MODEL slx_7c77e1fec809
KIND model
CONFIG AbsTol = auto
CONFIG EnableMultiTasking = on
CONFIG FixedStep = step_size
CONFIG InitFcn = , if any(exist('rtifpga_mdlclblib', 'file') ~= 0), rtifpga_mdlclblib('Init', bdroot); end,\n, if any(exist('dsmpb_private', 'file') ~= 0), dsmpb_private('dsmpb_mdlclblib', 'Init', bdroot); end,\n
CONFIG MaxStep = auto
CONFIG MinStep = auto
CONFIG PostLoadFcn = if any(exist('dsrtsu_mdlpostloadfcn', 'file') ~= 0), dsrtsu_mdlpostloadfcn('Execute', bdroot); end
CONFIG RelTol = 1e-3
CONFIG SampleTimeConstraint = Unconstrained
CONFIG SolverName = ode1
CONFIG StartTime = 0.0
CONFIG StopTime = t_end
BLOCK [Clock] Clock1
BLOCK [Display] Display
  Decimation = 1
BLOCK [Display] Display1
  Decimation = 1
BLOCK [Display] Display2
  Decimation = 1
BLOCK [Display] Display3
  Decimation = 1
BLOCK [Display] Display5
  Decimation = 1
BLOCK [Display] Display6
  Decimation = 1
BLOCK [Display] Display7
  Decimation = 1
BLOCK [SubSystem] Distance Check
BLOCK [SubSystem] Distance Check/Distance Change Security Check
BLOCK [Constant] Distance Check/Distance Change Security Check/Constant
  Value = start_distance_check
BLOCK [Constant] Distance Check/Distance Change Security Check/Constant1
  Value = break_criteria
BLOCK [SubSystem] Distance Check/Distance Change Security Check/MATLAB Function
  ErrorFcn = Stateflow.Translate.translate
  PermitHierarchicalResolution = ExplicitOnly
  SFBlockType = MATLAB Function
  TreatAsAtomicUnit = on
BLOCK [Demux] Distance Check/Distance Change Security Check/MATLAB Function/ Demux 
  Outputs = 1
BLOCK [S-Function] Distance Check/Distance Change Security Check/MATLAB Function/ SFunction 
  EnableBusSupport = on
  FunctionName = sf_sfun
  PortCounts = [4 2]
  SFcnIsStateOwnerBlock = off
  SFunctionDeploymentMode = off
  Tag = Stateflow S-Function 2
BLOCK [Terminator] Distance Check/Distance Change Security Check/MATLAB Function/ Terminator 
BLOCK [Outport] Distance Check/Distance Change Security Check/MATLAB Function/bool_stop
BLOCK [Inport] Distance Check/Distance Change Security Check/MATLAB Function/break_criteria
  Port = 4
BLOCK [Inport] Distance Check/Distance Change Security Check/MATLAB Function/s
BLOCK [Inport] Distance Check/Distance Change Security Check/MATLAB Function/s_old
  Port = 2
BLOCK [Inport] Distance Check/Distance Change Security Check/MATLAB Function/start_distance_check
  Port = 3
BLOCK [Memory] Distance Check/Distance Change Security Check/Memory
  InheritSampleTime = on
BLOCK [Outport] Distance Check/Distance Change Security Check/bool_stop
BLOCK [Inport] Distance Check/Distance Change Security Check/s
BLOCK [Stop] Distance Check/Stop Simulation
BLOCK [ToWorkspace] Distance Check/To Workspace24
  FixptAsFi = on
  MaxDataPoints = 1
  SampleTime = -1
  Save2DSignal = 2-D array (concatenate along first dimension)
  VariableName = bool_stop
BLOCK [Inport] Distance Check/s (m)
BLOCK [SubSystem] Finish Line
BLOCK [Constant] Finish Line/Constant
  Value = 0
BLOCK [Constant] Finish Line/Constant1
BLOCK [Stop] Finish Line/Stop Simulation
BLOCK [Inport] Finish Line/s (m)
BLOCK [Switch] Finish Line/s>finish line
  InputSameDT = off
  SaturateOnIntegerOverflow = off
  Threshold = s_track(end)
BLOCK [Gain] Finish Line/s_ist
BLOCK [Display] Finish Time // s
  Decimation = 1
BLOCK [From] From
  GotoTag = T_wr
  TagVisibility = global
BLOCK [From] From1
  GotoTag = v_ist
  TagVisibility = global
BLOCK [From] From2
  GotoTag = v_des
  TagVisibility = global
BLOCK [From] From3
  GotoTag = T_wr_LSTM
  TagVisibility = global
BLOCK [From] From4
  GotoTag = noisy_meas
  TagVisibility = global
BLOCK [From] From5
  GotoTag = MHE_results
  TagVisibility = global
BLOCK [From] From7
  GotoTag = MPC_solver_status
  TagVisibility = global
BLOCK [From] From8
  GotoTag = MHE_solverstatus
  TagVisibility = global
BLOCK [SubSystem] MPC
  NameLocation = top
BLOCK [Sum] MPC/Add
  IconShape = rectangular
  Inputs = +++
BLOCK [Clock] MPC/Clock
BLOCK [Constant] MPC/Constant
  NameLocation = top
  SampleTime = options.Ts
  Value = u_max
BLOCK [Constant] MPC/Constant1
  SampleTime = options.Ts
  Value = lbx_ac
BLOCK [Constant] MPC/Constant10
  SampleTime = options.Ts
  Value = ubx_ac_e
BLOCK [Constant] MPC/Constant11
  SampleTime = options.Ts
  Value = options.P
BLOCK [Constant] MPC/Constant2
  SampleTime = options.Ts
  Value = ubx_ac
BLOCK [Constant] MPC/Constant3
  SampleTime = options.Ts
  Value = u_ref
BLOCK [Constant] MPC/Constant4
  NameLocation = top
  SampleTime = options.Ts
  Value = u_min
  VectorParams1D = off
BLOCK [Constant] MPC/Constant5
  SampleTime = options.Ts
  Value = lbh_ac
BLOCK [Constant] MPC/Constant6
  SampleTime = options.Ts
  Value = options.P
BLOCK [Constant] MPC/Constant8
  SampleTime = options.Ts
  Value = lbx_ac_e
BLOCK [Constant] MPC/Constant9
  SampleTime = options.Ts
  Value = ubh_ac
BLOCK [Demux] MPC/Demux
  Outputs = 3
BLOCK [Demux] MPC/Demux1
  Outputs = options.n_controls
BLOCK [Demux] MPC/Demux2
  Commented = on
  Outputs = 3
BLOCK [Display] MPC/Display
  Decimation = 1
BLOCK [Display] MPC/Display10
  Decimation = 1
BLOCK [Display] MPC/Display11
  Decimation = 1
BLOCK [Display] MPC/Display12
  Decimation = 1
BLOCK [Display] MPC/Display17
  Decimation = 1
BLOCK [Display] MPC/Display18
  Decimation = 1
BLOCK [Display] MPC/Display2
  Decimation = 1
BLOCK [Display] MPC/Display21
  Decimation = 1
  NameLocation = top
BLOCK [Display] MPC/Display24
  Decimation = 1
BLOCK [Display] MPC/Display25
  Decimation = 1
BLOCK [Display] MPC/Display3
  Commented = on
  Decimation = 1
BLOCK [Display] MPC/Display4
  Decimation = 1
BLOCK [Display] MPC/Display5
  Decimation = 1
BLOCK [Display] MPC/Display6
  Decimation = 1
BLOCK [Display] MPC/Display7
  Decimation = 1
BLOCK [Display] MPC/Display8
  Decimation = 1
BLOCK [From] MPC/From1
  GotoTag = T_wr
  TagVisibility = global
BLOCK [From] MPC/From10
  Commented = on
  GotoTag = torque_em_brk
  TagVisibility = global
BLOCK [From] MPC/From11
  Commented = on
  GotoTag = torque_fric_brk
  TagVisibility = global
BLOCK [From] MPC/From2
  GotoTag = v_ist
  TagVisibility = global
BLOCK [From] MPC/From3
  GotoTag = v_des
  TagVisibility = global
BLOCK [From] MPC/From8
  GotoTag = solver_x_LSTM
  TagVisibility = global
BLOCK [From] MPC/From9
  Commented = on
  GotoTag = torque_em_acc
  TagVisibility = global
BLOCK [Gain] MPC/Gain
  Gain = pi/180
BLOCK [Gain] MPC/Gain1
  Gain = FDR/r_dyn
BLOCK [Goto] MPC/Goto
  GotoTag = solver_x_LSTM
  TagVisibility = global
BLOCK [Goto] MPC/Goto2
  GotoTag = phi_values
  TagVisibility = global
BLOCK [Goto] MPC/Goto3
  GotoTag = MPC_solver_status
  TagVisibility = global
BLOCK [Ground] MPC/Ground
  Commented = on
BLOCK [Ground] MPC/Ground1
  Commented = on
BLOCK [Ground] MPC/Ground2
  Commented = on
BLOCK [SubSystem] MPC/MATLAB Function
  ErrorFcn = Stateflow.Translate.translate
  PermitHierarchicalResolution = ExplicitOnly
  SFBlockType = MATLAB Function
  TreatAsAtomicUnit = on
BLOCK [Demux] MPC/MATLAB Function/ Demux 
  Outputs = 1
BLOCK [S-Function] MPC/MATLAB Function/ SFunction 
  EnableBusSupport = on
  FunctionName = sf_sfun
  PortCounts = [3 2]
  SFcnIsStateOwnerBlock = off
  SFunctionDeploymentMode = off
  Tag = Stateflow S-Function 6
BLOCK [Terminator] MPC/MATLAB Function/ Terminator 
BLOCK [Inport] MPC/MATLAB Function/P
  Port = 3
BLOCK [Inport] MPC/MATLAB Function/u1
  Port = 2
BLOCK [Inport] MPC/MATLAB Function/x
BLOCK [Outport] MPC/MATLAB Function/y_ref_merged
  VectorParamsAs1DForOutWhenUnconnected = off
BLOCK [SubSystem] MPC/MATLAB Function1
  ErrorFcn = Stateflow.Translate.translate
  PermitHierarchicalResolution = ExplicitOnly
  SFBlockType = MATLAB Function
  TreatAsAtomicUnit = on
BLOCK [Demux] MPC/MATLAB Function1/ Demux 
  Outputs = 1
BLOCK [S-Function] MPC/MATLAB Function1/ SFunction 
  EnableBusSupport = on
  FunctionName = sf_sfun
  PortCounts = [3 2]
  SFcnIsStateOwnerBlock = off
  SFunctionDeploymentMode = off
  Tag = Stateflow S-Function 12
BLOCK [Terminator] MPC/MATLAB Function1/ Terminator 
BLOCK [Inport] MPC/MATLAB Function1/P
  Port = 3
BLOCK [Outport] MPC/MATLAB Function1/par_traj_merged
  VectorParamsAs1DForOutWhenUnconnected = off
BLOCK [Inport] MPC/MATLAB Function1/phi
BLOCK [Inport] MPC/MATLAB Function1/v_r
  Port = 2
BLOCK [Memory] MPC/Memory
  InheritSampleTime = on
BLOCK [Product] MPC/Multiply
BLOCK [Mux] MPC/Mux
  DisplayOption = bar
  Inputs = 2
BLOCK [Mux] MPC/Mux1
  DisplayOption = bar
  Inputs = 3
BLOCK [Mux] MPC/Mux2
  Commented = on
  Inputs = 6
BLOCK [SubSystem] MPC/Pred_Traj_and_costs_calc
  Commented = on
BLOCK [Sum] MPC/Pred_Traj_and_costs_calc/Add
  IconShape = rectangular
  Inputs = +++
BLOCK [Outport] MPC/Pred_Traj_and_costs_calc/Costs
  VectorParamsAs1DForOutWhenUnconnected = off
BLOCK [Display] MPC/Pred_Traj_and_costs_calc/Display1
  Decimation = 1
BLOCK [Display] MPC/Pred_Traj_and_costs_calc/Display15
  Decimation = 1
BLOCK [Display] MPC/Pred_Traj_and_costs_calc/Display16
  Decimation = 1
BLOCK [Display] MPC/Pred_Traj_and_costs_calc/Display17
  Decimation = 1
BLOCK [Display] MPC/Pred_Traj_and_costs_calc/Display19
  Decimation = 1
BLOCK [Display] MPC/Pred_Traj_and_costs_calc/Display2
  Decimation = 1
BLOCK [Display] MPC/Pred_Traj_and_costs_calc/Display3
  Decimation = 1
BLOCK [Display] MPC/Pred_Traj_and_costs_calc/Display4
  Decimation = 1
BLOCK [Display] MPC/Pred_Traj_and_costs_calc/Display5
  Decimation = 1
BLOCK [Display] MPC/Pred_Traj_and_costs_calc/Display6
  Decimation = 1
BLOCK [Display] MPC/Pred_Traj_and_costs_calc/Display9
  Decimation = 1
BLOCK [Gain] MPC/Pred_Traj_and_costs_calc/Gain1
  Gain = FDR/r_dyn
BLOCK [Gain] MPC/Pred_Traj_and_costs_calc/Gain2
  Gain = (FDR*30)/(pi*r_dyn)
BLOCK [Product] MPC/Pred_Traj_and_costs_calc/Multiply
BLOCK [Selector] MPC/Pred_Traj_and_costs_calc/Selector1
  IndexOptions = Index vector (dialog)
  Indices = [2:options.n_controls:options.n_controls*options.P]
  InputPortWidth = options.n_controls*options.P
  OutputSizes = 1
BLOCK [Selector] MPC/Pred_Traj_and_costs_calc/Selector10
  IndexOptions = Index vector (dialog)
  Indices = [1]
  InputPortWidth = options.P
  OutputSizes = 1
BLOCK [Selector] MPC/Pred_Traj_and_costs_calc/Selector11
  IndexOptions = Index vector (dialog)
  Indices = [1]
  InputPortWidth = options.P
  OutputSizes = 1
BLOCK [Selector] MPC/Pred_Traj_and_costs_calc/Selector12
  IndexOptions = Index vector (dialog)
  Indices = [1]
  InputPortWidth = options.P
  OutputSizes = 1
BLOCK [Selector] MPC/Pred_Traj_and_costs_calc/Selector13
  IndexOptions = Index vector (dialog)
  Indices = [1:options.n_controls:options.n_controls*options.P]
  InputPortWidth = options.n_controls*options.P
  OutputSizes = 1
BLOCK [Selector] MPC/Pred_Traj_and_costs_calc/Selector2
  IndexOptions = Index vector (dialog)
  Indices = [3:options.n_controls:options.n_controls*options.P]
  InputPortWidth = options.n_controls*options.P
  OutputSizes = 1
BLOCK [Selector] MPC/Pred_Traj_and_costs_calc/Selector4
  IndexOptions = Index vector (dialog)
  Indices = [2:options.n_states:options.n_states*options.P-2]
  InputPortWidth = options.n_states*options.P
  OutputSizes = 1
BLOCK [Selector] MPC/Pred_Traj_and_costs_calc/Selector5
  IndexOptions = Index vector (dialog)
  Indices = [3:options.n_states:options.n_states*options.P-1]
  InputPortWidth = options.n_states*options.P
  OutputSizes = 1
BLOCK [Selector] MPC/Pred_Traj_and_costs_calc/Selector7
  IndexOptions = Index vector (dialog)
  Indices = [1:options.n_states:options.n_states*options.P-3]
  InputPortWidth = options.n_states*options.P
  OutputSizes = 1
BLOCK [Selector] MPC/Pred_Traj_and_costs_calc/Selector8
  IndexOptions = Index vector (dialog)
  Indices = [options.n_states:options.n_states:options.n_states*options.P]
  InputPortWidth = options.n_states*options.P
  OutputSizes = 1
BLOCK [Selector] MPC/Pred_Traj_and_costs_calc/Selector9
  IndexOptions = Index vector (dialog)
  Indices = [1]
  InputPortWidth = options.P
  OutputSizes = 1
BLOCK [SubSystem] MPC/Pred_Traj_and_costs_calc/Subsystem
BLOCK [Constant] MPC/Pred_Traj_and_costs_calc/Subsystem/Constant
  Value = Q(3,3)
BLOCK [Constant] MPC/Pred_Traj_and_costs_calc/Subsystem/Constant1
  Value = R(1,1)
BLOCK [Constant] MPC/Pred_Traj_and_costs_calc/Subsystem/Constant2
  Value = U(1,1)
BLOCK [Constant] MPC/Pred_Traj_and_costs_calc/Subsystem/Constant3
  Value = options.P
BLOCK [SubSystem] MPC/Pred_Traj_and_costs_calc/Subsystem/MATLAB Function
  ErrorFcn = Stateflow.Translate.translate
  PermitHierarchicalResolution = ExplicitOnly
  SFBlockType = MATLAB Function
  TreatAsAtomicUnit = on
BLOCK [Demux] MPC/Pred_Traj_and_costs_calc/Subsystem/MATLAB Function/ Demux 
  Outputs = 1
BLOCK [S-Function] MPC/Pred_Traj_and_costs_calc/Subsystem/MATLAB Function/ SFunction 
  EnableBusSupport = off
  FunctionName = sf_sfun
  PortCounts = [8 6]
  SFcnIsStateOwnerBlock = off
  SFunctionDeploymentMode = off
  Tag = Stateflow S-Function 9
BLOCK [Terminator] MPC/Pred_Traj_and_costs_calc/Subsystem/MATLAB Function/ Terminator 
BLOCK [Inport] MPC/Pred_Traj_and_costs_calc/Subsystem/MATLAB Function/P
  Port = 8
BLOCK [Inport] MPC/Pred_Traj_and_costs_calc/Subsystem/MATLAB Function/Q
  Port = 5
BLOCK [Inport] MPC/Pred_Traj_and_costs_calc/Subsystem/MATLAB Function/R
  Port = 6
BLOCK [Inport] MPC/Pred_Traj_and_costs_calc/Subsystem/MATLAB Function/U
  Port = 7
BLOCK [Outport] MPC/Pred_Traj_and_costs_calc/Subsystem/MATLAB Function/cost
  VectorParamsAs1DForOutWhenUnconnected = off
BLOCK [Outport] MPC/Pred_Traj_and_costs_calc/Subsystem/MATLAB Function/cost_Q
  Port = 2
  VectorParamsAs1DForOutWhenUnconnected = off
BLOCK [Outport] MPC/Pred_Traj_and_costs_calc/Subsystem/MATLAB Function/cost_R
  Port = 3
  VectorParamsAs1DForOutWhenUnconnected = off
BLOCK [Outport] MPC/Pred_Traj_and_costs_calc/Subsystem/MATLAB Function/cost_U
  Port = 4
  VectorParamsAs1DForOutWhenUnconnected = off
BLOCK [Outport] MPC/Pred_Traj_and_costs_calc/Subsystem/MATLAB Function/cost_traj
  Port = 5
  VectorParamsAs1DForOutWhenUnconnected = off
BLOCK [Inport] MPC/Pred_Traj_and_costs_calc/Subsystem/MATLAB Function/dt_u
  Port = 4
BLOCK [Inport] MPC/Pred_Traj_and_costs_calc/Subsystem/MATLAB Function/u
  Port = 3
BLOCK [Inport] MPC/Pred_Traj_and_costs_calc/Subsystem/MATLAB Function/v
BLOCK [Inport] MPC/Pred_Traj_and_costs_calc/Subsystem/MATLAB Function/v_ref
  Port = 2
BLOCK [ToWorkspace] MPC/Pred_Traj_and_costs_calc/Subsystem/To Workspace
  FixptAsFi = on
  MaxDataPoints = inf
  SampleTime = -1
  VariableName = cost_v
BLOCK [ToWorkspace] MPC/Pred_Traj_and_costs_calc/Subsystem/To Workspace1
  FixptAsFi = on
  MaxDataPoints = inf
  SampleTime = -1
  VariableName = cost_u
BLOCK [ToWorkspace] MPC/Pred_Traj_and_costs_calc/Subsystem/To Workspace2
  FixptAsFi = on
  MaxDataPoints = inf
  SampleTime = -1
  VariableName = cost_du
BLOCK [ToWorkspace] MPC/Pred_Traj_and_costs_calc/Subsystem/To Workspace3
  FixptAsFi = on
  MaxDataPoints = inf
  SampleTime = -1
  VariableName = cost_traj
BLOCK [Outport] MPC/Pred_Traj_and_costs_calc/Subsystem/cost
  VectorParamsAs1DForOutWhenUnconnected = off
BLOCK [Inport] MPC/Pred_Traj_and_costs_calc/Subsystem/dt_u
  Port = 4
BLOCK [Inport] MPC/Pred_Traj_and_costs_calc/Subsystem/u
  Port = 3
BLOCK [Inport] MPC/Pred_Traj_and_costs_calc/Subsystem/v
BLOCK [Inport] MPC/Pred_Traj_and_costs_calc/Subsystem/v_ref
  Port = 2
BLOCK [Sum] MPC/Pred_Traj_and_costs_calc/Subtract
  IconShape = rectangular
  Inputs = +-
BLOCK [ToWorkspace] MPC/Pred_Traj_and_costs_calc/To Workspace
  FixptAsFi = on
  MaxDataPoints = inf
  SampleTime = -1
  SaveFormat = Timeseries
  VariableName = P_EM_pred
BLOCK [ToWorkspace] MPC/Pred_Traj_and_costs_calc/To Workspace1
  FixptAsFi = on
  MaxDataPoints = inf
  SampleTime = -1
  SaveFormat = Timeseries
  VariableName = v_minus_v_ref_pred
BLOCK [ToWorkspace] MPC/Pred_Traj_and_costs_calc/To Workspace16
  FixptAsFi = on
  MaxDataPoints = inf
  SampleTime = -1
  VariableName = T_r_pred
BLOCK [ToWorkspace] MPC/Pred_Traj_and_costs_calc/To Workspace17
  FixptAsFi = on
  MaxDataPoints = inf
  SampleTime = -1
  VariableName = v_pred
BLOCK [ToWorkspace] MPC/Pred_Traj_and_costs_calc/To Workspace18
  FixptAsFi = on
  MaxDataPoints = inf
  SampleTime = -1
  VariableName = M_EM_pred
BLOCK [ToWorkspace] MPC/Pred_Traj_and_costs_calc/To Workspace19
  FixptAsFi = on
  MaxDataPoints = inf
  SampleTime = -1
  VariableName = T_w_pred1
BLOCK [ToWorkspace] MPC/Pred_Traj_and_costs_calc/To Workspace20
  FixptAsFi = on
  MaxDataPoints = inf
  SampleTime = -1
  VariableName = T_r_pred1
BLOCK [ToWorkspace] MPC/Pred_Traj_and_costs_calc/To Workspace21
  FixptAsFi = on
  MaxDataPoints = inf
  SampleTime = -1
  VariableName = v_pred1
BLOCK [ToWorkspace] MPC/Pred_Traj_and_costs_calc/To Workspace22
  FixptAsFi = on
  MaxDataPoints = inf
  SampleTime = -1
  VariableName = M_EM_pred1
BLOCK [ToWorkspace] MPC/Pred_Traj_and_costs_calc/To Workspace23
  FixptAsFi = on
  MaxDataPoints = inf
  SampleTime = -1
  VariableName = T_w_pred
BLOCK [Inport] MPC/Pred_Traj_and_costs_calc/control_traj_pred
  Port = 2
BLOCK [Inport] MPC/Pred_Traj_and_costs_calc/state_traj_pred
  Port = 3
BLOCK [Inport] MPC/Pred_Traj_and_costs_calc/v_ref
BLOCK [RateTransition] MPC/Rate Transition3
  Commented = on
  InitialCondition = M_EM_acc_0
  OutPortSampleTime = options.Ts
BLOCK [RateTransition] MPC/Rate Transition4
  Commented = on
  InitialCondition = M_EM_acc_0
  OutPortSampleTime = options.Ts
BLOCK [RateTransition] MPC/Rate Transition5
  Commented = on
  InitialCondition = M_EM_acc_0
  OutPortSampleTime = options.Ts
BLOCK [Reshape] MPC/Reshape
BLOCK [S-Function] MPC/S-Function
  EnableBusSupport = off
  FunctionName = acados_solver_sfunction_LSTM_v21
  SFcnIsStateOwnerBlock = off
  SFunctionDeploymentMode = off
BLOCK [Scope] MPC/Scope
  Floating = off
  NumInputPorts = 1
  ScopeSpecificationString = Simulink.scopes.TimeScopeBlockCfg('CurrentConfiguration', extmgr.ConfigurationSet(extmgr.Configuration('Core','General UI',true),extmgr.Configuration('Core','Source UI',true),extmgr.Configuration('Sources','WiredSimulink',true,'DataLoggingVariableName','ScopeData1'),extmgr.Configuration('Visuals','Time Domain',true,'SerializedDisplays',{struct('MinYLimReal','-10.00000','MaxYLimReal','10.00000','YL...<+1574ch>
BLOCK [Scope] MPC/Scope1
  Floating = off
  NumInputPorts = 2
  ScopeSpecificationString = Simulink.scopes.TimeScopeBlockCfg('CurrentConfiguration', extmgr.ConfigurationSet(extmgr.Configuration('Core','General UI',true),extmgr.Configuration('Core','Source UI',true),extmgr.Configuration('Sources','WiredSimulink',true,'DataLoggingVariableName','ScopeData1'),extmgr.Configuration('Visuals','Time Domain',true),extmgr.Configuration('Tools','Plot Navigation',true),extmgr.Configuration('Tools',...<+40ch>
BLOCK [Selector] MPC/Selector
  IndexOptions = Index vector (dialog)
  Indices = [options.n_states-2:options.n_states]
  InputPortWidth = options.n_states
  OutputSizes = 1
BLOCK [Selector] MPC/Selector1
  IndexOptions = Index vector (dialog)
  Indices = [((options.P-1)*options.n_outputs+1):(options.P*(options.n_outputs))]
  OutputSizes = 1
BLOCK [Selector] MPC/Selector11
  IndexOptions = Index vector (dialog)
  Indices = [1:((options.P-1)*(options.n_outputs))]
  OutputSizes = 1
BLOCK [Selector] MPC/Selector2
  IndexOptions = Index vector (dialog)
  Indices = [1:(options.P*(options.n_outputs))]
  InputPortWidth = 160
  OutputSizes = 1
BLOCK [Selector] MPC/Selector5
  IndexOptions = Index vector (dialog)
  Indices = [1:(options.n_outputs)]
  OutputSizes = 1
BLOCK [Selector] MPC/Selector6
  IndexOptions = Index vector (dialog)
  Indices = [(options. P*2+1):(options.P*3)]
  InputPortWidth = options.P*(3)
  OutputSizes = 1
BLOCK [Selector] MPC/Selector7
  IndexOptions = Index vector (dialog)
  Indices = [options.n_states_bound+1:options.n_states]
  InputPortWidth = options.n_states
  OutputSizes = 1
BLOCK [Selector] MPC/Selector8
  IndexOptions = Index vector (dialog)
  Indices = [1:((options.P+1)*(options.n_parameter))]
  InputPortWidth = 160
  OutputSizes = 1
BLOCK [SubSystem] MPC/SolverStop
BLOCK [Clock] MPC/SolverStop/Clock
BLOCK [Constant] MPC/SolverStop/Constant
  Value = 0
BLOCK [SubSystem] MPC/SolverStop/MATLAB Function
  ErrorFcn = Stateflow.Translate.translate
  PermitHierarchicalResolution = ExplicitOnly
  SFBlockType = MATLAB Function
  TreatAsAtomicUnit = on
BLOCK [Demux] MPC/SolverStop/MATLAB Function/ Demux 
  Outputs = 1
BLOCK [S-Function] MPC/SolverStop/MATLAB Function/ SFunction 
  EnableBusSupport = on
  FunctionName = sf_sfun
  PortCounts = [1 2]
  SFcnIsStateOwnerBlock = off
  SFunctionDeploymentMode = off
  Tag = Stateflow S-Function 7
BLOCK [Terminator] MPC/SolverStop/MATLAB Function/ Terminator 
BLOCK [Outport] MPC/SolverStop/MATLAB Function/bool_stop
BLOCK [Inport] MPC/SolverStop/MATLAB Function/solver_status
BLOCK [Switch] MPC/SolverStop/Switch
  Criteria = u2 > Threshold
  InputSameDT = off
  SaturateOnIntegerOverflow = off
  Threshold = t_mpc_on
BLOCK [Outport] MPC/SolverStop/bool_stop
BLOCK [Inport] MPC/SolverStop/solver_status
BLOCK [Terminator] MPC/Terminator
BLOCK [ToWorkspace] MPC/To Workspace
  FixptAsFi = on
  MaxDataPoints = inf
  SampleTime = -1
  VariableName = v_mpc_ref
BLOCK [ToWorkspace] MPC/To Workspace1
  FixptAsFi = on
  MaxDataPoints = inf
  SampleTime = options.Ts
  Save2DSignal = 2-D array (concatenate along first dimension)
  VariableName = solver_status
BLOCK [ToWorkspace] MPC/To Workspace10
  FixptAsFi = on
  MaxDataPoints = inf
  SampleTime = -1
  VariableName = model_lbx_ac
BLOCK [ToWorkspace] MPC/To Workspace11
  FixptAsFi = on
  MaxDataPoints = inf
  SampleTime = -1
  VariableName = model_ubx_ac
BLOCK [ToWorkspace] MPC/To Workspace12
  FixptAsFi = on
  MaxDataPoints = inf
  SampleTime = -1
  VariableName = model_u_min
BLOCK [ToWorkspace] MPC/To Workspace13
  FixptAsFi = on
  MaxDataPoints = inf
  SampleTime = -1
  VariableName = model_u_max
BLOCK [ToWorkspace] MPC/To Workspace14
  FixptAsFi = on
  MaxDataPoints = inf
  SampleTime = -1
  VariableName = model_x_meas
BLOCK [ToWorkspace] MPC/To Workspace16
  FixptAsFi = on
  MaxDataPoints = 1
  SampleTime = -1
  Save2DSignal = 2-D array (concatenate along first dimension)
  VariableName = solver_u0
BLOCK [ToWorkspace] MPC/To Workspace17
  FixptAsFi = on
  MaxDataPoints = inf
  SampleTime = -1
  VariableName = model_y_ref_0
BLOCK [ToWorkspace] MPC/To Workspace18
  FixptAsFi = on
  MaxDataPoints = inf
  SampleTime = -1
  VariableName = model_lbx_ac_e
BLOCK [ToWorkspace] MPC/To Workspace19
  FixptAsFi = on
  MaxDataPoints = inf
  SampleTime = -1
  VariableName = model_ubx_ac_e
BLOCK [ToWorkspace] MPC/To Workspace2
  FixptAsFi = on
  MaxDataPoints = inf
  SampleTime = options.Ts
  Save2DSignal = 2-D array (concatenate along first dimension)
  VariableName = solver_kkt_residuals
BLOCK [ToWorkspace] MPC/To Workspace20
  FixptAsFi = on
  MaxDataPoints = inf
  SampleTime = -1
  VariableName = model_lh
BLOCK [ToWorkspace] MPC/To Workspace21
  FixptAsFi = on
  MaxDataPoints = inf
  SampleTime = -1
  VariableName = model_uh
BLOCK [ToWorkspace] MPC/To Workspace22
  FixptAsFi = on
  MaxDataPoints = inf
  SampleTime = -1
  VariableName = phi_values
BLOCK [ToWorkspace] MPC/To Workspace23
  FixptAsFi = on
  MaxDataPoints = inf
  SampleTime = -1
  Save2DSignal = 2-D array (concatenate along first dimension)
  VariableName = states_from_solver
BLOCK [ToWorkspace] MPC/To Workspace24
  FixptAsFi = on
  MaxDataPoints = 1
  SampleTime = -1
  Save2DSignal = 2-D array (concatenate along first dimension)
  VariableName = bool_solver_stop
BLOCK [ToWorkspace] MPC/To Workspace25
  Commented = on
  FixptAsFi = on
  MaxDataPoints = inf
  SampleTime = -1
  VariableName = cost
BLOCK [ToWorkspace] MPC/To Workspace26
  FixptAsFi = on
  MaxDataPoints = inf
  SampleTime = -1
  Save2DSignal = 2-D array (concatenate along first dimension)
  VariableName = P_EM_calc
BLOCK [ToWorkspace] MPC/To Workspace3
  FixptAsFi = on
  MaxDataPoints = inf
  SampleTime = options.Ts
  Save2DSignal = 2-D array (concatenate along first dimension)
  VariableName = solver_first_state
BLOCK [ToWorkspace] MPC/To Workspace30
  FixptAsFi = on
  MaxDataPoints = inf
  SampleTime = -1
  VariableName = mv
BLOCK [ToWorkspace] MPC/To Workspace4
  FixptAsFi = on
  MaxDataPoints = inf
  SampleTime = options.Ts
  Save2DSignal = 2-D array (concatenate along first dimension)
  VariableName = solver_cpu_time
BLOCK [ToWorkspace] MPC/To Workspace5
  FixptAsFi = on
  MaxDataPoints = inf
  SampleTime = options.Ts
  Save2DSignal = 2-D array (concatenate along first dimension)
  VariableName = solver_control_opti
BLOCK [ToWorkspace] MPC/To Workspace6
  FixptAsFi = on
  MaxDataPoints = inf
  SampleTime = options.Ts
  Save2DSignal = 2-D array (concatenate along first dimension)
  VariableName = solver_sqp_iter
BLOCK [ToWorkspace] MPC/To Workspace7
  FixptAsFi = on
  MaxDataPoints = inf
  SampleTime = -1
  VariableName = model_y_ref
BLOCK [ToWorkspace] MPC/To Workspace8
  FixptAsFi = on
  MaxDataPoints = inf
  SampleTime = -1
  VariableName = model_y_ref_e
BLOCK [ToWorkspace] MPC/To Workspace9
  FixptAsFi = on
  MaxDataPoints = inf
  SampleTime = -1
  VariableName = model_p
BLOCK [Gain] MPC/model_lbx_ac
BLOCK [Gain] MPC/model_lbx_ac_e
BLOCK [Gain] MPC/model_lh
BLOCK [Gain] MPC/model_p
BLOCK [Gain] MPC/model_u_max
BLOCK [Gain] MPC/model_u_min
BLOCK [Gain] MPC/model_ubx_ac
BLOCK [Gain] MPC/model_ubx_ac_e
BLOCK [Gain] MPC/model_uh
BLOCK [Gain] MPC/model_x_meas
BLOCK [Gain] MPC/model_y_ref1
BLOCK [Inport] MPC/phi
  Port = 3
BLOCK [Outport] MPC/sol_controls
  VectorParamsAs1DForOutWhenUnconnected = off
BLOCK [Gain] MPC/solver_control_opti
BLOCK [Gain] MPC/solver_cpu_time
BLOCK [Gain] MPC/solver_first_state
BLOCK [Gain] MPC/solver_kkt_residuals
BLOCK [Gain] MPC/solver_sqp_iter
BLOCK [Gain] MPC/solver_status
BLOCK [Inport] MPC/x_meas
BLOCK [Inport] MPC/x_ref
  Port = 2
BLOCK [SubSystem] Noise_Sensors
  NameLocation = top
BLOCK [Logic] Noise_Sensors/AND
  AllPortsSameDT = off
  IconShape = distinctive
  OutDataTypeStr = boolean
BLOCK [Logic] Noise_Sensors/AND1
  AllPortsSameDT = off
  IconShape = distinctive
  OutDataTypeStr = boolean
BLOCK [Sum] Noise_Sensors/Add
  IconShape = rectangular
BLOCK [Sum] Noise_Sensors/Add1
  IconShape = rectangular
  Inputs = +++
BLOCK [Clock] Noise_Sensors/Clock
BLOCK [Constant] Noise_Sensors/Constant
  Value = 400
BLOCK [Constant] Noise_Sensors/Constant1
  Value = -5
BLOCK [Constant] Noise_Sensors/Constant2
  Value = 0
BLOCK [Constant] Noise_Sensors/Constant3
  Value = 399
BLOCK [Constant] Noise_Sensors/Constant4
  Value = 100
BLOCK [Constant] Noise_Sensors/Constant7
  Value = 99
BLOCK [Goto] Noise_Sensors/Goto
  GotoTag = noisy_meas
  TagVisibility = global
BLOCK [RelationalOperator] Noise_Sensors/GreaterThan
  InputSameDT = off
  Operator = >
  OutDataTypeStr = boolean
  RndMeth = Simplest
BLOCK [RelationalOperator] Noise_Sensors/GreaterThan1
  InputSameDT = off
  Operator = <=
  OutDataTypeStr = boolean
  RndMeth = Simplest
BLOCK [RelationalOperator] Noise_Sensors/GreaterThan2
  InputSameDT = off
  Operator = >
  OutDataTypeStr = boolean
  RndMeth = Simplest
BLOCK [RelationalOperator] Noise_Sensors/GreaterThan3
  InputSameDT = off
  Operator = <=
  OutDataTypeStr = boolean
  RndMeth = Simplest
BLOCK [Ground] Noise_Sensors/Ground
BLOCK [Outport] Noise_Sensors/LSTM_temp
  Port = 3
BLOCK [Outport] Noise_Sensors/Noisy_temp
  Port = 2
BLOCK [Outport] Noise_Sensors/Orig_temp
BLOCK [RandomNumber] Noise_Sensors/Random Number
  SampleTime = 0.1
  Variance = 3
BLOCK [RandomNumber] Noise_Sensors/Random Number1
  Commented = on
  Mean = -2
  SampleTime = 0.5
  Variance = 0.5
BLOCK [RandomNumber] Noise_Sensors/Random Number2
  Commented = on
  SampleTime = 0.1
  Variance = 0.1
BLOCK [RandomNumber] Noise_Sensors/Random Number3
  Mean = -2
  SampleTime = 0.1
  Variance = 0.1
BLOCK [RateTransition] Noise_Sensors/Rate Transition
BLOCK [Switch] Noise_Sensors/Switch
  Criteria = u2 > Threshold
  InputSameDT = off
  SaturateOnIntegerOverflow = off
BLOCK [Switch] Noise_Sensors/Switch1
  Criteria = u2 > Threshold
  InputSameDT = off
  SaturateOnIntegerOverflow = off
BLOCK [Inport] Noise_Sensors/Twr_LSTM
BLOCK [Inport] Noise_Sensors/Twr_orig
  Port = 2
BLOCK [Display] Racing Distance // m
  Decimation = 1
BLOCK [RateTransition] Rate Transition
BLOCK [RateTransition] Rate Transition1
  InitialCondition = X0_ref
  NameLocation = top
  OutPortSampleTime = options.Ts
BLOCK [RateTransition] Rate Transition2
  InitialCondition = parameter_0(1:(options.P+1))
  NameLocation = top
  OutPortSampleTime = options.Ts
BLOCK [RateTransition] Rate Transition3
  Deterministic = off
  InitialCondition = [T_w_0, T_r_0]
  NameLocation = left
  OutPortSampleTime = options.Ts
BLOCK [RateTransition] Rate Transition4
  InitialCondition = v_0
  NameLocation = left
  OutPortSampleTime = options.Ts
BLOCK [RateTransition] Rate Transition5
  InitialCondition = [mpc_init_EM_acc, mpc_init_EM_brk, mpc_init_fric_brk]
  NameLocation = right
  OutPortSampleTime = step_size
BLOCK [RateTransition] Rate Transition6
  Deterministic = off
  InitialCondition = [v_0]
  NameLocation = left
  OutPortSampleTime = options.Ts
BLOCK [RateTransition] Rate Transition7
  InitialCondition = v_0
  OutPortSampleTime = step_size
BLOCK [RateTransition] Rate Transition8
  Deterministic = off
  InitialCondition = [T_w_0, T_r_0]
  NameLocation = left
  OutPortSampleTime = options.Ts
BLOCK [SubSystem] Reference Trajectory
BLOCK [Clock] Reference Trajectory/Clock
BLOCK [Constant] Reference Trajectory/Constant1
  Value = T_ref
BLOCK [Delay] Reference Trajectory/Delay
  DelayLength = options.Ts/step_size
  InitialCondition = 0
  InputPortMap = u0
BLOCK [Concatenate] Reference Trajectory/Matrix Concatenate
  ConcatenateDimension = 2
  Mode = Multidimensional array
BLOCK [Memory] Reference Trajectory/Memory
  InitialCondition = grade_track(1:options.P)
BLOCK [Mux] Reference Trajectory/Mux
  DisplayOption = bar
  Inputs = 2
BLOCK [Lookup_n-D] Reference Trajectory/Referenze
  BreakpointsForDimension1 = s_track
  InputPortMap = u0
  InternalRulePriority = Speed
  NumberOfTableDimensions = 1
  RndMeth = Simplest
  Table = v_track
BLOCK [Selector] Reference Trajectory/Selector
  IndexOptions = Index vector (dialog)
  Indices = [1]
  InputPortWidth = options.P
  OutputSizes = 1
BLOCK [Terminator] Reference Trajectory/Terminator
BLOCK [ToWorkspace] Reference Trajectory/To Workspace
  FixptAsFi = on
  MaxDataPoints = 1
  SampleTime = -1
  Save2DSignal = 2-D array (concatenate along first dimension)
  VariableName = v_preview
BLOCK [ToWorkspace] Reference Trajectory/To Workspace1
  FixptAsFi = on
  MaxDataPoints = 1
  SampleTime = -1
  Save2DSignal = 2-D array (concatenate along first dimension)
  VariableName = phi_preview
BLOCK [ToWorkspace] Reference Trajectory/To Workspace2
  FixptAsFi = on
  MaxDataPoints = 1
  SampleTime = -1
  Save2DSignal = 2-D array (concatenate along first dimension)
  VariableName = a_preview
BLOCK [Lookup_n-D] Reference Trajectory/Track speed 
  BreakpointsForDimension1 = s_track
  InputPortMap = u0
  InternalRulePriority = Speed
  NumberOfTableDimensions = 1
  RndMeth = Simplest
  Table = v_track
BLOCK [Inport] Reference Trajectory/a_ist
  Port = 2
  PortDimensions = 1
BLOCK [Gain] Reference Trajectory/a_prev
BLOCK [SubSystem] Reference Trajectory/distance preview
  ErrorFcn = Stateflow.Translate.translate
  PermitHierarchicalResolution = ExplicitOnly
  SFBlockType = MATLAB Function
  TreatAsAtomicUnit = on
BLOCK [Demux] Reference Trajectory/distance preview/ Demux 
  Outputs = 1
BLOCK [S-Function] Reference Trajectory/distance preview/ SFunction 
  EnableBusSupport = on
  FunctionName = sf_sfun
  PortCounts = [9 3]
  SFcnIsStateOwnerBlock = off
  SFunctionDeploymentMode = off
  Tag = Stateflow S-Function 4
BLOCK [Terminator] Reference Trajectory/distance preview/ Terminator 
BLOCK [Inport] Reference Trajectory/distance preview/Ts
  Port = 4
BLOCK [Inport] Reference Trajectory/distance preview/a_ist
  Port = 3
BLOCK [Outport] Reference Trajectory/distance preview/a_prev
  Port = 2
  VectorParamsAs1DForOutWhenUnconnected = off
BLOCK [Inport] Reference Trajectory/distance preview/delta_v_matrix
  Port = 8
BLOCK [Inport] Reference Trajectory/distance preview/p_hor
  Port = 5
BLOCK [Inport] Reference Trajectory/distance preview/s_ist
  Port = 2
BLOCK [Inport] Reference Trajectory/distance preview/s_matrix
  Port = 6
BLOCK [Outport] Reference Trajectory/distance preview/s_prev
  VectorParamsAs1DForOutWhenUnconnected = off
BLOCK [Inport] Reference Trajectory/distance preview/t_in
  Port = 9
BLOCK [Inport] Reference Trajectory/distance preview/v_ist
BLOCK [Inport] Reference Trajectory/distance preview/v_prev_old
  Port = 7
BLOCK [Constant] Reference Trajectory/horizon
  Value = options.P
BLOCK [Constant] Reference Trajectory/horizon1
  Value = zeros(options.P,1)
BLOCK [Constant] Reference Trajectory/horizon3
  Value = zeros(options.P-1,1)
BLOCK [Outport] Reference Trajectory/phi_prev
  Port = 2
  VectorParamsAs1DForOutWhenUnconnected = off
BLOCK [Gain] Reference Trajectory/phi_prev_vector
BLOCK [Inport] Reference Trajectory/s
  PortDimensions = 1
BLOCK [Constant] Reference Trajectory/sample time mpc
  Value = options.Ts
  VectorParams1D = off
BLOCK [Gain] Reference Trajectory/sim_time
BLOCK [Lookup_n-D] Reference Trajectory/track grade
  BreakpointsForDimension1 = s_track
  InputPortMap = u0
  InternalRulePriority = Speed
  NumberOfTableDimensions = 1
  RndMeth = Simplest
  Table = grade_track
BLOCK [Inport] Reference Trajectory/v_ist
  Port = 3
  PortDimensions = 1
BLOCK [Outport] Reference Trajectory/v_prev
  Port = 4
  VectorParamsAs1DForOutWhenUnconnected = off
BLOCK [Outport] Reference Trajectory/v_ref
  Port = 3
  VectorParamsAs1DForOutWhenUnconnected = off
BLOCK [Gain] Reference Trajectory/v_track
BLOCK [Outport] Reference Trajectory/y_ref
  VectorParamsAs1DForOutWhenUnconnected = off
BLOCK [Gain] Reference Trajectory/y_ref_vector
BLOCK [SubSystem] Save Block
BLOCK [Clock] Save Block/Clock
BLOCK [Demux] Save Block/Demux
  Outputs = 2
BLOCK [Demux] Save Block/Demux1
  Outputs = 2
BLOCK [Demux] Save Block/Demux2
  Outputs = 2
BLOCK [SubSystem] Save Block/Energy calculation1
BLOCK [Abs] Save Block/Energy calculation1/Abs
  SaturateOnIntegerOverflow = off
BLOCK [Abs] Save Block/Energy calculation1/Abs1
  SaturateOnIntegerOverflow = off
BLOCK [Abs] Save Block/Energy calculation1/Abs2
  NameLocation = right
  SaturateOnIntegerOverflow = off
BLOCK [Abs] Save Block/Energy calculation1/Abs3
  SaturateOnIntegerOverflow = off
BLOCK [Abs] Save Block/Energy calculation1/Abs6
  SaturateOnIntegerOverflow = off
BLOCK [Constant] Save Block/Energy calculation1/Constant
  Value = 0
BLOCK [Constant] Save Block/Energy calculation1/Constant1
  Value = 0
BLOCK [Constant] Save Block/Energy calculation1/Constant3
BLOCK [Display] Save Block/Energy calculation1/Display
  Decimation = 1
BLOCK [Display] Save Block/Energy calculation1/Display1
  Decimation = 1
BLOCK [Display] Save Block/Energy calculation1/Display2
  Decimation = 1
BLOCK [Product] Save Block/Energy calculation1/Divide
  Inputs = */
BLOCK [Product] Save Block/Energy calculation1/Divide1
  Inputs = */*
BLOCK [Product] Save Block/Energy calculation1/Divide2
  Inputs = /*
BLOCK [Lookup_n-D] Save Block/Energy calculation1/EM efficiency
  BreakpointsForDimension1 = data_efficiency(2:end,1)
  BreakpointsForDimension2 = data_efficiency(1,2:end)
  InputPortMap = u0,u1
  InternalRulePriority = Speed
  RndMeth = Simplest
  Table = data_efficiency(2:end,2:end)
BLOCK [Lookup_n-D] Save Block/Energy calculation1/EM efficiency1
  BreakpointsForDimension1 = data_efficiency(2:end,1)
  BreakpointsForDimension2 = data_efficiency(1,2:end)
  InputPortMap = u0,u1
  InternalRulePriority = Speed
  RndMeth = Simplest
  Table = data_efficiency(2:end,2:end)
BLOCK [Lookup_n-D] Save Block/Energy calculation1/EM efficiency2
  BreakpointsForDimension1 = data_efficiency(2:end,1)
  BreakpointsForDimension2 = data_efficiency(1,2:end)
  InputPortMap = u0,u1
  InternalRulePriority = Speed
  RndMeth = Simplest
  Table = data_efficiency(2:end,2:end)
BLOCK [Outport] Save Block/Energy calculation1/E_delta
  Port = 3
  VectorParamsAs1DForOutWhenUnconnected = off
BLOCK [Outport] Save Block/Energy calculation1/E_rekup
  VectorParamsAs1DForOutWhenUnconnected = off
BLOCK [Outport] Save Block/Energy calculation1/E_used
  Port = 2
  VectorParamsAs1DForOutWhenUnconnected = off
BLOCK [From] Save Block/Energy calculation1/From1
  GotoTag = torque_em
  TagVisibility = global
BLOCK [From] Save Block/Energy calculation1/From2
  GotoTag = n_em
  TagVisibility = global
BLOCK [From] Save Block/Energy calculation1/From29
  GotoTag = torque_em
  TagVisibility = global
BLOCK [From] Save Block/Energy calculation1/From3
  GotoTag = n_em
  TagVisibility = global
BLOCK [From] Save Block/Energy calculation1/From30
  GotoTag = n_em
  TagVisibility = global
BLOCK [Gain] Save Block/Energy calculation1/Gain
  Gain = 1/3600*1/1000
BLOCK [Gain] Save Block/Energy calculation1/Gain1
  Gain = 2*pi/60
BLOCK [Gain] Save Block/Energy calculation1/Gain2
  Gain = 1/3600*1/1000
BLOCK [Gain] Save Block/Energy calculation1/Gain3
  Gain = 2*pi/60
BLOCK [Gain] Save Block/Energy calculation1/Gain4
  Gain = 1/3600*1/1000
BLOCK [Gain] Save Block/Energy calculation1/Gain5
  Gain = 2*pi/60
BLOCK [Gain] Save Block/Energy calculation1/Gain6
  Gain = 1/100
BLOCK [Gain] Save Block/Energy calculation1/Gain7
  Gain = 1/100
  NameLocation = left
BLOCK [Gain] Save Block/Energy calculation1/Gain8
  Gain = 1/100
  NameLocation = left
BLOCK [Integrator] Save Block/Energy calculation1/Integrator
BLOCK [Integrator] Save Block/Energy calculation1/Integrator1
BLOCK [Integrator] Save Block/Energy calculation1/Integrator2
BLOCK [Product] Save Block/Energy calculation1/Product
  Inputs = 3
BLOCK [Product] Save Block/Energy calculation1/Product1
BLOCK [Scope] Save Block/Energy calculation1/Scope1
  Floating = off
  NumInputPorts = 2
  ScopeSpecificationString = Simulink.scopes.TimeScopeBlockCfg('CurrentConfiguration', extmgr.ConfigurationSet(extmgr.Configuration('Core','General UI',true),extmgr.Configuration('Core','Source UI',true),extmgr.Configuration('Sources','WiredSimulink',true,'DataLoggingVariableName','ScopeData1'),extmgr.Configuration('Visuals','Time Domain',true,'SerializedDisplays',{struct('MinYLimReal','-20.07353','MaxYLimReal','180.66173','Y...<+2048ch>
BLOCK [Switch] Save Block/Energy calculation1/Switch
  Criteria = u2 > Threshold
  InputSameDT = off
  SaturateOnIntegerOverflow = off
BLOCK [Switch] Save Block/Energy calculation1/Switch1
  Criteria = u2 > Threshold
  InputSameDT = off
  SaturateOnIntegerOverflow = off
BLOCK [Switch] Save Block/Energy calculation1/Switch3
  Criteria = u2 > Threshold
  InputSameDT = off
  SaturateOnIntegerOverflow = off
BLOCK [From] Save Block/From1
  GotoTag = v_ist
  TagVisibility = global
BLOCK [From] Save Block/From2
  GotoTag = MHE_results
  TagVisibility = global
BLOCK [From] Save Block/From3
  GotoTag = noisy_meas
  TagVisibility = global
BLOCK [From] Save Block/From6
  GotoTag = T_wr
  TagVisibility = global
BLOCK [RateTransition] Save Block/Rate Transition1
  InitialCondition = T_r_0
  OutPortSampleTime = options.Ts
BLOCK [RateTransition] Save Block/Rate Transition2
  OutPortSampleTime = options.Ts
BLOCK [RateTransition] Save Block/Rate Transition6
  InitialCondition = T_w_0
  OutPortSampleTime = options.Ts
BLOCK [Selector] Save Block/Selector1
  IndexOptions = Index vector (dialog)
  Indices = [1:2]
  InputPortWidth = 18
  OutputSizes = 1
BLOCK [ToWorkspace] Save Block/To Workspace
  FixptAsFi = on
  MaxDataPoints = inf
  SampleTime = -1
  Save2DSignal = 2-D array (concatenate along first dimension)
  VariableName = v_car_ts
BLOCK [ToWorkspace] Save Block/To Workspace1
  FixptAsFi = on
  MaxDataPoints = inf
  SampleTime = -1
  Save2DSignal = 2-D array (concatenate along first dimension)
  VariableName = T_w_ts
BLOCK [ToWorkspace] Save Block/To Workspace11
  FixptAsFi = on
  MaxDataPoints = inf
  SampleTime = -1
  Save2DSignal = 2-D array (concatenate along first dimension)
  VariableName = t_out
BLOCK [ToWorkspace] Save Block/To Workspace13
  FixptAsFi = on
  MaxDataPoints = 1
  SampleTime = -1
  Save2DSignal = 2-D array (concatenate along first dimension)
  VariableName = t_finish
BLOCK [ToWorkspace] Save Block/To Workspace2
  FixptAsFi = on
  MaxDataPoints = inf
  SampleTime = -1
  Save2DSignal = 2-D array (concatenate along first dimension)
  VariableName = T_r_ts
BLOCK [ToWorkspace] Save Block/To Workspace20
  FixptAsFi = on
  MaxDataPoints = inf
  SampleTime = -1
  Save2DSignal = 2-D array (concatenate along first dimension)
  VariableName = v_car
BLOCK [ToWorkspace] Save Block/To Workspace3
  FixptAsFi = on
  MaxDataPoints = inf
  SampleTime = -1
  Save2DSignal = 2-D array (concatenate along first dimension)
  VariableName = T_w_mhe
BLOCK [ToWorkspace] Save Block/To Workspace4
  FixptAsFi = on
  MaxDataPoints = inf
  SampleTime = -1
  Save2DSignal = 2-D array (concatenate along first dimension)
  VariableName = T_r_mhe
BLOCK [ToWorkspace] Save Block/To Workspace5
  FixptAsFi = on
  MaxDataPoints = inf
  SampleTime = -1
  Save2DSignal = 2-D array (concatenate along first dimension)
  VariableName = T_w_noisy
BLOCK [ToWorkspace] Save Block/To Workspace6
  FixptAsFi = on
  MaxDataPoints = inf
  SampleTime = -1
  Save2DSignal = 2-D array (concatenate along first dimension)
  VariableName = T_r_noisy
BLOCK [ToWorkspace] Save Block/To Workspace7
  FixptAsFi = on
  MaxDataPoints = inf
  SampleTime = -1
  Save2DSignal = 2-D array (concatenate along first dimension)
  VariableName = T_w
BLOCK [ToWorkspace] Save Block/To Workspace8
  FixptAsFi = on
  MaxDataPoints = inf
  SampleTime = -1
  Save2DSignal = 2-D array (concatenate along first dimension)
  VariableName = T_r
BLOCK [ToWorkspace] Save Block/s_ref12
  FixptAsFi = on
  MaxDataPoints = inf
  SampleTime = -1
  Save2DSignal = 2-D array (concatenate along first dimension)
  VariableName = E_total
BLOCK [ToWorkspace] Save Block/s_ref15
  FixptAsFi = on
  MaxDataPoints = inf
  SampleTime = -1
  Save2DSignal = 2-D array (concatenate along first dimension)
  VariableName = E_rekup
BLOCK [ToWorkspace] Save Block/s_ref16
  FixptAsFi = on
  MaxDataPoints = inf
  SampleTime = -1
  Save2DSignal = 2-D array (concatenate along first dimension)
  VariableName = E_delta
BLOCK [Scope] Scope
  Floating = off
  IOType = viewer
  NumInputPorts = 1
  ScopeSpecificationString = Simulink.scopes.TimeScopeBlockCfg('CurrentConfiguration', extmgr.ConfigurationSet(extmgr.Configuration('Core','General UI',true),extmgr.Configuration('Core','Source UI',true),extmgr.Configuration('Sources','WiredSimulink',true,'DataLoggingVariableName','ScopeData1'),extmgr.Configuration('Visuals','Time Domain',true,'SerializedDisplays',{struct('MinYLimReal','-1.2503','MaxYLimReal','16.38918','YLab...<+1391ch>
BLOCK [Scope] Scope1
  Floating = off
  IOType = viewer
  NumInputPorts = 1
  ScopeSpecificationString = Simulink.scopes.TimeScopeBlockCfg('CurrentConfiguration', extmgr.ConfigurationSet(extmgr.Configuration('Core','General UI',true),extmgr.Configuration('Core','Source UI',true),extmgr.Configuration('Sources','WiredSimulink',true,'DataLoggingVariableName','ScopeData2'),extmgr.Configuration('Visuals','Time Domain',true,'SerializedDisplays',{struct('MinYLimReal','-8.76511','MaxYLimReal','52.11682','YLa...<+1363ch>
BLOCK [Scope] Scope2
  Floating = off
  IOType = viewer
  NumInputPorts = 1
  ScopeSpecificationString = Simulink.scopes.TimeScopeBlockCfg('CurrentConfiguration', extmgr.ConfigurationSet(extmgr.Configuration('Core','General UI',true),extmgr.Configuration('Core','Source UI',true),extmgr.Configuration('Sources','WiredSimulink',true,'DataLoggingVariableName','ScopeData3'),extmgr.Configuration('Visuals','Time Domain',true,'SerializedDisplays',{struct('MinYLimReal','-0.69246','MaxYLimReal','3.00021','YLab...<+1359ch>
BLOCK [Scope] Scope3
  Floating = off
  NumInputPorts = 4
  ScopeSpecificationString = Simulink.scopes.TimeScopeBlockCfg('CurrentConfiguration', extmgr.ConfigurationSet(extmgr.Configuration('Core','General UI',true),extmgr.Configuration('Core','Source UI',true),extmgr.Configuration('Sources','WiredSimulink',true,'DataLoggingVariableName','ScopeData1'),extmgr.Configuration('Visuals','Time Domain',true,'SerializedDisplays',{struct('MinYLimReal','128.97758','MaxYLimReal','163.34337','Y...<+2229ch>
BLOCK [Selector] Selector1
  IndexOptions = Index vector (dialog)
  Indices = [1:2]
  InputPortWidth = 18
  OutputSizes = 1
BLOCK [SubSystem] State-Estimation
  NameLocation = top
BLOCK [Constant] State-Estimation/Constant2
  Value = SE_selector_sim
BLOCK [Inport] State-Estimation/LSTM_temp
  Port = 3
BLOCK [MultiPortSwitch] State-Estimation/Multiport Switch
  InputSameDT = off
  Inputs = 2
  SaturateOnIntegerOverflow = off
BLOCK [Mux] State-Estimation/Mux4
  DisplayOption = bar
  Inputs = 2
BLOCK [Mux] State-Estimation/Mux7
  DisplayOption = bar
  Inputs = 2
BLOCK [Outport] State-Estimation/Output
BLOCK [Terminator] State-Estimation/Terminator1
BLOCK [Inport] State-Estimation/Velocity
  Port = 4
BLOCK [SubSystem] State-Estimation/moving_horizon_estimator
BLOCK [Buffer] State-Estimation/moving_horizon_estimator/Buffer1
  N = (options_mhe.P+1)*options_mhe.n_parameter
  OutputFrames = off
  V = ((options_mhe.P+1)*options_mhe.n_parameter)-options_mhe.n_parameter
BLOCK [Buffer] State-Estimation/moving_horizon_estimator/Buffer2
  N = (options_mhe.P-1)*nout
  OutputFrames = off
  V = (options_mhe.P-2)*nout
  ic = repmat([60;60;0;0],13,1)
BLOCK [Constant] State-Estimation/moving_horizon_estimator/Constant
  NameLocation = right
  Value = zeros(2,1)
BLOCK [Constant] State-Estimation/moving_horizon_estimator/Constant1
  SampleTime = options.Ts
  Value = repmat(lbx_mhe,14,1)
BLOCK [Constant] State-Estimation/moving_horizon_estimator/Constant2
  SampleTime = options.Ts
  Value = repmat(ubx_mhe,14,1)
BLOCK [Constant] State-Estimation/moving_horizon_estimator/Constant4
  SampleTime = options.Ts
  Value = repmat(ubu_mhe,15,1)
BLOCK [Display] State-Estimation/moving_horizon_estimator/Cost value
  Decimation = 1
BLOCK [Reference] State-Estimation/moving_horizon_estimator/Create Diagonal Matrix  REF=matrix_library/Create Diagonal
Matrix
  LibrarySourceBlock = simulink/Matrix\nOperations/Create Diagonal\nMatrix
  SourceBlock = matrix_library/Create Diagonal\nMatrix
  SourceType = Create Diagonal Matrix
BLOCK [Reference] State-Estimation/moving_horizon_estimator/Create Diagonal Matrix1  REF=matrix_library/Create Diagonal
Matrix
  LibrarySourceBlock = simulink/Matrix\nOperations/Create Diagonal\nMatrix
  SourceBlock = matrix_library/Create Diagonal\nMatrix
  SourceType = Create Diagonal Matrix
BLOCK [Delay] State-Estimation/moving_horizon_estimator/Delay
  DelayLength = 1
  InitialCondition = 60
  InputPortMap = u0
BLOCK [Delay] State-Estimation/moving_horizon_estimator/Delay1
  DelayLength = 1
  InitialCondition = options_mhe.x0
  InputPortMap = u0
BLOCK [Delay] State-Estimation/moving_horizon_estimator/Delay2
  DelayLength = 1
  InitialCondition = [60;60]
  InputPortMap = u0
BLOCK [Delay] State-Estimation/moving_horizon_estimator/Delay3
  DelayLength = 1
  InitialCondition = 60
  InputPortMap = u0
BLOCK [Demux] State-Estimation/moving_horizon_estimator/Demux
  Outputs = 2
BLOCK [Demux] State-Estimation/moving_horizon_estimator/Demux1
  Commented = on
  Outputs = 2
BLOCK [Demux] State-Estimation/moving_horizon_estimator/Demux2
  Outputs = 2
BLOCK [Display] State-Estimation/moving_horizon_estimator/Display
  Decimation = 1
BLOCK [Display] State-Estimation/moving_horizon_estimator/Display1
  Decimation = 1
BLOCK [Display] State-Estimation/moving_horizon_estimator/Display5
  Decimation = 1
BLOCK [From] State-Estimation/moving_horizon_estimator/From
  GotoTag = phi_values
  TagVisibility = global
BLOCK [From] State-Estimation/moving_horizon_estimator/From1
  GotoTag = torque_em_brk
  TagVisibility = global
BLOCK [From] State-Estimation/moving_horizon_estimator/From5
  GotoTag = torque_em_acc
  TagVisibility = global
BLOCK [From] State-Estimation/moving_horizon_estimator/From6
  GotoTag = torque_fric_brk
  TagVisibility = global
BLOCK [Gain] State-Estimation/moving_horizon_estimator/Gain
  Gain = -1
BLOCK [Goto] State-Estimation/moving_horizon_estimator/Goto1
  GotoTag = MHE_results
  TagVisibility = global
BLOCK [Goto] State-Estimation/moving_horizon_estimator/Goto2
  GotoTag = MHE_solverstatus
  TagVisibility = global
BLOCK [Display] State-Estimation/moving_horizon_estimator/KKT residual
  Decimation = 1
BLOCK [Display] State-Estimation/moving_horizon_estimator/KKT residuals (4x)
  Decimation = 1
BLOCK [Mux] State-Estimation/moving_horizon_estimator/Mux
  DisplayOption = bar
  Inputs = 3
BLOCK [Mux] State-Estimation/moving_horizon_estimator/Mux1
  DisplayOption = bar
  Inputs = 5
BLOCK [Mux] State-Estimation/moving_horizon_estimator/Mux2
  DisplayOption = bar
BLOCK [Outport] State-Estimation/moving_horizon_estimator/Output
BLOCK [Constant] State-Estimation/moving_horizon_estimator/Q
  Value = 0.001 * ([0.2; 0.2])
  VectorParams1D = off
BLOCK [Constant] State-Estimation/moving_horizon_estimator/Q0
  Value = 100 * ([0.1; 0.1])
BLOCK [Constant] State-Estimation/moving_horizon_estimator/R
  Value = [0.7; 0.7]
BLOCK [RateTransition] State-Estimation/moving_horizon_estimator/Rate Transition
  OutPortSampleTime = options_mhe.Ts
BLOCK [RateTransition] State-Estimation/moving_horizon_estimator/Rate Transition1
  OutPortSampleTime = options_mhe.Ts
BLOCK [RateTransition] State-Estimation/moving_horizon_estimator/Rate Transition2
  OutPortSampleTime = options_mhe.Ts
BLOCK [Reshape] State-Estimation/moving_horizon_estimator/Reshape1
BLOCK [Reshape] State-Estimation/moving_horizon_estimator/Reshape2
BLOCK [Reshape] State-Estimation/moving_horizon_estimator/Reshape3
BLOCK [Reshape] State-Estimation/moving_horizon_estimator/Reshape4
BLOCK [S-Function] State-Estimation/moving_horizon_estimator/S-Function
  EnableBusSupport = off
  FunctionName = acados_solver_sfunction_LSTM_v21_MHE
  SFcnIsStateOwnerBlock = off
  SFunctionDeploymentMode = off
BLOCK [Selector] State-Estimation/moving_horizon_estimator/Selector
  IndexOptions = Index vector (dialog)
  Indices = 1
  InputPortWidth = 41
  OutputSizes = 1
BLOCK [Selector] State-Estimation/moving_horizon_estimator/Selector3
  IndexOptions = Index vector (dialog)
  Indices = [1 2]
  InputPortWidth = 2+(numHiddenUnits*2)
  OutputSizes = 1
BLOCK [Selector] State-Estimation/moving_horizon_estimator/Selector4
  IndexOptions = Index vector (dialog)
  Indices = [(18*15)+1:18*16]
  InputPortWidth = 288
  OutputSizes = 1
BLOCK [Selector] State-Estimation/moving_horizon_estimator/Selector5
  IndexOptions = Index vector (dialog)
  Indices = [1 2]
  InputPortWidth = 18
  OutputSizes = 1
BLOCK [Selector] State-Estimation/moving_horizon_estimator/Selector6
  Commented = on
  IndexOptions = Index vector (dialog)
  Indices = [(18*14)+1:18*15]
  InputPortWidth = 18*15
  OutputSizes = 1
BLOCK [Selector] State-Estimation/moving_horizon_estimator/Selector7
  Commented = on
  IndexOptions = Index vector (dialog)
  Indices = [1:2]
  InputPortWidth = 18
  OutputSizes = 1
BLOCK [Display] State-Estimation/moving_horizon_estimator/Solver status
  Decimation = 1
BLOCK [ToWorkspace] State-Estimation/moving_horizon_estimator/To Workspace
  Commented = on
  FixptAsFi = on
  MaxDataPoints = inf
  SampleTime = -1
  Save2DSignal = 2-D array (concatenate along first dimension)
  VariableName = T_w_Control
BLOCK [ToWorkspace] State-Estimation/moving_horizon_estimator/To Workspace1
  Commented = on
  FixptAsFi = on
  MaxDataPoints = inf
  SampleTime = -1
  Save2DSignal = 2-D array (concatenate along first dimension)
  VariableName = T_r_Control
BLOCK [Concatenate] State-Estimation/moving_horizon_estimator/Vector Concatenate
BLOCK [Concatenate] State-Estimation/moving_horizon_estimator/Vector Concatenate1
  NumInputs = 3
BLOCK [Concatenate] State-Estimation/moving_horizon_estimator/Vector Concatenate2
BLOCK [Inport] State-Estimation/moving_horizon_estimator/Velocity
  Port = 2
BLOCK [Inport] State-Estimation/moving_horizon_estimator/noisy_temp
BLOCK [Display] State-Estimation/moving_horizon_estimator/solver_cpu_time
  Decimation = 1
BLOCK [Display] State-Estimation/moving_horizon_estimator/solver_sqp_iter
  Decimation = 1
BLOCK [Display] State-Estimation/moving_horizon_estimator/u0
  Decimation = 1
BLOCK [Inport] State-Estimation/noisy_temp
  Port = 2
BLOCK [Inport] State-Estimation/orig_temp
BLOCK [ToWorkspace] To Workspace
  FixptAsFi = on
  MaxDataPoints = inf
  SampleTime = -1
  SaveFormat = Timeseries
  VariableName = u_min_calc
BLOCK [ToWorkspace] To Workspace1
  FixptAsFi = on
  MaxDataPoints = inf
  SampleTime = -1
  SaveFormat = Timeseries
  VariableName = u_max_calc
BLOCK [SubSystem] Vehicle Model
BLOCK [Inport] Vehicle Model/ v_des (m//s)
  PortDimensions = 1
BLOCK [Clock] Vehicle Model/Clock
BLOCK [Constant] Vehicle Model/Constant1
  Value = [1; 0; 0]
BLOCK [Demux] Vehicle Model/Demux
  Outputs = 3
BLOCK [Demux] Vehicle Model/Demux1
  Commented = on
  Outputs = 2
BLOCK [Demux] Vehicle Model/Demux3
  Commented = on
  Outputs = 2
BLOCK [Reference] Vehicle Model/Discrete Derivative  REF=simulink/Discrete/Discrete Derivative
  Commented = on
  SourceBlock = simulink/Discrete/Discrete Derivative
  SourceType = Discrete Derivative
BLOCK [SubSystem] Vehicle Model/Driver Model
  NameLocation = top
BLOCK [Saturate] Vehicle Model/Driver Model/-1 to 1 
  LowerLimit = -1
  UpperLimit = 1
BLOCK [Gain] Vehicle Model/Driver Model/1//Ti_c
  Gain = 1/Ti_c
  OutDataTypeStr = Inherit: Same as input
  ParamDataTypeStr = Inherit: Same as input
  SaturateOnIntegerOverflow = on
BLOCK [Gain] Vehicle Model/Driver Model/1//Tt_c
  Gain = 1/Tt_c
  OutDataTypeStr = Inherit: Same as input
  ParamDataTypeStr = Inherit: Same as input
  SaturateOnIntegerOverflow = on
BLOCK [Integrator] Vehicle Model/Driver Model/Integrator1
BLOCK [Gain] Vehicle Model/Driver Model/Kp_c
  Gain = Kp_c
  OutDataTypeStr = Inherit: Same as input
  ParamDataTypeStr = Inherit: Same as input
  SaturateOnIntegerOverflow = on
BLOCK [Gain] Vehicle Model/Driver Model/Normalize
  Gain = 1/v_max_c
  NameLocation = top
  OutDataTypeStr = Inherit: Same as input
  ParamDataTypeStr = Inherit: Same as input
  SaturateOnIntegerOverflow = on
BLOCK [Gain] Vehicle Model/Driver Model/Normalize1
  Gain = 1/v_max_c
  NameLocation = top
  OutDataTypeStr = Inherit: Same as input
  ParamDataTypeStr = Inherit: Same as input
  SaturateOnIntegerOverflow = on
BLOCK [Sum] Vehicle Model/Driver Model/Sum1
  IconShape = rectangular
  InputSameDT = on
  OutDataTypeStr = Inherit: Same as first input
  SaturateOnIntegerOverflow = on
BLOCK [Sum] Vehicle Model/Driver Model/Sum5
  IconShape = rectangular
  InputSameDT = on
  Inputs = -+
  NameLocation = right
  OutDataTypeStr = Inherit: Same as first input
  SaturateOnIntegerOverflow = on
BLOCK [Sum] Vehicle Model/Driver Model/Sum7
  IconShape = rectangular
  InputSameDT = on
  Inputs = +-
  NameLocation = top
  OutDataTypeStr = Inherit: Same as first input
  SaturateOnIntegerOverflow = on
BLOCK [Sum] Vehicle Model/Driver Model/Sum8
  IconShape = rectangular
  InputSameDT = on
  OutDataTypeStr = Inherit: Same as first input
  SaturateOnIntegerOverflow = on
BLOCK [Outport] Vehicle Model/Driver Model/driver_cmd
  VectorParamsAs1DForOutWhenUnconnected = off
BLOCK [Inport] Vehicle Model/Driver Model/v_des (km//h)
  NameLocation = top
  Port = 2
BLOCK [Inport] Vehicle Model/Driver Model/v_veh (km//h)
BLOCK [Goto] Vehicle Model/Goto
  GotoTag = T_wr
  TagVisibility = global
BLOCK [Goto] Vehicle Model/Goto1
  GotoTag = n_em
  TagVisibility = global
BLOCK [Goto] Vehicle Model/Goto2
  GotoTag = torque_em
  TagVisibility = global
BLOCK [Goto] Vehicle Model/Goto3
  GotoTag = v_des
  NameLocation = top
  TagVisibility = global
BLOCK [Goto] Vehicle Model/Goto4
  GotoTag = v_ist
  NameLocation = top
  TagVisibility = global
BLOCK [Goto] Vehicle Model/Goto5
  Commented = on
  GotoTag = T_wr_LPTN
  TagVisibility = global
BLOCK [Goto] Vehicle Model/Goto7
  GotoTag = T_wr_LSTM
  TagVisibility = global
BLOCK [SubSystem] Vehicle Model/LSTM-Based Thermal Model grad
BLOCK [Constant] Vehicle Model/LSTM-Based Thermal Model grad/Constant3
  Value = YMin_mhe
BLOCK [Constant] Vehicle Model/LSTM-Based Thermal Model grad/Constant4
  Value = T_cool
BLOCK [Delay] Vehicle Model/LSTM-Based Thermal Model grad/Delay
  DelayLength = 1
  InitialCondition = [T_w_0;T_r_0]
  InputPortMap = u0
BLOCK [Demux] Vehicle Model/LSTM-Based Thermal Model grad/Demux4
  Outputs = 2
BLOCK [Demux] Vehicle Model/LSTM-Based Thermal Model grad/Demux5
  Commented = on
  Outputs = 2
BLOCK [DiscreteIntegrator] Vehicle Model/LSTM-Based Thermal Model grad/Discrete-Time Integrator
  ICPrevOutput = DiscIntNeverNeededParam
  ICPrevScaledInput = DiscIntNeverNeededParam
  InitialCondition = [T_w_0;T_r_0]
  InitialConditionSetting = Auto
  SampleTime = -1
  gainval = 1
BLOCK [From] Vehicle Model/LSTM-Based Thermal Model grad/From1
  Commented = on
  GotoTag = T_wr
  TagVisibility = global
BLOCK [Gain] Vehicle Model/LSTM-Based Thermal Model grad/Gain2
  Gain = 1/n_em_max
BLOCK [Gain] Vehicle Model/LSTM-Based Thermal Model grad/Gain3
  Gain = 1/M_EM_acc_max
BLOCK [Gain] Vehicle Model/LSTM-Based Thermal Model grad/Gain6
  Gain = YMax_mhe-YMin_mhe
BLOCK [Gain] Vehicle Model/LSTM-Based Thermal Model grad/Gain7
  Gain = 1/(T_max-T_cool)
BLOCK [Gain] Vehicle Model/LSTM-Based Thermal Model grad/Gain8
  Gain = 1/(T_max-T_cool)
BLOCK [Mux] Vehicle Model/LSTM-Based Thermal Model grad/Mux
  DisplayOption = bar
BLOCK [Reshape] Vehicle Model/LSTM-Based Thermal Model grad/Reshape
  OutputDimensionality = Customize
  OutputDimensions = [4,1]
BLOCK [Inport] Vehicle Model/LSTM-Based Thermal Model grad/Rotational_Speed [rpm]
  NameLocation = top
BLOCK [Reference] Vehicle Model/LSTM-Based Thermal Model grad/Stateful Predict  REF=deeplib/Stateful Predict
  SourceBlock = deeplib/Stateful Predict
  SourceType = Stateful Predict
BLOCK [Sum] Vehicle Model/LSTM-Based Thermal Model grad/Sum2
  Inputs = |++
BLOCK [Sum] Vehicle Model/LSTM-Based Thermal Model grad/Sum3
  Inputs = -+|
BLOCK [Sum] Vehicle Model/LSTM-Based Thermal Model grad/Sum4
  Inputs = -+|
BLOCK [Outport] Vehicle Model/LSTM-Based Thermal Model grad/T_r_LSTM [°C]
  Port = 2
BLOCK [Outport] Vehicle Model/LSTM-Based Thermal Model grad/T_w_LSTM [°C]
BLOCK [ToWorkspace] Vehicle Model/LSTM-Based Thermal Model grad/To Workspace17
  FixptAsFi = on
  MaxDataPoints = inf
  SampleTime = -1
  SaveFormat = Timeseries
  VariableName = XTest
BLOCK [ToWorkspace] Vehicle Model/LSTM-Based Thermal Model grad/To Workspace18
  FixptAsFi = on
  MaxDataPoints = inf
  SampleTime = -1
  SaveFormat = Timeseries
  VariableName = YPred
BLOCK [Inport] Vehicle Model/LSTM-Based Thermal Model grad/Torque_EM [Nm]
  Port = 2
BLOCK [Memory] Vehicle Model/Memory
  InheritSampleTime = on
  NameLocation = top
BLOCK [Mux] Vehicle Model/Mux
  DisplayOption = bar
  Inputs = 2
  NameLocation = right
BLOCK [Mux] Vehicle Model/Mux1
  DisplayOption = bar
  Inputs = 2
BLOCK [RateTransition] Vehicle Model/Rate Transition1
  InitialCondition = n_0
  NameLocation = top
  OutPortSampleTime = options.Ts
BLOCK [RateTransition] Vehicle Model/Rate Transition10
  InitialCondition = n_0
  NameLocation = top
  OutPortSampleTime = options.Ts
BLOCK [RateTransition] Vehicle Model/Rate Transition11
  InitialCondition = T_r_0
  NameLocation = top
  OutPortSampleTime = step_size
BLOCK [RateTransition] Vehicle Model/Rate Transition2
  InitialCondition = M_EM_acc_0
  NameLocation = top
  OutPortSampleTime = step_size
BLOCK [RateTransition] Vehicle Model/Rate Transition3
  InitialCondition = M_EM_acc_0
  NameLocation = top
  OutPortSampleTime = options.Ts
BLOCK [RateTransition] Vehicle Model/Rate Transition4
  InitialCondition = n_0
  NameLocation = top
  OutPortSampleTime = step_size
BLOCK [RateTransition] Vehicle Model/Rate Transition5
  InitialCondition = [T_w_0 T_r_0]
  NameLocation = top
  OutPortSampleTime = step_size
BLOCK [RateTransition] Vehicle Model/Rate Transition6
  Commented = on
  InitialCondition = [0 0]
  NameLocation = top
  OutPortSampleTime = step_size
BLOCK [RateTransition] Vehicle Model/Rate Transition7
  InitialCondition = n_0
  NameLocation = top
  OutPortSampleTime = options.Ts
BLOCK [RateTransition] Vehicle Model/Rate Transition9
  InitialCondition = T_w_0
  NameLocation = top
  OutPortSampleTime = step_size
BLOCK [Switch] Vehicle Model/Switch
  Criteria = u2 > Threshold
  InputSameDT = off
  SaturateOnIntegerOverflow = off
  Threshold = t_mpc_on
BLOCK [Outport] Vehicle Model/T_wr_LSTM
  Port = 5
BLOCK [Gain] Vehicle Model/T_wr_gain
  Gain = gain_Twr
BLOCK [SubSystem] Vehicle Model/Thermal Model DENSO
  Commented = on
BLOCK [Ground] Vehicle Model/Thermal Model DENSO/Ground
BLOCK [Inport] Vehicle Model/Thermal Model DENSO/SpeedIn 
BLOCK [Outport] Vehicle Model/Thermal Model DENSO/T_wr
BLOCK [Outport] Vehicle Model/Thermal Model DENSO/T_wr_muxed
  Port = 2
BLOCK [Terminator] Vehicle Model/Thermal Model DENSO/Terminator
BLOCK [Terminator] Vehicle Model/Thermal Model DENSO/Terminator1
BLOCK [Inport] Vehicle Model/Thermal Model DENSO/TorqueIn
  Port = 2
BLOCK [SubSystem] Vehicle Model/Thermisches Modell EM - LPTN
  Commented = on
BLOCK [Abs] Vehicle Model/Thermisches Modell EM - LPTN/Abs
  SaturateOnIntegerOverflow = off
BLOCK [Constant] Vehicle Model/Thermisches Modell EM - LPTN/Coolant Temp
  Value = T_c
  VectorParams1D = off
BLOCK [Demux] Vehicle Model/Thermisches Modell EM - LPTN/Demux
  Outputs = 2
BLOCK [Demux] Vehicle Model/Thermisches Modell EM - LPTN/Demux1
  Outputs = 2
BLOCK [Demux] Vehicle Model/Thermisches Modell EM - LPTN/Demux2
  Outputs = 2
BLOCK [Display] Vehicle Model/Thermisches Modell EM - LPTN/Display
  Decimation = 1
BLOCK [Display] Vehicle Model/Thermisches Modell EM - LPTN/Display1
  Decimation = 1
BLOCK [Display] Vehicle Model/Thermisches Modell EM - LPTN/Display2
  Decimation = 1
BLOCK [Inport] Vehicle Model/Thermisches Modell EM - LPTN/Drehzahl_rpm
BLOCK [Constant] Vehicle Model/Thermisches Modell EM - LPTN/Environment Temp
  Value = T_e
  VectorParams1D = off
BLOCK [Gain] Vehicle Model/Thermisches Modell EM - LPTN/Gain1
  Gain = 0.8
BLOCK [Gain] Vehicle Model/Thermisches Modell EM - LPTN/Gain2
  Gain = 0.2
BLOCK [Goto] Vehicle Model/Thermisches Modell EM - LPTN/Goto
  Commented = on
  GotoTag = R_w_r
  TagVisibility = global
BLOCK [Goto] Vehicle Model/Thermisches Modell EM - LPTN/Goto1
  Commented = on
  GotoTag = R_r_e
  TagVisibility = global
BLOCK [Constant] Vehicle Model/Thermisches Modell EM - LPTN/K->C
  Value = 273.15
BLOCK [SubSystem] Vehicle Model/Thermisches Modell EM - LPTN/LPTN Model 
BLOCK [Inport] Vehicle Model/Thermisches Modell EM - LPTN/LPTN Model /1:Pw 2: Pr 3:Tc  4:Te
BLOCK [Outport] Vehicle Model/Thermisches Modell EM - LPTN/LPTN Model /1:Tw, 2:Tr
  VectorParamsAs1DForOutWhenUnconnected = off
BLOCK [Constant] Vehicle Model/Thermisches Modell EM - LPTN/LPTN Model /Constant
  NameLocation = top
  Value = R_w_r
BLOCK [Constant] Vehicle Model/Thermisches Modell EM - LPTN/LPTN Model /Constant1
  NameLocation = top
  Value = R_w_r
BLOCK [Constant] Vehicle Model/Thermisches Modell EM - LPTN/LPTN Model /Constant2
  NameLocation = top
  Value = R_w_e
BLOCK [Demux] Vehicle Model/Thermisches Modell EM - LPTN/LPTN Model /Demux
BLOCK [Product] Vehicle Model/Thermisches Modell EM - LPTN/LPTN Model /Divide
  Inputs = */
  NameLocation = top
BLOCK [Product] Vehicle Model/Thermisches Modell EM - LPTN/LPTN Model /Divide1
  Inputs = */
  NameLocation = top
BLOCK [Product] Vehicle Model/Thermisches Modell EM - LPTN/LPTN Model /Divide2
  Inputs = */
  NameLocation = top
BLOCK [Integrator] Vehicle Model/Thermisches Modell EM - LPTN/LPTN Model /Integrator
  InitialCondition = T_init(1)
BLOCK [Integrator] Vehicle Model/Thermisches Modell EM - LPTN/LPTN Model /Integrator2
  InitialCondition = T_init(2)
BLOCK [Mux] Vehicle Model/Thermisches Modell EM - LPTN/LPTN Model /Mux
  DisplayOption = bar
  Inputs = 2
BLOCK [Sum] Vehicle Model/Thermisches Modell EM - LPTN/LPTN Model /Sum
  Inputs = |+-
BLOCK [Sum] Vehicle Model/Thermisches Modell EM - LPTN/LPTN Model /Sum1
  Inputs = |+-
  NameLocation = top
BLOCK [Sum] Vehicle Model/Thermisches Modell EM - LPTN/LPTN Model /Sum2
  IconShape = rectangular
  Inputs = +++
  NameLocation = top
BLOCK [Sum] Vehicle Model/Thermisches Modell EM - LPTN/LPTN Model /Sum3
  Inputs = |+-
  NameLocation = top
BLOCK [Sum] Vehicle Model/Thermisches Modell EM - LPTN/LPTN Model /Sum4
  Inputs = |+-
  NameLocation = top
BLOCK [Sum] Vehicle Model/Thermisches Modell EM - LPTN/LPTN Model /Sum5
  Inputs = +-|
  NameLocation = top
BLOCK [Sum] Vehicle Model/Thermisches Modell EM - LPTN/LPTN Model /Sum6
  IconShape = rectangular
  NameLocation = top
BLOCK [Sum] Vehicle Model/Thermisches Modell EM - LPTN/LPTN Model /Sum7
  Inputs = |+-
  NameLocation = top
BLOCK [Sum] Vehicle Model/Thermisches Modell EM - LPTN/LPTN Model /Sum9
  Inputs = |+-
BLOCK [Gain] Vehicle Model/Thermisches Modell EM - LPTN/LPTN Model /gain
  Gain = 1/C_w
BLOCK [Gain] Vehicle Model/Thermisches Modell EM - LPTN/LPTN Model /gain1
  Gain = 1/C_r
BLOCK [Gain] Vehicle Model/Thermisches Modell EM - LPTN/LPTN Model /gain3
  Gain = 1/R_w_e
  NameLocation = top
BLOCK [Gain] Vehicle Model/Thermisches Modell EM - LPTN/LPTN Model /gain4
  Gain = 1/R_w_c
  NameLocation = top
BLOCK [Mux] Vehicle Model/Thermisches Modell EM - LPTN/Mux
  DisplayOption = bar
  Inputs = 2
BLOCK [Mux] Vehicle Model/Thermisches Modell EM - LPTN/Mux1
  DisplayOption = bar
BLOCK [SubSystem] Vehicle Model/Thermisches Modell EM - LPTN/Parameter Calculation
  Commented = on
BLOCK [Lookup_n-D] Vehicle Model/Thermisches Modell EM - LPTN/Parameter Calculation/1-D Lookup Table
  BreakpointsForDimension1 = n_vec
  InputPortMap = u0
  InternalRulePriority = Speed
  NumberOfTableDimensions = 1
  RndMeth = Simplest
  Table = optparam(:,2)
BLOCK [Lookup_n-D] Vehicle Model/Thermisches Modell EM - LPTN/Parameter Calculation/1-D Lookup Table1
  BreakpointsForDimension1 = n_vec
  InputPortMap = u0
  InternalRulePriority = Speed
  NumberOfTableDimensions = 1
  RndMeth = Simplest
  Table = optparam(:,4)
BLOCK [Outport] Vehicle Model/Thermisches Modell EM - LPTN/Parameter Calculation/R_r_e
  Port = 2
  VectorParamsAs1DForOutWhenUnconnected = off
BLOCK [Outport] Vehicle Model/Thermisches Modell EM - LPTN/Parameter Calculation/R_w_r
  VectorParamsAs1DForOutWhenUnconnected = off
BLOCK [Inport] Vehicle Model/Thermisches Modell EM - LPTN/Parameter Calculation/n //rpm
BLOCK [SubSystem] Vehicle Model/Thermisches Modell EM - LPTN/Subsystem1
BLOCK [Abs] Vehicle Model/Thermisches Modell EM - LPTN/Subsystem1/Abs
  SaturateOnIntegerOverflow = off
BLOCK [Lookup_n-D] Vehicle Model/Thermisches Modell EM - LPTN/Subsystem1/IronLosses
  BreakpointsForDimension1 = IronLosses.Torque
  BreakpointsForDimension2 = IronLosses.RotSpeed
  Commented = on
  InputPortMap = u0,u1
  InternalRulePriority = Speed
  RndMeth = Simplest
  Table = IronLosses.Losses
BLOCK [SubSystem] Vehicle Model/Thermisches Modell EM - LPTN/Subsystem1/MATLAB Function
  ErrorFcn = Stateflow.Translate.translate
  PermitHierarchicalResolution = ExplicitOnly
  SFBlockType = MATLAB Function
  TreatAsAtomicUnit = on
BLOCK [Demux] Vehicle Model/Thermisches Modell EM - LPTN/Subsystem1/MATLAB Function/ Demux 
  Outputs = 1
BLOCK [S-Function] Vehicle Model/Thermisches Modell EM - LPTN/Subsystem1/MATLAB Function/ SFunction 
  EnableBusSupport = off
  FunctionName = sf_sfun
  PortCounts = [2 2]
  SFcnIsStateOwnerBlock = off
  SFunctionDeploymentMode = off
  Tag = Stateflow S-Function 1
BLOCK [Terminator] Vehicle Model/Thermisches Modell EM - LPTN/Subsystem1/MATLAB Function/ Terminator 
BLOCK [Outport] Vehicle Model/Thermisches Modell EM - LPTN/Subsystem1/MATLAB Function/P_Iron_Mot
  VectorParamsAs1DForOutWhenUnconnected = off
BLOCK [Inport] Vehicle Model/Thermisches Modell EM - LPTN/Subsystem1/MATLAB Function/speed
BLOCK [Inport] Vehicle Model/Thermisches Modell EM - LPTN/Subsystem1/MATLAB Function/torque
  Port = 2
BLOCK [Outport] Vehicle Model/Thermisches Modell EM - LPTN/Subsystem1/iron loss
  VectorParamsAs1DForOutWhenUnconnected = off
BLOCK [Inport] Vehicle Model/Thermisches Modell EM - LPTN/Subsystem1/speed
  Port = 2
BLOCK [Inport] Vehicle Model/Thermisches Modell EM - LPTN/Subsystem1/torque
BLOCK [SubSystem] Vehicle Model/Thermisches Modell EM - LPTN/Subsystem2
BLOCK [Lookup_n-D] Vehicle Model/Thermisches Modell EM - LPTN/Subsystem2/FrictionLosses
  BreakpointsForDimension1 = Friction.Torque
  BreakpointsForDimension2 = Friction.RotSpeed
  Commented = on
  InputPortMap = u0,u1
  InternalRulePriority = Speed
  RndMeth = Simplest
  Table = Friction.Losses
BLOCK [SubSystem] Vehicle Model/Thermisches Modell EM - LPTN/Subsystem2/MATLAB Function
  ErrorFcn = Stateflow.Translate.translate
  PermitHierarchicalResolution = ExplicitOnly
  SFBlockType = MATLAB Function
  TreatAsAtomicUnit = on
BLOCK [Demux] Vehicle Model/Thermisches Modell EM - LPTN/Subsystem2/MATLAB Function/ Demux 
  Outputs = 1
BLOCK [S-Function] Vehicle Model/Thermisches Modell EM - LPTN/Subsystem2/MATLAB Function/ SFunction 
  EnableBusSupport = off
  FunctionName = sf_sfun
  PortCounts = [2 2]
  SFcnIsStateOwnerBlock = off
  SFunctionDeploymentMode = off
  Tag = Stateflow S-Function 3
BLOCK [Terminator] Vehicle Model/Thermisches Modell EM - LPTN/Subsystem2/MATLAB Function/ Terminator 
BLOCK [Outport] Vehicle Model/Thermisches Modell EM - LPTN/Subsystem2/MATLAB Function/P_Frict_Mot
  VectorParamsAs1DForOutWhenUnconnected = off
BLOCK [Inport] Vehicle Model/Thermisches Modell EM - LPTN/Subsystem2/MATLAB Function/speed
BLOCK [Inport] Vehicle Model/Thermisches Modell EM - LPTN/Subsystem2/MATLAB Function/torque
  Port = 2
BLOCK [Outport] Vehicle Model/Thermisches Modell EM - LPTN/Subsystem2/friction loss
  VectorParamsAs1DForOutWhenUnconnected = off
BLOCK [Inport] Vehicle Model/Thermisches Modell EM - LPTN/Subsystem2/speed
  Port = 2
BLOCK [Inport] Vehicle Model/Thermisches Modell EM - LPTN/Subsystem2/torque
BLOCK [SubSystem] Vehicle Model/Thermisches Modell EM - LPTN/Subsystem3
BLOCK [Abs] Vehicle Model/Thermisches Modell EM - LPTN/Subsystem3/Abs
  SaturateOnIntegerOverflow = off
BLOCK [Lookup_n-D] Vehicle Model/Thermisches Modell EM - LPTN/Subsystem3/CurrentLosses
  BreakpointsForDimension1 = CurrentLosses.Torque
  BreakpointsForDimension2 = CurrentLosses.RotSpeed
  Commented = on
  InputPortMap = u0,u1
  InternalRulePriority = Speed
  RndMeth = Simplest
  Table = CurrentLosses.Losses
BLOCK [SubSystem] Vehicle Model/Thermisches Modell EM - LPTN/Subsystem3/MATLAB Function
  ErrorFcn = Stateflow.Translate.translate
  PermitHierarchicalResolution = ExplicitOnly
  SFBlockType = MATLAB Function
  TreatAsAtomicUnit = on
BLOCK [Demux] Vehicle Model/Thermisches Modell EM - LPTN/Subsystem3/MATLAB Function/ Demux 
  Outputs = 1
BLOCK [S-Function] Vehicle Model/Thermisches Modell EM - LPTN/Subsystem3/MATLAB Function/ SFunction 
  EnableBusSupport = off
  FunctionName = sf_sfun
  PortCounts = [2 2]
  SFcnIsStateOwnerBlock = off
  SFunctionDeploymentMode = off
  Tag = Stateflow S-Function 5
BLOCK [Terminator] Vehicle Model/Thermisches Modell EM - LPTN/Subsystem3/MATLAB Function/ Terminator 
BLOCK [Outport] Vehicle Model/Thermisches Modell EM - LPTN/Subsystem3/MATLAB Function/P_Current_Mot
  VectorParamsAs1DForOutWhenUnconnected = off
BLOCK [Inport] Vehicle Model/Thermisches Modell EM - LPTN/Subsystem3/MATLAB Function/speed
BLOCK [Inport] Vehicle Model/Thermisches Modell EM - LPTN/Subsystem3/MATLAB Function/torque
  Port = 2
BLOCK [Outport] Vehicle Model/Thermisches Modell EM - LPTN/Subsystem3/iron loss
  VectorParamsAs1DForOutWhenUnconnected = off
BLOCK [Inport] Vehicle Model/Thermisches Modell EM - LPTN/Subsystem3/speed
  Port = 2
BLOCK [Inport] Vehicle Model/Thermisches Modell EM - LPTN/Subsystem3/torque
BLOCK [Sum] Vehicle Model/Thermisches Modell EM - LPTN/Sum
  Inputs = |++
BLOCK [Sum] Vehicle Model/Thermisches Modell EM - LPTN/Sum1
  Inputs = ++|
BLOCK [Sum] Vehicle Model/Thermisches Modell EM - LPTN/Sum5
  Inputs = |+-
BLOCK [Outport] Vehicle Model/Thermisches Modell EM - LPTN/Temperaturen_C
  VectorParamsAs1DForOutWhenUnconnected = off
BLOCK [Inport] Vehicle Model/Thermisches Modell EM - LPTN/Torque_Nm
  Port = 2
BLOCK [ToWorkspace] Vehicle Model/To Workspace
  FixptAsFi = on
  MaxDataPoints = inf
  SampleTime = -1
  Save2DSignal = 2-D array (concatenate along first dimension)
  VariableName = mpc_cmd_em_acc
BLOCK [ToWorkspace] Vehicle Model/To Workspace1
  FixptAsFi = on
  MaxDataPoints = inf
  SampleTime = -1
  Save2DSignal = 2-D array (concatenate along first dimension)
  VariableName = mpc_cmd_em_brake
BLOCK [ToWorkspace] Vehicle Model/To Workspace10
  Commented = on
  FixptAsFi = on
  MaxDataPoints = inf
  SampleTime = -1
  Save2DSignal = 2-D array (concatenate along first dimension)
  VariableName = T_w_LPTN
BLOCK [ToWorkspace] Vehicle Model/To Workspace11
  Commented = on
  FixptAsFi = on
  MaxDataPoints = inf
  SampleTime = -1
  Save2DSignal = 2-D array (concatenate along first dimension)
  VariableName = T_r_LPTN
BLOCK [ToWorkspace] Vehicle Model/To Workspace13
  FixptAsFi = on
  MaxDataPoints = inf
  SampleTime = -1
  Save2DSignal = 2-D array (concatenate along first dimension)
  VariableName = torque_sum
BLOCK [ToWorkspace] Vehicle Model/To Workspace14
  FixptAsFi = on
  MaxDataPoints = inf
  SampleTime = -1
  Save2DSignal = 2-D array (concatenate along first dimension)
  VariableName = mpc_cmd
BLOCK [ToWorkspace] Vehicle Model/To Workspace15
  Commented = on
  FixptAsFi = on
  MaxDataPoints = inf
  SampleTime = -1
  Save2DSignal = 2-D array (concatenate along first dimension)
  VariableName = T_w_Derivative
BLOCK [ToWorkspace] Vehicle Model/To Workspace16
  Commented = on
  FixptAsFi = on
  MaxDataPoints = inf
  SampleTime = -1
  Save2DSignal = 2-D array (concatenate along first dimension)
  VariableName = T_r_Derivative
BLOCK [ToWorkspace] Vehicle Model/To Workspace19
  FixptAsFi = on
  MaxDataPoints = inf
  SampleTime = -1
  Save2DSignal = 2-D array (concatenate along first dimension)
  VariableName = T_r_LSTM
BLOCK [ToWorkspace] Vehicle Model/To Workspace2
  FixptAsFi = on
  MaxDataPoints = inf
  SampleTime = -1
  Save2DSignal = 2-D array (concatenate along first dimension)
  VariableName = mpc_cmd_fr_brake
BLOCK [ToWorkspace] Vehicle Model/To Workspace22
  FixptAsFi = on
  MaxDataPoints = inf
  SampleTime = -1
  Save2DSignal = 2-D array (concatenate along first dimension)
  VariableName = T_w_LSTM
BLOCK [ToWorkspace] Vehicle Model/To Workspace3
  FixptAsFi = on
  MaxDataPoints = inf
  SampleTime = -1
  Save2DSignal = 2-D array (concatenate along first dimension)
  VariableName = driver_cmd
BLOCK [ToWorkspace] Vehicle Model/To Workspace4
  FixptAsFi = on
  MaxDataPoints = inf
  SampleTime = -1
  Save2DSignal = 2-D array (concatenate along first dimension)
  VariableName = torque_em
BLOCK [ToWorkspace] Vehicle Model/To Workspace5
  FixptAsFi = on
  MaxDataPoints = inf
  SampleTime = -1
  Save2DSignal = 2-D array (concatenate along first dimension)
  VariableName = torque_em_Ts
BLOCK [ToWorkspace] Vehicle Model/To Workspace6
  FixptAsFi = on
  MaxDataPoints = inf
  SampleTime = -1
  Save2DSignal = 2-D array (concatenate along first dimension)
  VariableName = torque_wheel
BLOCK [ToWorkspace] Vehicle Model/To Workspace7
  FixptAsFi = on
  MaxDataPoints = inf
  SampleTime = -1
  Save2DSignal = 2-D array (concatenate along first dimension)
  VariableName = v_des
BLOCK [ToWorkspace] Vehicle Model/To Workspace8
  FixptAsFi = on
  MaxDataPoints = inf
  SampleTime = -1
  Save2DSignal = 2-D array (concatenate along first dimension)
  VariableName = n_em
BLOCK [ToWorkspace] Vehicle Model/To Workspace9
  FixptAsFi = on
  MaxDataPoints = inf
  SampleTime = -1
  Save2DSignal = 2-D array (concatenate along first dimension)
  VariableName = n_em_Ts
BLOCK [Outport] Vehicle Model/Twr
  Port = 2
  PortDimensions = 2
  VectorParamsAs1DForOutWhenUnconnected = off
BLOCK [Concatenate] Vehicle Model/Vector Concatenate
BLOCK [Outport] Vehicle Model/a_ist
  Port = 4
  SampleTime = step_size
  VectorParamsAs1DForOutWhenUnconnected = off
BLOCK [Gain] Vehicle Model/driver_cmd
BLOCK [Gain] Vehicle Model/gear ratio
  Gain = FDR
BLOCK [Gain] Vehicle Model/mpc_cmd
BLOCK [Inport] Vehicle Model/mpc_cmd [-1...1]
  Port = 2
  PortDimensions = 3
BLOCK [Gain] Vehicle Model/n_em
BLOCK [Outport] Vehicle Model/s_ist
  Port = 3
  SampleTime = step_size
  VectorParamsAs1DForOutWhenUnconnected = off
BLOCK [SubSystem] Vehicle Model/torque interpreter ONLY MPC2
  NameLocation = top
BLOCK [Constant] Vehicle Model/torque interpreter ONLY MPC2/Constant
  Value = M_EM_acc_max
BLOCK [Constant] Vehicle Model/torque interpreter ONLY MPC2/Constant1
  Value = M_EM_brk_min
BLOCK [Constant] Vehicle Model/torque interpreter ONLY MPC2/Constant2
  Value = 0
BLOCK [Constant] Vehicle Model/torque interpreter ONLY MPC2/Constant3
  Value = torque_brake
BLOCK [Constant] Vehicle Model/torque interpreter ONLY MPC2/Constant5
  Value = 0
BLOCK [Demux] Vehicle Model/torque interpreter ONLY MPC2/Demux
  Outputs = 3
BLOCK [Display] Vehicle Model/torque interpreter ONLY MPC2/Display1
  Decimation = 1
BLOCK [Display] Vehicle Model/torque interpreter ONLY MPC2/Display10
  Decimation = 1
BLOCK [Display] Vehicle Model/torque interpreter ONLY MPC2/Display11
  Decimation = 1
BLOCK [Display] Vehicle Model/torque interpreter ONLY MPC2/Display12
  Decimation = 1
BLOCK [Display] Vehicle Model/torque interpreter ONLY MPC2/Display3
  Decimation = 1
BLOCK [Display] Vehicle Model/torque interpreter ONLY MPC2/Display4
  Decimation = 1
BLOCK [Display] Vehicle Model/torque interpreter ONLY MPC2/Display6
  Decimation = 1
BLOCK [Display] Vehicle Model/torque interpreter ONLY MPC2/Display8
  Decimation = 1
BLOCK [Display] Vehicle Model/torque interpreter ONLY MPC2/Display9
  Decimation = 1
BLOCK [Gain] Vehicle Model/torque interpreter ONLY MPC2/Gain1
  Gain = rps_rpm*FDR
BLOCK [Gain] Vehicle Model/torque interpreter ONLY MPC2/Gain3
  Gain = -1
BLOCK [Goto] Vehicle Model/torque interpreter ONLY MPC2/Goto
  GotoTag = torque_fric_brk
  TagVisibility = global
BLOCK [Goto] Vehicle Model/torque interpreter ONLY MPC2/Goto1
  GotoTag = torque_em_acc
  TagVisibility = global
BLOCK [Goto] Vehicle Model/torque interpreter ONLY MPC2/Goto2
  GotoTag = torque_em_brk
  TagVisibility = global
BLOCK [Product] Vehicle Model/torque interpreter ONLY MPC2/Product
BLOCK [Product] Vehicle Model/torque interpreter ONLY MPC2/Product2
BLOCK [Product] Vehicle Model/torque interpreter ONLY MPC2/Product3
BLOCK [Reference] Vehicle Model/torque interpreter ONLY MPC2/Saturation Dynamic  REF=simulink/Discontinuities/Saturation
Dynamic
  SourceBlock = simulink/Discontinuities/Saturation\nDynamic
  SourceType = Saturation Dynamic
BLOCK [Reference] Vehicle Model/torque interpreter ONLY MPC2/Saturation Dynamic1  REF=simulink/Discontinuities/Saturation
Dynamic
  SourceBlock = simulink/Discontinuities/Saturation\nDynamic
  SourceType = Saturation Dynamic
BLOCK [Sum] Vehicle Model/torque interpreter ONLY MPC2/Sum1
  IconShape = rectangular
BLOCK [Sum] Vehicle Model/torque interpreter ONLY MPC2/Sum4
  IconShape = rectangular
BLOCK [Terminator] Vehicle Model/torque interpreter ONLY MPC2/Terminator
BLOCK [ToWorkspace] Vehicle Model/torque interpreter ONLY MPC2/To Workspace
  FixptAsFi = on
  MaxDataPoints = inf
  SampleTime = -1
  Save2DSignal = 2-D array (concatenate along first dimension)
  VariableName = act_cmd_em_acc
BLOCK [ToWorkspace] Vehicle Model/torque interpreter ONLY MPC2/To Workspace2
  FixptAsFi = on
  MaxDataPoints = inf
  SampleTime = -1
  Save2DSignal = 2-D array (concatenate along first dimension)
  VariableName = act_cmd_fric_brake
BLOCK [ToWorkspace] Vehicle Model/torque interpreter ONLY MPC2/To Workspace3
  FixptAsFi = on
  MaxDataPoints = inf
  SampleTime = -1
  Save2DSignal = 2-D array (concatenate along first dimension)
  VariableName = act_cmd_em_brake
BLOCK [ToWorkspace] Vehicle Model/torque interpreter ONLY MPC2/To Workspace4
  FixptAsFi = on
  MaxDataPoints = inf
  SampleTime = -1
  Save2DSignal = 2-D array (concatenate along first dimension)
  VariableName = torque_em_acc
BLOCK [ToWorkspace] Vehicle Model/torque interpreter ONLY MPC2/To Workspace5
  FixptAsFi = on
  MaxDataPoints = inf
  SampleTime = -1
  Save2DSignal = 2-D array (concatenate along first dimension)
  VariableName = torque_em_brake
BLOCK [ToWorkspace] Vehicle Model/torque interpreter ONLY MPC2/To Workspace6
  FixptAsFi = on
  MaxDataPoints = inf
  SampleTime = -1
  Save2DSignal = 2-D array (concatenate along first dimension)
  VariableName = torque_frict_brake
BLOCK [ToWorkspace] Vehicle Model/torque interpreter ONLY MPC2/To Workspace7
  FixptAsFi = on
  MaxDataPoints = inf
  SampleTime = -1
  Save2DSignal = 2-D array (concatenate along first dimension)
  VariableName = act_cmd_fr_brake
BLOCK [Inport] Vehicle Model/torque interpreter ONLY MPC2/driver_cmd (-1,1)
  Port = 2
BLOCK [Gain] Vehicle Model/torque interpreter ONLY MPC2/m//s to mph1
  Gain = 1/r_dyn
  OutDataTypeStr = Inherit: Same as input
  ParamDataTypeStr = Inherit: Same as input
  SaturateOnIntegerOverflow = on
BLOCK [Lookup_n-D] Vehicle Model/torque interpreter ONLY MPC2/max gen torque lookup
  BreakpointsForDimension1 = n_gen_max
  InputPortMap = u0
  InternalRulePriority = Speed
  NumberOfTableDimensions = 1
  RndMeth = Simplest
  Table = M_gen_max
BLOCK [Lookup_n-D] Vehicle Model/torque interpreter ONLY MPC2/max mot torque lookup
  BreakpointsForDimension1 = n_mot_max
  InputPortMap = u0
  InternalRulePriority = Speed
  NumberOfTableDimensions = 1
  RndMeth = Simplest
  Table = M_mot_max
BLOCK [Inport] Vehicle Model/torque interpreter ONLY MPC2/mpc_cmd (-1,1)
  Port = 3
BLOCK [Outport] Vehicle Model/torque interpreter ONLY MPC2/torque
  VectorParamsAs1DForOutWhenUnconnected = off
BLOCK [Outport] Vehicle Model/torque interpreter ONLY MPC2/torque_em
  Port = 2
  VectorParamsAs1DForOutWhenUnconnected = off
BLOCK [Inport] Vehicle Model/torque interpreter ONLY MPC2/v m//s
BLOCK [Gain] Vehicle Model/torque_em
BLOCK [Gain] Vehicle Model/torque_sum
BLOCK [Gain] Vehicle Model/torque_wheel
BLOCK [Outport] Vehicle Model/v_out
  SampleTime = step_size
  VectorParamsAs1DForOutWhenUnconnected = off
BLOCK [SubSystem] Vehicle Model/vehicle
BLOCK [Gain] Vehicle Model/vehicle/Gain
  Gain = rps_rpm
BLOCK [Gain] Vehicle Model/vehicle/Grade resistance
  Gain = Mv*grav
  OutDataTypeStr = Inherit: Same as input
  ParamDataTypeStr = Inherit: Same as input
  SaturateOnIntegerOverflow = on
BLOCK [Math] Vehicle Model/vehicle/Impeller
  Operator = square
  SignedPower = on
BLOCK [Integrator] Vehicle Model/vehicle/Integrator
BLOCK [Gain] Vehicle Model/vehicle/Rolling resistance
  Gain = fr*Mv*grav
  OutDataTypeStr = Inherit: Same as input
  ParamDataTypeStr = Inherit: Same as input
  SaturateOnIntegerOverflow = on
BLOCK [Sum] Vehicle Model/vehicle/Sum2
  IconShape = rectangular
  InputSameDT = on
  Inputs = |+|-|-|-
  OutDataTypeStr = Inherit: Same as first input
  SaturateOnIntegerOverflow = on
BLOCK [ToWorkspace] Vehicle Model/vehicle/To Workspace1
  MaxDataPoints = inf
  SampleTime = -1
  VariableName = Dist
BLOCK [ToWorkspace] Vehicle Model/vehicle/To Workspace12
  FixptAsFi = on
  MaxDataPoints = 1
  SampleTime = -1
  Save2DSignal = 2-D array (concatenate along first dimension)
  VariableName = s_finish
BLOCK [ToWorkspace] Vehicle Model/vehicle/To Workspace2
  MaxDataPoints = inf
  SampleTime = -1
  VariableName = v_ist
BLOCK [ToWorkspace] Vehicle Model/vehicle/To Workspace3
  MaxDataPoints = inf
  SampleTime = -1
  VariableName = n_ist
BLOCK [ToWorkspace] Vehicle Model/vehicle/To Workspace4
  MaxDataPoints = inf
  SampleTime = -1
  VariableName = a_ist
BLOCK [ToWorkspace] Vehicle Model/vehicle/To Workspace5
  MaxDataPoints = inf
  SampleTime = -1
  VariableName = grade_ist
BLOCK [ToWorkspace] Vehicle Model/vehicle/To Workspace6
  MaxDataPoints = inf
  SampleTime = -1
  VariableName = s_ist
BLOCK [ToWorkspace] Vehicle Model/vehicle/To Workspace7
  FixptAsFi = on
  MaxDataPoints = inf
  SampleTime = -1
  Save2DSignal = 2-D array (concatenate along first dimension)
  VariableName = s_out
BLOCK [Trigonometry] Vehicle Model/vehicle/Trigonometric Function
  Operator = cos
BLOCK [Trigonometry] Vehicle Model/vehicle/Trigonometric Function1
BLOCK [Inport] Vehicle Model/vehicle/Tw
  Port = 2
BLOCK [Integrator] Vehicle Model/vehicle/V
  InitialCondition = v_0
  LimitOutput = on
  LowerSaturationLimit = 0
  UpperSaturationLimit = v_max * mps_kmh
BLOCK [Gain] Vehicle Model/vehicle/Vehicle Mass
  Gain = 1/Mv
  OutDataTypeStr = Inherit: Same as input
  ParamDataTypeStr = Inherit: Same as input
  SaturateOnIntegerOverflow = on
BLOCK [Outport] Vehicle Model/vehicle/a_ist
  InitialOutput = 0
  Port = 4
  VectorParamsAs1DForOutWhenUnconnected = off
BLOCK [Gain] Vehicle Model/vehicle/aerodynamic
  Gain = dens*Cd*Af/2
  OutDataTypeStr = Inherit: Same as input
  ParamDataTypeStr = Inherit: Same as input
  SaturateOnIntegerOverflow = on
BLOCK [Outport] Vehicle Model/vehicle/dist
  InitialOutput = 0
  Port = 2
  VectorParamsAs1DForOutWhenUnconnected = off
BLOCK [Gain] Vehicle Model/vehicle/gear ratio1
  Gain = FDR
BLOCK [Gain] Vehicle Model/vehicle/grade_ist
  Gain = pi/180
  OutDataTypeStr = Inherit: Same as input
  ParamDataTypeStr = Inherit: Same as input
  SaturateOnIntegerOverflow = on
BLOCK [Gain] Vehicle Model/vehicle/m//s to mph1
  Gain = 1/r_dyn
  OutDataTypeStr = Inherit: Same as input
  ParamDataTypeStr = Inherit: Same as input
  SaturateOnIntegerOverflow = on
BLOCK [Gain] Vehicle Model/vehicle/m//s to mph2
  Gain = 1/r_dyn
  OutDataTypeStr = Inherit: Same as input
  ParamDataTypeStr = Inherit: Same as input
  SaturateOnIntegerOverflow = on
BLOCK [Outport] Vehicle Model/vehicle/nm
  InitialOutput = 0
  Port = 3
  VectorParamsAs1DForOutWhenUnconnected = off
BLOCK [Inport] Vehicle Model/vehicle/s
BLOCK [Lookup_n-D] Vehicle Model/vehicle/track grade
  BreakpointsForDimension1 = s_track
  InputPortMap = u0
  InternalRulePriority = Speed
  NumberOfTableDimensions = 1
  RndMeth = Simplest
  Table = grade_track
BLOCK [Outport] Vehicle Model/vehicle/v (m//s)
  InitialOutput = 0
  VectorParamsAs1DForOutWhenUnconnected = off
BLOCK [Gain] Vehicle Model/vm_a_ist
BLOCK [Gain] Vehicle Model/vm_mpc_cmd
BLOCK [Gain] Vehicle Model/vm_s_ist
BLOCK [Gain] Vehicle Model/vm_s_ist_delayed
  NameLocation = top
BLOCK [Gain] Vehicle Model/vm_v_ist
BLOCK [SubSystem] mpc outout normalizaiton
BLOCK [Abs] mpc outout normalizaiton/Abs
  SaturateOnIntegerOverflow = off
BLOCK [Abs] mpc outout normalizaiton/Abs1
  SaturateOnIntegerOverflow = off
BLOCK [Constant] mpc outout normalizaiton/Constant
  Value = torque_brake
BLOCK [Constant] mpc outout normalizaiton/Constant3
  NameLocation = left
  Value = M_EM_acc_max
BLOCK [Constant] mpc outout normalizaiton/Constant4
  Value = M_EM_brk_min
BLOCK [Demux] mpc outout normalizaiton/Demux
  Outputs = 3
BLOCK [Demux] mpc outout normalizaiton/Demux1
  Outputs = 3
BLOCK [Display] mpc outout normalizaiton/Display1
  Decimation = 1
BLOCK [Display] mpc outout normalizaiton/Display2
  Decimation = 1
BLOCK [Display] mpc outout normalizaiton/Display3
  Decimation = 1
BLOCK [Display] mpc outout normalizaiton/Display4
  Decimation = 1
BLOCK [Display] mpc outout normalizaiton/Display5
  Decimation = 1
BLOCK [Display] mpc outout normalizaiton/Display6
  Decimation = 1
BLOCK [Display] mpc outout normalizaiton/Display7
  Decimation = 1
BLOCK [Product] mpc outout normalizaiton/Divide
  Inputs = */
BLOCK [Product] mpc outout normalizaiton/Divide1
  Inputs = */
BLOCK [Product] mpc outout normalizaiton/Divide2
  Inputs = */
BLOCK [Gain] mpc outout normalizaiton/Gain
  Gain = -1
BLOCK [Gain] mpc outout normalizaiton/Gain1
  Gain = rps_rpm*FDR
BLOCK [Mux] mpc outout normalizaiton/Mux
  DisplayOption = bar
  Inputs = 3
BLOCK [RateTransition] mpc outout normalizaiton/Rate Transition1
  OutPortSampleTime = step_size
BLOCK [RateTransition] mpc outout normalizaiton/Rate Transition5
  OutPortSampleTime = step_size
BLOCK [Saturate] mpc outout normalizaiton/Saturation
  LowerLimit = 0
  UpperLimit = 1
BLOCK [Saturate] mpc outout normalizaiton/Saturation1
  LowerLimit = -1
  UpperLimit = 0
BLOCK [Saturate] mpc outout normalizaiton/Saturation2
  LowerLimit = -1
  UpperLimit = 0
BLOCK [Terminator] mpc outout normalizaiton/Terminator
BLOCK [Terminator] mpc outout normalizaiton/Terminator1
BLOCK [Terminator] mpc outout normalizaiton/Terminator2
BLOCK [Terminator] mpc outout normalizaiton/Terminator3
BLOCK [ToWorkspace] mpc outout normalizaiton/To Workspace
  FixptAsFi = on
  MaxDataPoints = inf
  SampleTime = -1
  Save2DSignal = 2-D array (concatenate along first dimension)
  VariableName = torque_em_mot_max
BLOCK [ToWorkspace] mpc outout normalizaiton/To Workspace1
  FixptAsFi = on
  MaxDataPoints = inf
  SampleTime = -1
  Save2DSignal = 2-D array (concatenate along first dimension)
  VariableName = torque_em_gen_max
BLOCK [Gain] mpc outout normalizaiton/m//s to mph1
  Gain = 1/r_dyn
  OutDataTypeStr = Inherit: Same as input
  ParamDataTypeStr = Inherit: Same as input
  SaturateOnIntegerOverflow = on
BLOCK [Lookup_n-D] mpc outout normalizaiton/max gen torque lookup
  BreakpointsForDimension1 = n_gen_max
  InputPortMap = u0
  InternalRulePriority = Speed
  NumberOfTableDimensions = 1
  RndMeth = Simplest
  Table = M_gen_max
BLOCK [Lookup_n-D] mpc outout normalizaiton/max mot torque lookup
  BreakpointsForDimension1 = n_mot_max
  InputPortMap = u0
  InternalRulePriority = Speed
  NumberOfTableDimensions = 1
  RndMeth = Simplest
  Table = M_mot_max
BLOCK [Gain] mpc outout normalizaiton/mpc_cmd
BLOCK [Outport] mpc outout normalizaiton/mpc_output (acc, brake)
  VectorParamsAs1DForOutWhenUnconnected = off
BLOCK [Inport] mpc outout normalizaiton/mv
  Port = 2
BLOCK [Inport] mpc outout normalizaiton/ov
  PortDimensions = 3
BLOCK [SubSystem] uminmax
  NameLocation = top
BLOCK [Gain] uminmax/Gain1
  Gain = rps_rpm*FDR
BLOCK [Constant] uminmax/M_em,acc, max
  Value = 0
BLOCK [Constant] uminmax/M_em,acc, min
  Value = 0
BLOCK [Constant] uminmax/M_frict _brake max
  Value = 0
BLOCK [Constant] uminmax/M_frict _brake min
  Value = -torque_brake
BLOCK [Concatenate] uminmax/Matrix Concatenate
  ConcatenateDimension = 2
  Mode = Multidimensional array
  NumInputs = 3
BLOCK [Concatenate] uminmax/Matrix Concatenate1
  ConcatenateDimension = 2
  Mode = Multidimensional array
  NumInputs = 3
BLOCK [Product] uminmax/Product
BLOCK [Product] uminmax/Product1
BLOCK [Product] uminmax/Product2
BLOCK [Product] uminmax/Product3
BLOCK [Constant] uminmax/horizon1
  Value = ones(options.P,1)
BLOCK [Constant] uminmax/horizon2
  Value = ones(options.P,1)
BLOCK [Gain] uminmax/m//s to mph1
  Gain = 1/r_dyn
  OutDataTypeStr = Inherit: Same as input
  ParamDataTypeStr = Inherit: Same as input
  SaturateOnIntegerOverflow = on
BLOCK [Lookup_n-D] uminmax/max gen torque lookup
  BreakpointsForDimension1 = n_gen_max
  InputPortMap = u0
  InternalRulePriority = Speed
  NumberOfTableDimensions = 1
  RndMeth = Simplest
  Table = M_gen_max
BLOCK [Lookup_n-D] uminmax/max mot torque lookup
  BreakpointsForDimension1 = n_mot_max
  InputPortMap = u0
  InternalRulePriority = Speed
  NumberOfTableDimensions = 1
  RndMeth = Simplest
  Table = M_mot_max
BLOCK [Outport] uminmax/umax
  Port = 2
  VectorParamsAs1DForOutWhenUnconnected = off
BLOCK [Outport] uminmax/umin
  VectorParamsAs1DForOutWhenUnconnected = off
BLOCK [Inport] uminmax/v_preview (m//s)
ANNOTATION (root): Controller
ANNOTATION (root): Physical Plant
ANNOTATION (root): Race Analysis:
ANNOTATION (root): Trajectory prediction
ANNOTATION MPC: 1) T_w [K] 2) T_r [K] 3) v [m/s]
ANNOTATION MPC: gain_Twr
ANNOTATION MPC: Inputs are: 1) lbx_0 - lower bound on x for stage 0, size [19] 2) ubx_0 - upper bound on x for stage 0, size [19] 3) parameters - concatenated for all stages 0 to N, size [82] 4) y_ref_0 - size [4] 5) y_ref - concatenated for stages 1 to N-1, size [156] 6) y_ref_e - size [4] 7) lbx values concatenated for stages 1 to N-1, size [741] 8) ubx values concatenated for stages 1 to N-1, size [741] 9) lbx...<+499ch>
ANNOTATION MPC: Solver Status: 0) Success 1) Acados failure 2) Maximum number of iterations reached 3) Minimum step size in qp solver reached 4) QP solver failed
ANNOTATION MPC: for mpc variant with delta_controls
ANNOTATION MPC/Pred_Traj_and_costs_calc: 1) Tw 2) Tr 3) v 4) M_EM_Acc 5) dt_M_EM_acc 6) M_EM_brk 7) M_fric_brk 8) n_EM 9) P_EM 10) v - v_ref
ANNOTATION Save Block: Vehicle values
ANNOTATION State-Estimation/moving_horizon_estimator: Q0_mhe = 10 * diag([0.1, 0.1]); % weighting matrix of arrival cost Q_mhe = 0.1 * diag([0.2, 0.2]); % 0.1 % weighting matrix of states mid = ones(2,1); % PRanav R_mhe = 0.7 * diag(mid); weighting matrix of controls = noise
ANNOTATION State-Estimation/moving_horizon_estimator: Note: Usage of Sfunction is as follows: Inputs are: 1) lbx_0 - lower bound on x for stage 0, size [18] 2) ubx_0 - upper bound on x for stage 0, size [18] 3) parameters - concatenated for all shooting nodes 0 to N+1, size [80] 4) y_ref_0, size [6] % T_w, T_r, w_Tw, w_Tr, t_w, t_r (N:0) 5) y_ref - concatenated for shooting nodes 1 to N-1, size [56] T_w, T_r, w_Tw, w_Tr (N:14) 6) lbx for shooting nod...<+538ch>
ANNOTATION State-Estimation/moving_horizon_estimator: Outputs are: 1) u0, control input at node 0, size [2] 2) utraj, control input concatenated for nodes 0 to N-1, size [30] 3) xtraj, state concatenated for nodes 0 to N, size [288] 4) acados solver status (0 = SUCCESS) 5) cost function value 6) KKT residual 7) KKT residuals, size [4] (stat, eq, ineq, comp) 8) x1, state at node 1 9) CPU time 10) SQP iterations
ANNOTATION State-Estimation/moving_horizon_estimator: Q init = 0.001 * 0.2 R init = 0.6 Q0 init = 10
ANNOTATION State-Estimation/moving_horizon_estimator: The last set of values are the x estimates
ANNOTATION State-Estimation/moving_horizon_estimator: first Tw and Tr
ANNOTATION Vehicle Model: LPTN is from first publication, embedded winkler et al 2001
ANNOTATION Vehicle Model: Not included for confidentiality reason!
ANNOTATION Vehicle Model/Driver Model: source: Jinming Liu, Modeling, Configuration and control optimization of power split hybrid vehiclesm, Dissertation, 2007
ANNOTATION Vehicle Model/vehicle: Drive line + vehicle
ANNOTATION Vehicle Model/vehicle: Tire Speed
ANNOTATION Vehicle Model/vehicle: Vehicle Speed
LINE Clock1:1 -> Finish Time // s:1
LINE Distance Check/Distance Change Security Check/Constant1:1 -> Distance Check/Distance Change Security Check/MATLAB Function:4
LINE Distance Check/Distance Change Security Check/Constant:1 -> Distance Check/Distance Change Security Check/MATLAB Function:3
LINE Distance Check/Distance Change Security Check/MATLAB Function:1 -> Distance Check/Distance Change Security Check/bool_stop:1
LINE Distance Check/Distance Change Security Check/Memory:1 -> Distance Check/Distance Change Security Check/MATLAB Function:2
NET Distance Check/Distance Change Security Check/s:1 -> Distance Check/Distance Change Security Check/MATLAB Function:1, Distance Check/Distance Change Security Check/Memory:1
NET Distance Check/Distance Change Security Check:1 -> Distance Check/Stop Simulation:1, Distance Check/To Workspace24:1
LINE Distance Check/s (m):1 -> Distance Check/Distance Change Security Check:1
LINE Finish Line/Constant1:1 -> Finish Line/s>finish line:1
LINE Finish Line/Constant:1 -> Finish Line/s>finish line:3
LINE Finish Line/s (m):1 -> Finish Line/s_ist:1
LINE Finish Line/s>finish line:1 -> Finish Line/Stop Simulation:1
LINE Finish Line/s_ist:1 -> Finish Line/s>finish line:2
LINE From1:1 -> Display1:1
LINE From2:1 -> Display2:1
NET From3:1 -> Display3:1, Scope3:2
LINE From4:1 -> Rate Transition:1
LINE From5:1 -> Selector1:1
LINE From7:1 -> Display5:1
LINE From8:1 -> Display6:1
NET From:1 -> Display:1, Scope3:1
LINE MPC/Add:1 -> MPC/Multiply:1
LINE MPC/Clock:1 -> MPC/Display7:1
LINE MPC/Constant10:1 -> MPC/model_ubx_ac_e:1
LINE MPC/Constant11:1 -> MPC/MATLAB Function1:3
LINE MPC/Constant1:1 -> MPC/model_lbx_ac:1
LINE MPC/Constant2:1 -> MPC/model_ubx_ac:1
LINE MPC/Constant3:1 -> MPC/MATLAB Function:2
LINE MPC/Constant4:1 -> MPC/model_u_min:1
LINE MPC/Constant5:1 -> MPC/model_lh:1
LINE MPC/Constant6:1 -> MPC/MATLAB Function:3
LINE MPC/Constant8:1 -> MPC/model_lbx_ac_e:1
LINE MPC/Constant9:1 -> MPC/model_uh:1
LINE MPC/Constant:1 -> MPC/model_u_max:1
NET MPC/Demux1:1 -> MPC/Add:1, MPC/Display6:1
NET MPC/Demux1:2 -> MPC/Add:2, MPC/Display24:1
NET MPC/Demux1:3 -> MPC/Add:3, MPC/Display25:1
LINE MPC/Demux2:1 -> MPC/Mux2:1
LINE MPC/Demux2:2 -> MPC/Mux2:2
LINE MPC/Demux2:3 -> MPC/Mux2:3
LINE MPC/Demux:1 -> MPC/Mux1:1
LINE MPC/Demux:2 -> MPC/Mux1:2
NET MPC/Demux:3 -> MPC/Multiply:2, MPC/Mux1:3
LINE MPC/From10:1 -> MPC/Rate Transition3:1
LINE MPC/From11:1 -> MPC/Rate Transition4:1
LINE MPC/From1:1 -> MPC/Display8:1
LINE MPC/From2:1 -> MPC/Display11:1
LINE MPC/From3:1 -> MPC/Display12:1
NET MPC/From8:1 -> MPC/Display21:1, MPC/Mux:2
LINE MPC/From9:1 -> MPC/Rate Transition5:1
NET MPC/Gain1:1 -> MPC/Display18:1, MPC/To Workspace26:1
NET MPC/Gain:1 -> MPC/Goto2:1, MPC/MATLAB Function1:1, MPC/Scope1:1, MPC/To Workspace22:1
LINE MPC/Ground1:1 -> MPC/Pred_Traj_and_costs_calc:2
LINE MPC/Ground2:1 -> MPC/Pred_Traj_and_costs_calc:3
LINE MPC/Ground:1 -> MPC/Pred_Traj_and_costs_calc:1
LINE MPC/MATLAB Function1:1 -> MPC/model_p:1
LINE MPC/MATLAB Function:1 -> MPC/Selector2:1
LINE MPC/Memory:1 -> MPC/Goto:1
LINE MPC/Multiply:1 -> MPC/Gain1:1
NET MPC/Mux1:1 -> MPC/Display10:1, MPC/model_x_meas:1
NET MPC/Mux:1 -> MPC/S-Function:1, MPC/S-Function:2, MPC/To Workspace14:1
LINE MPC/Pred_Traj_and_costs_calc/Add:1 -> MPC/Pred_Traj_and_costs_calc/Multiply:2
NET MPC/Pred_Traj_and_costs_calc/Gain1:1 -> MPC/Pred_Traj_and_costs_calc/Display5:1, MPC/Pred_Traj_and_costs_calc/To Workspace:1
LINE MPC/Pred_Traj_and_costs_calc/Gain2:1 -> MPC/Pred_Traj_and_costs_calc/Display19:1
LINE MPC/Pred_Traj_and_costs_calc/Multiply:1 -> MPC/Pred_Traj_and_costs_calc/Gain1:1
LINE MPC/Pred_Traj_and_costs_calc/Selector10:1 -> MPC/Pred_Traj_and_costs_calc/To Workspace20:1
LINE MPC/Pred_Traj_and_costs_calc/Selector11:1 -> MPC/Pred_Traj_and_costs_calc/To Workspace21:1
LINE MPC/Pred_Traj_and_costs_calc/Selector12:1 -> MPC/Pred_Traj_and_costs_calc/To Workspace22:1
NET MPC/Pred_Traj_and_costs_calc/Selector13:1 -> MPC/Pred_Traj_and_costs_calc/Display4:1, MPC/Pred_Traj_and_costs_calc/Subsystem:4
NET MPC/Pred_Traj_and_costs_calc/Selector1:1 -> MPC/Pred_Traj_and_costs_calc/Add:2, MPC/Pred_Traj_and_costs_calc/Display1:1
NET MPC/Pred_Traj_and_costs_calc/Selector2:1 -> MPC/Pred_Traj_and_costs_calc/Add:3, MPC/Pred_Traj_and_costs_calc/Display2:1
NET MPC/Pred_Traj_and_costs_calc/Selector4:1 -> MPC/Pred_Traj_and_costs_calc/Display9:1, MPC/Pred_Traj_and_costs_calc/Selector10:1, MPC/Pred_Traj_and_costs_calc/To Workspace16:1
NET MPC/Pred_Traj_and_costs_calc/Selector5:1 -> MPC/Pred_Traj_and_costs_calc/Display3:1, MPC/Pred_Traj_and_costs_calc/Gain2:1, MPC/Pred_Traj_and_costs_calc/Multiply:1, MPC/Pred_Traj_and_costs_calc/Selector11:1, MPC/Pred_Traj_and_costs_calc/Subsystem:1, MPC/Pred_Traj_and_costs_calc/Subtract:1, MPC/Pred_Traj_and_costs_calc/To Workspace17:1
NET MPC/Pred_Traj_and_costs_calc/Selector7:1 -> MPC/Pred_Traj_and_costs_calc/Display15:1, MPC/Pred_Traj_and_costs_calc/Selector9:1, MPC/Pred_Traj_and_costs_calc/To Workspace23:1
NET MPC/Pred_Traj_and_costs_calc/Selector8:1 -> MPC/Pred_Traj_and_costs_calc/Add:1, MPC/Pred_Traj_and_costs_calc/Display16:1, MPC/Pred_Traj_and_costs_calc/Selector12:1, MPC/Pred_Traj_and_costs_calc/Subsystem:3, MPC/Pred_Traj_and_costs_calc/To Workspace18:1
LINE MPC/Pred_Traj_and_costs_calc/Selector9:1 -> MPC/Pred_Traj_and_costs_calc/To Workspace19:1
LINE MPC/Pred_Traj_and_costs_calc/Subsystem/Constant1:1 -> MPC/Pred_Traj_and_costs_calc/Subsystem/MATLAB Function:6
LINE MPC/Pred_Traj_and_costs_calc/Subsystem/Constant2:1 -> MPC/Pred_Traj_and_costs_calc/Subsystem/MATLAB Function:7
LINE MPC/Pred_Traj_and_costs_calc/Subsystem/Constant3:1 -> MPC/Pred_Traj_and_costs_calc/Subsystem/MATLAB Function:8
LINE MPC/Pred_Traj_and_costs_calc/Subsystem/Constant:1 -> MPC/Pred_Traj_and_costs_calc/Subsystem/MATLAB Function:5
LINE MPC/Pred_Traj_and_costs_calc/Subsystem/MATLAB Function:1 -> MPC/Pred_Traj_and_costs_calc/Subsystem/cost:1
LINE MPC/Pred_Traj_and_costs_calc/Subsystem/MATLAB Function:2 -> MPC/Pred_Traj_and_costs_calc/Subsystem/To Workspace:1
LINE MPC/Pred_Traj_and_costs_calc/Subsystem/MATLAB Function:3 -> MPC/Pred_Traj_and_costs_calc/Subsystem/To Workspace1:1
LINE MPC/Pred_Traj_and_costs_calc/Subsystem/MATLAB Function:4 -> MPC/Pred_Traj_and_costs_calc/Subsystem/To Workspace2:1
LINE MPC/Pred_Traj_and_costs_calc/Subsystem/MATLAB Function:5 -> MPC/Pred_Traj_and_costs_calc/Subsystem/To Workspace3:1
LINE MPC/Pred_Traj_and_costs_calc/Subsystem/dt_u:1 -> MPC/Pred_Traj_and_costs_calc/Subsystem/MATLAB Function:4
LINE MPC/Pred_Traj_and_costs_calc/Subsystem/u:1 -> MPC/Pred_Traj_and_costs_calc/Subsystem/MATLAB Function:3
LINE MPC/Pred_Traj_and_costs_calc/Subsystem/v:1 -> MPC/Pred_Traj_and_costs_calc/Subsystem/MATLAB Function:1
LINE MPC/Pred_Traj_and_costs_calc/Subsystem/v_ref:1 -> MPC/Pred_Traj_and_costs_calc/Subsystem/MATLAB Function:2
NET MPC/Pred_Traj_and_costs_calc/Subsystem:1 -> MPC/Pred_Traj_and_costs_calc/Costs:1, MPC/Pred_Traj_and_costs_calc/Display17:1
NET MPC/Pred_Traj_and_costs_calc/Subtract:1 -> MPC/Pred_Traj_and_costs_calc/Display6:1, MPC/Pred_Traj_and_costs_calc/To Workspace1:1
NET MPC/Pred_Traj_and_costs_calc/control_traj_pred:1 -> MPC/Pred_Traj_and_costs_calc/Selector13:1, MPC/Pred_Traj_and_costs_calc/Selector1:1, MPC/Pred_Traj_and_costs_calc/Selector2:1
NET MPC/Pred_Traj_and_costs_calc/state_traj_pred:1 -> MPC/Pred_Traj_and_costs_calc/Selector4:1, MPC/Pred_Traj_and_costs_calc/Selector5:1, MPC/Pred_Traj_and_costs_calc/Selector7:1, MPC/Pred_Traj_and_costs_calc/Selector8:1
NET MPC/Pred_Traj_and_costs_calc/v_ref:1 -> MPC/Pred_Traj_and_costs_calc/Subsystem:2, MPC/Pred_Traj_and_costs_calc/Subtract:2
NET MPC/Pred_Traj_and_costs_calc:1 -> MPC/Display3:1, MPC/To Workspace25:1
LINE MPC/Rate Transition3:1 -> MPC/Mux2:5
LINE MPC/Rate Transition4:1 -> MPC/Mux2:6
LINE MPC/Rate Transition5:1 -> MPC/Mux2:4
LINE MPC/Reshape:1 -> MPC/Selector6:1
NET MPC/S-Function:1 -> MPC/Demux1:1, MPC/Display17:1, MPC/Scope:1, MPC/To Workspace16:1, MPC/To Workspace30:1, MPC/To Workspace5:1, MPC/sol_controls:1
LINE MPC/S-Function:2 -> MPC/solver_status:1
LINE MPC/S-Function:3 -> MPC/solver_kkt_residuals:1
LINE MPC/S-Function:4 -> MPC/solver_first_state:1
LINE MPC/S-Function:5 -> MPC/solver_cpu_time:1
LINE MPC/S-Function:6 -> MPC/solver_sqp_iter:1
NET MPC/Selector11:1 -> MPC/S-Function:5, MPC/To Workspace7:1
NET MPC/Selector1:1 -> MPC/S-Function:6, MPC/To Workspace8:1
LINE MPC/Selector2:1 -> MPC/model_y_ref1:1
NET MPC/Selector5:1 -> MPC/S-Function:4, MPC/To Workspace17:1
NET MPC/Selector6:1 -> MPC/MATLAB Function1:2, MPC/MATLAB Function:1, MPC/Scope1:2, MPC/To Workspace:1
LINE MPC/Selector7:1 -> MPC/Memory:1
NET MPC/Selector8:1 -> MPC/S-Function:3, MPC/To Workspace9:1
NET MPC/Selector:1 -> MPC/To Workspace3:1, MPC/solver_control_opti:1
LINE MPC/SolverStop/Clock:1 -> MPC/SolverStop/Switch:2
LINE MPC/SolverStop/Constant:1 -> MPC/SolverStop/Switch:3
LINE MPC/SolverStop/MATLAB Function:1 -> MPC/SolverStop/bool_stop:1
LINE MPC/SolverStop/Switch:1 -> MPC/SolverStop/MATLAB Function:1
LINE MPC/SolverStop/solver_status:1 -> MPC/SolverStop/Switch:1
LINE MPC/SolverStop:1 -> MPC/To Workspace24:1
NET MPC/model_lbx_ac:1 -> MPC/S-Function:7, MPC/To Workspace10:1
NET MPC/model_lbx_ac_e:1 -> MPC/S-Function:9, MPC/To Workspace18:1
NET MPC/model_lh:1 -> MPC/S-Function:13, MPC/To Workspace20:1
LINE MPC/model_p:1 -> MPC/Selector8:1
NET MPC/model_u_max:1 -> MPC/S-Function:12, MPC/To Workspace13:1
NET MPC/model_u_min:1 -> MPC/S-Function:11, MPC/To Workspace12:1
NET MPC/model_ubx_ac:1 -> MPC/S-Function:8, MPC/To Workspace11:1
NET MPC/model_ubx_ac_e:1 -> MPC/S-Function:10, MPC/To Workspace19:1
NET MPC/model_uh:1 -> MPC/S-Function:14, MPC/To Workspace21:1
LINE MPC/model_x_meas:1 -> MPC/Mux:1
NET MPC/model_y_ref1:1 -> MPC/Selector11:1, MPC/Selector1:1, MPC/Selector5:1
LINE MPC/phi:1 -> MPC/Gain:1
LINE MPC/solver_control_opti:1 -> MPC/Terminator:1
NET MPC/solver_cpu_time:1 -> MPC/Display4:1, MPC/To Workspace4:1
NET MPC/solver_first_state:1 -> MPC/Selector7:1, MPC/Selector:1, MPC/To Workspace23:1
NET MPC/solver_kkt_residuals:1 -> MPC/Display2:1, MPC/To Workspace2:1
NET MPC/solver_sqp_iter:1 -> MPC/Display5:1, MPC/To Workspace6:1
NET MPC/solver_status:1 -> MPC/Display:1, MPC/Goto3:1, MPC/SolverStop:1, MPC/To Workspace1:1
LINE MPC/x_meas:1 -> MPC/Demux:1
LINE MPC/x_ref:1 -> MPC/Reshape:1
LINE MPC:1 -> mpc outout normalizaiton:2
LINE Noise_Sensors/AND1:1 -> Noise_Sensors/Switch1:2
LINE Noise_Sensors/AND:1 -> Noise_Sensors/Switch:2
LINE Noise_Sensors/Add1:1 -> Noise_Sensors/Add:2
LINE Noise_Sensors/Add:1 -> Noise_Sensors/Rate Transition:1
NET Noise_Sensors/Clock:1 -> Noise_Sensors/GreaterThan1:1, Noise_Sensors/GreaterThan2:1, Noise_Sensors/GreaterThan3:1, Noise_Sensors/GreaterThan:1
LINE Noise_Sensors/Constant1:1 -> Noise_Sensors/Switch:1
LINE Noise_Sensors/Constant2:1 -> Noise_Sensors/Switch:3
LINE Noise_Sensors/Constant3:1 -> Noise_Sensors/GreaterThan1:2
LINE Noise_Sensors/Constant4:1 -> Noise_Sensors/GreaterThan2:2
LINE Noise_Sensors/Constant7:1 -> Noise_Sensors/GreaterThan3:2
LINE Noise_Sensors/Constant:1 -> Noise_Sensors/GreaterThan:2
LINE Noise_Sensors/GreaterThan1:1 -> Noise_Sensors/AND:2
LINE Noise_Sensors/GreaterThan2:1 -> Noise_Sensors/AND1:1
LINE Noise_Sensors/GreaterThan3:1 -> Noise_Sensors/AND1:2
LINE Noise_Sensors/GreaterThan:1 -> Noise_Sensors/AND:1
LINE Noise_Sensors/Ground:1 -> Noise_Sensors/Add1:1
LINE Noise_Sensors/Random Number3:1 -> Noise_Sensors/Switch1:3
LINE Noise_Sensors/Random Number:1 -> Noise_Sensors/Switch1:1
NET Noise_Sensors/Rate Transition:1 -> Noise_Sensors/Goto:1, Noise_Sensors/Noisy_temp:1
LINE Noise_Sensors/Switch1:1 -> Noise_Sensors/Add1:3
LINE Noise_Sensors/Switch:1 -> Noise_Sensors/Add1:2
LINE Noise_Sensors/Twr_LSTM:1 -> Noise_Sensors/LSTM_temp:1
NET Noise_Sensors/Twr_orig:1 -> Noise_Sensors/Add:1, Noise_Sensors/Orig_temp:1
LINE Noise_Sensors:1 -> State-Estimation:1
LINE Noise_Sensors:2 -> State-Estimation:2
LINE Noise_Sensors:3 -> State-Estimation:3
LINE Rate Transition1:1 -> MPC:2
LINE Rate Transition2:1 -> MPC:3
LINE Rate Transition3:1 -> Noise_Sensors:1
LINE Rate Transition4:1 -> uminmax:1
LINE Rate Transition5:1 -> Vehicle Model:2
LINE Rate Transition6:1 -> State-Estimation:4
LINE Rate Transition7:1 -> Vehicle Model:1
LINE Rate Transition8:1 -> Noise_Sensors:2
LINE Rate Transition:1 -> Scope3:4
LINE Reference Trajectory/Clock:1 -> Reference Trajectory/sim_time:1
LINE Reference Trajectory/Constant1:1 -> Reference Trajectory/Matrix Concatenate:1
LINE Reference Trajectory/Delay:1 -> Reference Trajectory/distance preview:7
LINE Reference Trajectory/Matrix Concatenate:1 -> Reference Trajectory/y_ref_vector:1
LINE Reference Trajectory/Memory:1 -> Reference Trajectory/Selector:1
LINE Reference Trajectory/Mux:1 -> Reference Trajectory/phi_prev_vector:1
LINE Reference Trajectory/Referenze:1 -> Reference Trajectory/v_track:1
LINE Reference Trajectory/Selector:1 -> Reference Trajectory/Mux:1
NET Reference Trajectory/Track speed :1 -> Reference Trajectory/Delay:1, Reference Trajectory/Matrix Concatenate:2, Reference Trajectory/To Workspace:1, Reference Trajectory/v_prev:1
LINE Reference Trajectory/a_ist:1 -> Reference Trajectory/distance preview:3
NET Reference Trajectory/a_prev:1 -> Reference Trajectory/Terminator:1, Reference Trajectory/To Workspace2:1
NET Reference Trajectory/distance preview:1 -> Reference Trajectory/Track speed :1, Reference Trajectory/track grade:1
LINE Reference Trajectory/distance preview:2 -> Reference Trajectory/a_prev:1
LINE Reference Trajectory/horizon1:1 -> Reference Trajectory/distance preview:6
LINE Reference Trajectory/horizon3:1 -> Reference Trajectory/distance preview:8
LINE Reference Trajectory/horizon:1 -> Reference Trajectory/distance preview:5
NET Reference Trajectory/phi_prev_vector:1 -> Reference Trajectory/To Workspace1:1, Reference Trajectory/phi_prev:1
NET Reference Trajectory/s:1 -> Reference Trajectory/Referenze:1, Reference Trajectory/distance preview:2
LINE Reference Trajectory/sample time mpc:1 -> Reference Trajectory/distance preview:4
LINE Reference Trajectory/sim_time:1 -> Reference Trajectory/distance preview:9
NET Reference Trajectory/track grade:1 -> Reference Trajectory/Memory:1, Reference Trajectory/Mux:2
LINE Reference Trajectory/v_ist:1 -> Reference Trajectory/distance preview:1
LINE Reference Trajectory/v_track:1 -> Reference Trajectory/v_ref:1
LINE Reference Trajectory/y_ref_vector:1 -> Reference Trajectory/y_ref:1
LINE Reference Trajectory:1 -> Rate Transition1:1
LINE Reference Trajectory:2 -> Rate Transition2:1
LINE Reference Trajectory:3 -> Rate Transition7:1
LINE Reference Trajectory:4 -> Rate Transition4:1
NET Save Block/Clock:1 -> Save Block/To Workspace11:1, Save Block/To Workspace13:1
LINE Save Block/Demux1:1 -> Save Block/To Workspace3:1
LINE Save Block/Demux1:2 -> Save Block/To Workspace4:1
LINE Save Block/Demux2:1 -> Save Block/To Workspace5:1
LINE Save Block/Demux2:2 -> Save Block/To Workspace6:1
NET Save Block/Demux:1 -> Save Block/Rate Transition6:1, Save Block/To Workspace7:1
NET Save Block/Demux:2 -> Save Block/Rate Transition1:1, Save Block/To Workspace8:1
NET Save Block/Energy calculation1/Abs1:1 -> Save Block/Energy calculation1/Display1:1, Save Block/Energy calculation1/Divide:1
LINE Save Block/Energy calculation1/Abs2:1 -> Save Block/Energy calculation1/Divide:2
LINE Save Block/Energy calculation1/Abs3:1 -> Save Block/Energy calculation1/Gain7:1
LINE Save Block/Energy calculation1/Abs6:1 -> Save Block/Energy calculation1/Gain8:1
LINE Save Block/Energy calculation1/Abs:1 -> Save Block/Energy calculation1/Product:2
LINE Save Block/Energy calculation1/Constant1:1 -> Save Block/Energy calculation1/Switch1:3
LINE Save Block/Energy calculation1/Constant3:1 -> Save Block/Energy calculation1/Divide2:2
LINE Save Block/Energy calculation1/Constant:1 -> Save Block/Energy calculation1/Switch:1
LINE Save Block/Energy calculation1/Divide1:1 -> Save Block/Energy calculation1/Integrator2:1
LINE Save Block/Energy calculation1/Divide2:1 -> Save Block/Energy calculation1/Switch3:3
LINE Save Block/Energy calculation1/Divide:1 -> Save Block/Energy calculation1/Product1:2
LINE Save Block/Energy calculation1/EM efficiency1:1 -> Save Block/Energy calculation1/Gain6:1
LINE Save Block/Energy calculation1/EM efficiency2:1 -> Save Block/Energy calculation1/Abs6:1
LINE Save Block/Energy calculation1/EM efficiency:1 -> Save Block/Energy calculation1/Abs3:1
NET Save Block/Energy calculation1/From1:1 -> Save Block/Energy calculation1/Switch1:1, Save Block/Energy calculation1/Switch1:2
NET Save Block/Energy calculation1/From29:1 -> Save Block/Energy calculation1/Divide1:1, Save Block/Energy calculation1/EM efficiency2:1, Save Block/Energy calculation1/Scope1:1, Save Block/Energy calculation1/Switch3:2, Save Block/Energy calculation1/Switch:2, Save Block/Energy calculation1/Switch:3
NET Save Block/Energy calculation1/From2:1 -> Save Block/Energy calculation1/EM efficiency1:2, Save Block/Energy calculation1/Gain3:1
NET Save Block/Energy calculation1/From30:1 -> Save Block/Energy calculation1/EM efficiency:2, Save Block/Energy calculation1/Gain1:1
NET Save Block/Energy calculation1/From3:1 -> Save Block/Energy calculation1/EM efficiency2:2, Save Block/Energy calculation1/Gain5:1
LINE Save Block/Energy calculation1/Gain1:1 -> Save Block/Energy calculation1/Product:3
LINE Save Block/Energy calculation1/Gain2:1 -> Save Block/Energy calculation1/E_used:1
NET Save Block/Energy calculation1/Gain3:1 -> Save Block/Energy calculation1/Display2:1, Save Block/Energy calculation1/Product1:1
LINE Save Block/Energy calculation1/Gain4:1 -> Save Block/Energy calculation1/E_delta:1
LINE Save Block/Energy calculation1/Gain5:1 -> Save Block/Energy calculation1/Divide1:3
NET Save Block/Energy calculation1/Gain6:1 -> Save Block/Energy calculation1/Abs2:1, Save Block/Energy calculation1/Display:1
LINE Save Block/Energy calculation1/Gain7:1 -> Save Block/Energy calculation1/Product:1
NET Save Block/Energy calculation1/Gain8:1 -> Save Block/Energy calculation1/Divide2:1, Save Block/Energy calculation1/Switch3:1
LINE Save Block/Energy calculation1/Gain:1 -> Save Block/Energy calculation1/E_rekup:1
LINE Save Block/Energy calculation1/Integrator1:1 -> Save Block/Energy calculation1/Gain2:1
LINE Save Block/Energy calculation1/Integrator2:1 -> Save Block/Energy calculation1/Gain4:1
LINE Save Block/Energy calculation1/Integrator:1 -> Save Block/Energy calculation1/Gain:1
LINE Save Block/Energy calculation1/Product1:1 -> Save Block/Energy calculation1/Integrator1:1
LINE Save Block/Energy calculation1/Product:1 -> Save Block/Energy calculation1/Integrator:1
NET Save Block/Energy calculation1/Switch1:1 -> Save Block/Energy calculation1/Abs1:1, Save Block/Energy calculation1/EM efficiency1:1, Save Block/Energy calculation1/Scope1:2
LINE Save Block/Energy calculation1/Switch3:1 -> Save Block/Energy calculation1/Divide1:2
NET Save Block/Energy calculation1/Switch:1 -> Save Block/Energy calculation1/Abs:1, Save Block/Energy calculation1/EM efficiency:1
LINE Save Block/Energy calculation1:1 -> Save Block/s_ref15:1
LINE Save Block/Energy calculation1:2 -> Save Block/s_ref12:1
LINE Save Block/Energy calculation1:3 -> Save Block/s_ref16:1
NET Save Block/From1:1 -> Save Block/Rate Transition2:1, Save Block/To Workspace20:1
LINE Save Block/From2:1 -> Save Block/Selector1:1
LINE Save Block/From3:1 -> Save Block/Demux2:1
LINE Save Block/From6:1 -> Save Block/Demux:1
LINE Save Block/Rate Transition1:1 -> Save Block/To Workspace2:1
LINE Save Block/Rate Transition2:1 -> Save Block/To Workspace:1
LINE Save Block/Rate Transition6:1 -> Save Block/To Workspace1:1
LINE Save Block/Selector1:1 -> Save Block/Demux1:1
NET Selector1:1 -> Display7:1, Scope3:3
LINE State-Estimation/Constant2:1 -> State-Estimation/Multiport Switch:1
LINE State-Estimation/LSTM_temp:1 -> State-Estimation/Terminator1:1
LINE State-Estimation/Multiport Switch:1 -> State-Estimation/Output:1
LINE State-Estimation/Mux4:1 -> State-Estimation/Multiport Switch:2
LINE State-Estimation/Mux7:1 -> State-Estimation/Multiport Switch:3
NET State-Estimation/Velocity:1 -> State-Estimation/Mux4:2, State-Estimation/Mux7:2, State-Estimation/moving_horizon_estimator:2
LINE State-Estimation/moving_horizon_estimator/Buffer1:1 -> State-Estimation/moving_horizon_estimator/Reshape2:1
LINE State-Estimation/moving_horizon_estimator/Buffer2:1 -> State-Estimation/moving_horizon_estimator/Reshape1:1
LINE State-Estimation/moving_horizon_estimator/Constant1:1 -> State-Estimation/moving_horizon_estimator/S-Function:6
LINE State-Estimation/moving_horizon_estimator/Constant2:1 -> State-Estimation/moving_horizon_estimator/S-Function:7
NET State-Estimation/moving_horizon_estimator/Constant4:1 -> State-Estimation/moving_horizon_estimator/Gain:1, State-Estimation/moving_horizon_estimator/S-Function:9
NET State-Estimation/moving_horizon_estimator/Constant:1 -> State-Estimation/moving_horizon_estimator/Demux2:1, State-Estimation/moving_horizon_estimator/Mux:2
LINE State-Estimation/moving_horizon_estimator/Create Diagonal Matrix1:1 -> State-Estimation/moving_horizon_estimator/Reshape4:1
LINE State-Estimation/moving_horizon_estimator/Create Diagonal Matrix:1 -> State-Estimation/moving_horizon_estimator/Reshape3:1
NET State-Estimation/moving_horizon_estimator/Delay1:1 -> State-Estimation/moving_horizon_estimator/S-Function:1, State-Estimation/moving_horizon_estimator/S-Function:2
LINE State-Estimation/moving_horizon_estimator/Delay2:1 -> State-Estimation/moving_horizon_estimator/Mux:3
LINE State-Estimation/moving_horizon_estimator/Delay3:1 -> State-Estimation/moving_horizon_estimator/Mux2:1
LINE State-Estimation/moving_horizon_estimator/Delay:1 -> State-Estimation/moving_horizon_estimator/Mux2:2
LINE State-Estimation/moving_horizon_estimator/Demux1:1 -> State-Estimation/moving_horizon_estimator/To Workspace:1
LINE State-Estimation/moving_horizon_estimator/Demux1:2 -> State-Estimation/moving_horizon_estimator/To Workspace1:1
LINE State-Estimation/moving_horizon_estimator/Demux2:1 -> State-Estimation/moving_horizon_estimator/Mux2:3
LINE State-Estimation/moving_horizon_estimator/Demux2:2 -> State-Estimation/moving_horizon_estimator/Mux2:4
NET State-Estimation/moving_horizon_estimator/Demux:1 -> State-Estimation/moving_horizon_estimator/Delay3:1, State-Estimation/moving_horizon_estimator/Vector Concatenate:1
NET State-Estimation/moving_horizon_estimator/Demux:2 -> State-Estimation/moving_horizon_estimator/Delay:1, State-Estimation/moving_horizon_estimator/Vector Concatenate:2
LINE State-Estimation/moving_horizon_estimator/From1:1 -> State-Estimation/moving_horizon_estimator/Rate Transition1:1
LINE State-Estimation/moving_horizon_estimator/From5:1 -> State-Estimation/moving_horizon_estimator/Rate Transition:1
LINE State-Estimation/moving_horizon_estimator/From6:1 -> State-Estimation/moving_horizon_estimator/Rate Transition2:1
LINE State-Estimation/moving_horizon_estimator/From:1 -> State-Estimation/moving_horizon_estimator/Selector:1
LINE State-Estimation/moving_horizon_estimator/Gain:1 -> State-Estimation/moving_horizon_estimator/S-Function:8
NET State-Estimation/moving_horizon_estimator/Mux1:1 -> State-Estimation/moving_horizon_estimator/Buffer1:1, State-Estimation/moving_horizon_estimator/Display:1
LINE State-Estimation/moving_horizon_estimator/Mux2:1 -> State-Estimation/moving_horizon_estimator/Buffer2:1
LINE State-Estimation/moving_horizon_estimator/Mux:1 -> State-Estimation/moving_horizon_estimator/S-Function:4
LINE State-Estimation/moving_horizon_estimator/Q0:1 -> State-Estimation/moving_horizon_estimator/Vector Concatenate1:3
NET State-Estimation/moving_horizon_estimator/Q:1 -> State-Estimation/moving_horizon_estimator/Vector Concatenate1:1, State-Estimation/moving_horizon_estimator/Vector Concatenate2:1
NET State-Estimation/moving_horizon_estimator/R:1 -> State-Estimation/moving_horizon_estimator/Vector Concatenate1:2, State-Estimation/moving_horizon_estimator/Vector Concatenate2:2
LINE State-Estimation/moving_horizon_estimator/Rate Transition1:1 -> State-Estimation/moving_horizon_estimator/Mux1:2
LINE State-Estimation/moving_horizon_estimator/Rate Transition2:1 -> State-Estimation/moving_horizon_estimator/Mux1:3
LINE State-Estimation/moving_horizon_estimator/Rate Transition:1 -> State-Estimation/moving_horizon_estimator/Mux1:1
LINE State-Estimation/moving_horizon_estimator/Reshape1:1 -> State-Estimation/moving_horizon_estimator/S-Function:5
LINE State-Estimation/moving_horizon_estimator/Reshape2:1 -> State-Estimation/moving_horizon_estimator/S-Function:3
LINE State-Estimation/moving_horizon_estimator/Reshape3:1 -> State-Estimation/moving_horizon_estimator/S-Function:10
LINE State-Estimation/moving_horizon_estimator/Reshape4:1 -> State-Estimation/moving_horizon_estimator/S-Function:11
LINE State-Estimation/moving_horizon_estimator/S-Function:1 -> State-Estimation/moving_horizon_estimator/u0:1
LINE State-Estimation/moving_horizon_estimator/S-Function:10 -> State-Estimation/moving_horizon_estimator/solver_sqp_iter:1
NET State-Estimation/moving_horizon_estimator/S-Function:2 -> State-Estimation/moving_horizon_estimator/Display1:1, State-Estimation/moving_horizon_estimator/Selector6:1
LINE State-Estimation/moving_horizon_estimator/S-Function:3 -> State-Estimation/moving_horizon_estimator/Selector4:1
NET State-Estimation/moving_horizon_estimator/S-Function:4 -> State-Estimation/moving_horizon_estimator/Goto2:1, State-Estimation/moving_horizon_estimator/Solver status:1
LINE State-Estimation/moving_horizon_estimator/S-Function:5 -> State-Estimation/moving_horizon_estimator/Cost value:1
LINE State-Estimation/moving_horizon_estimator/S-Function:6 -> State-Estimation/moving_horizon_estimator/KKT residual:1
LINE State-Estimation/moving_horizon_estimator/S-Function:7 -> State-Estimation/moving_horizon_estimator/KKT residuals (4x):1
NET State-Estimation/moving_horizon_estimator/S-Function:8 -> State-Estimation/moving_horizon_estimator/Delay1:1, State-Estimation/moving_horizon_estimator/Selector3:1
LINE State-Estimation/moving_horizon_estimator/S-Function:9 -> State-Estimation/moving_horizon_estimator/solver_cpu_time:1
LINE State-Estimation/moving_horizon_estimator/Selector3:1 -> State-Estimation/moving_horizon_estimator/Delay2:1
NET State-Estimation/moving_horizon_estimator/Selector4:1 -> State-Estimation/moving_horizon_estimator/Goto1:1, State-Estimation/moving_horizon_estimator/Selector5:1
NET State-Estimation/moving_horizon_estimator/Selector5:1 -> State-Estimation/moving_horizon_estimator/Display5:1, State-Estimation/moving_horizon_estimator/Output:1
LINE State-Estimation/moving_horizon_estimator/Selector6:1 -> State-Estimation/moving_horizon_estimator/Selector7:1
LINE State-Estimation/moving_horizon_estimator/Selector7:1 -> State-Estimation/moving_horizon_estimator/Demux1:1
LINE State-Estimation/moving_horizon_estimator/Selector:1 -> State-Estimation/moving_horizon_estimator/Mux1:4
LINE State-Estimation/moving_horizon_estimator/Vector Concatenate1:1 -> State-Estimation/moving_horizon_estimator/Create Diagonal Matrix:1
LINE State-Estimation/moving_horizon_estimator/Vector Concatenate2:1 -> State-Estimation/moving_horizon_estimator/Create Diagonal Matrix1:1
LINE State-Estimation/moving_horizon_estimator/Vector Concatenate:1 -> State-Estimation/moving_horizon_estimator/Mux:1
LINE State-Estimation/moving_horizon_estimator/Velocity:1 -> State-Estimation/moving_horizon_estimator/Mux1:5
LINE State-Estimation/moving_horizon_estimator/noisy_temp:1 -> State-Estimation/moving_horizon_estimator/Demux:1
LINE State-Estimation/moving_horizon_estimator:1 -> State-Estimation/Mux4:1
LINE State-Estimation/noisy_temp:1 -> State-Estimation/moving_horizon_estimator:1
LINE State-Estimation/orig_temp:1 -> State-Estimation/Mux7:1
NET State-Estimation:1 -> MPC:1, mpc outout normalizaiton:1
NET Vehicle Model/ v_des (m//s):1 -> Vehicle Model/Driver Model:2, Vehicle Model/Goto3:1, Vehicle Model/To Workspace7:1
LINE Vehicle Model/Clock:1 -> Vehicle Model/Switch:2
LINE Vehicle Model/Constant1:1 -> Vehicle Model/Switch:3
LINE Vehicle Model/Demux1:1 -> Vehicle Model/To Workspace10:1
LINE Vehicle Model/Demux1:2 -> Vehicle Model/To Workspace11:1
LINE Vehicle Model/Demux3:1 -> Vehicle Model/To Workspace15:1
LINE Vehicle Model/Demux3:2 -> Vehicle Model/To Workspace16:1
LINE Vehicle Model/Demux:1 -> Vehicle Model/To Workspace:1
LINE Vehicle Model/Demux:2 -> Vehicle Model/To Workspace1:1
LINE Vehicle Model/Demux:3 -> Vehicle Model/To Workspace2:1
LINE Vehicle Model/Discrete Derivative:1 -> Vehicle Model/Rate Transition6:1
NET Vehicle Model/Driver Model/-1 to 1 :1 -> Vehicle Model/Driver Model/Sum5:2, Vehicle Model/Driver Model/driver_cmd:1
LINE Vehicle Model/Driver Model/1//Ti_c:1 -> Vehicle Model/Driver Model/Sum8:1
LINE Vehicle Model/Driver Model/1//Tt_c:1 -> Vehicle Model/Driver Model/Sum8:2
LINE Vehicle Model/Driver Model/Integrator1:1 -> Vehicle Model/Driver Model/Sum1:2
NET Vehicle Model/Driver Model/Kp_c:1 -> Vehicle Model/Driver Model/1//Ti_c:1, Vehicle Model/Driver Model/Sum1:1
LINE Vehicle Model/Driver Model/Normalize1:1 -> Vehicle Model/Driver Model/Sum7:2
LINE Vehicle Model/Driver Model/Normalize:1 -> Vehicle Model/Driver Model/Sum7:1
NET Vehicle Model/Driver Model/Sum1:1 -> Vehicle Model/Driver Model/-1 to 1 :1, Vehicle Model/Driver Model/Sum5:1
LINE Vehicle Model/Driver Model/Sum5:1 -> Vehicle Model/Driver Model/1//Tt_c:1
LINE Vehicle Model/Driver Model/Sum7:1 -> Vehicle Model/Driver Model/Kp_c:1
LINE Vehicle Model/Driver Model/Sum8:1 -> Vehicle Model/Driver Model/Integrator1:1
LINE Vehicle Model/Driver Model/v_des (km//h):1 -> Vehicle Model/Driver Model/Normalize:1
LINE Vehicle Model/Driver Model/v_veh (km//h):1 -> Vehicle Model/Driver Model/Normalize1:1
LINE Vehicle Model/Driver Model:1 -> Vehicle Model/driver_cmd:1
LINE Vehicle Model/LSTM-Based Thermal Model grad/Constant3:1 -> Vehicle Model/LSTM-Based Thermal Model grad/Sum2:2
NET Vehicle Model/LSTM-Based Thermal Model grad/Constant4:1 -> Vehicle Model/LSTM-Based Thermal Model grad/Sum3:1, Vehicle Model/LSTM-Based Thermal Model grad/Sum4:1
LINE Vehicle Model/LSTM-Based Thermal Model grad/Delay:1 -> Vehicle Model/LSTM-Based Thermal Model grad/Demux4:1
NET Vehicle Model/LSTM-Based Thermal Model grad/Demux4:1 -> Vehicle Model/LSTM-Based Thermal Model grad/Sum3:2, Vehicle Model/LSTM-Based Thermal Model grad/T_w_LSTM [°C]:1
NET Vehicle Model/LSTM-Based Thermal Model grad/Demux4:2 -> Vehicle Model/LSTM-Based Thermal Model grad/Sum4:2, Vehicle Model/LSTM-Based Thermal Model grad/T_r_LSTM [°C]:1
LINE Vehicle Model/LSTM-Based Thermal Model grad/Discrete-Time Integrator:1 -> Vehicle Model/LSTM-Based Thermal Model grad/Delay:1
LINE Vehicle Model/LSTM-Based Thermal Model grad/From1:1 -> Vehicle Model/LSTM-Based Thermal Model grad/Demux5:1
LINE Vehicle Model/LSTM-Based Thermal Model grad/Gain2:1 -> Vehicle Model/LSTM-Based Thermal Model grad/Mux:1
LINE Vehicle Model/LSTM-Based Thermal Model grad/Gain3:1 -> Vehicle Model/LSTM-Based Thermal Model grad/Mux:2
LINE Vehicle Model/LSTM-Based Thermal Model grad/Gain6:1 -> Vehicle Model/LSTM-Based Thermal Model grad/Sum2:1
LINE Vehicle Model/LSTM-Based Thermal Model grad/Gain7:1 -> Vehicle Model/LSTM-Based Thermal Model grad/Mux:3
LINE Vehicle Model/LSTM-Based Thermal Model grad/Gain8:1 -> Vehicle Model/LSTM-Based Thermal Model grad/Mux:4
LINE Vehicle Model/LSTM-Based Thermal Model grad/Mux:1 -> Vehicle Model/LSTM-Based Thermal Model grad/Reshape:1
NET Vehicle Model/LSTM-Based Thermal Model grad/Reshape:1 -> Vehicle Model/LSTM-Based Thermal Model grad/Stateful Predict:1, Vehicle Model/LSTM-Based Thermal Model grad/To Workspace17:1
LINE Vehicle Model/LSTM-Based Thermal Model grad/Rotational_Speed [rpm]:1 -> Vehicle Model/LSTM-Based Thermal Model grad/Gain2:1
LINE Vehicle Model/LSTM-Based Thermal Model grad/Stateful Predict:1 -> Vehicle Model/LSTM-Based Thermal Model grad/Gain6:1
NET Vehicle Model/LSTM-Based Thermal Model grad/Sum2:1 -> Vehicle Model/LSTM-Based Thermal Model grad/Discrete-Time Integrator:1, Vehicle Model/LSTM-Based Thermal Model grad/To Workspace18:1
LINE Vehicle Model/LSTM-Based Thermal Model grad/Sum3:1 -> Vehicle Model/LSTM-Based Thermal Model grad/Gain7:1
LINE Vehicle Model/LSTM-Based Thermal Model grad/Sum4:1 -> Vehicle Model/LSTM-Based Thermal Model grad/Gain8:1
LINE Vehicle Model/LSTM-Based Thermal Model grad/Torque_EM [Nm]:1 -> Vehicle Model/LSTM-Based Thermal Model grad/Gain3:1
LINE Vehicle Model/LSTM-Based Thermal Model grad:1 -> Vehicle Model/Rate Transition9:1
LINE Vehicle Model/LSTM-Based Thermal Model grad:2 -> Vehicle Model/Rate Transition11:1
LINE Vehicle Model/Memory:1 -> Vehicle Model/vm_s_ist_delayed:1
LINE Vehicle Model/Mux1:1 -> Vehicle Model/Goto7:1
NET Vehicle Model/Mux:1 -> Vehicle Model/Discrete Derivative:1, Vehicle Model/Rate Transition5:1
LINE Vehicle Model/Rate Transition10:1 -> Vehicle Model/To Workspace9:1
NET Vehicle Model/Rate Transition11:1 -> Vehicle Model/Mux1:2, Vehicle Model/Mux:2, Vehicle Model/To Workspace19:1, Vehicle Model/Vector Concatenate:2
LINE Vehicle Model/Rate Transition1:1 -> Vehicle Model/To Workspace5:1
NET Vehicle Model/Rate Transition2:1 -> Vehicle Model/Rate Transition3:1, Vehicle Model/Thermisches Modell EM - LPTN:2
LINE Vehicle Model/Rate Transition3:1 -> Vehicle Model/LSTM-Based Thermal Model grad:2
NET Vehicle Model/Rate Transition4:1 -> Vehicle Model/Rate Transition7:1, Vehicle Model/Thermisches Modell EM - LPTN:1
LINE Vehicle Model/Rate Transition5:1 -> Vehicle Model/T_wr_gain:1
LINE Vehicle Model/Rate Transition6:1 -> Vehicle Model/Demux3:1
LINE Vehicle Model/Rate Transition7:1 -> Vehicle Model/LSTM-Based Thermal Model grad:1
NET Vehicle Model/Rate Transition9:1 -> Vehicle Model/Mux1:1, Vehicle Model/Mux:1, Vehicle Model/To Workspace22:1, Vehicle Model/Vector Concatenate:1
NET Vehicle Model/Switch:1 -> Vehicle Model/Demux:1, Vehicle Model/mpc_cmd:1
NET Vehicle Model/T_wr_gain:1 -> Vehicle Model/Goto:1, Vehicle Model/Twr:1
NET Vehicle Model/Thermal Model DENSO/Ground:1 -> Vehicle Model/Thermal Model DENSO/T_wr:1, Vehicle Model/Thermal Model DENSO/T_wr_muxed:1
LINE Vehicle Model/Thermal Model DENSO/SpeedIn :1 -> Vehicle Model/Thermal Model DENSO/Terminator1:1
LINE Vehicle Model/Thermal Model DENSO/TorqueIn:1 -> Vehicle Model/Thermal Model DENSO/Terminator:1
LINE Vehicle Model/Thermisches Modell EM - LPTN/Abs:1 -> Vehicle Model/Thermisches Modell EM - LPTN/Mux:1
LINE Vehicle Model/Thermisches Modell EM - LPTN/Coolant Temp:1 -> Vehicle Model/Thermisches Modell EM - LPTN/Mux1:3
LINE Vehicle Model/Thermisches Modell EM - LPTN/Demux1:1 -> Vehicle Model/Thermisches Modell EM - LPTN/Subsystem1:1
LINE Vehicle Model/Thermisches Modell EM - LPTN/Demux1:2 -> Vehicle Model/Thermisches Modell EM - LPTN/Subsystem1:2
LINE Vehicle Model/Thermisches Modell EM - LPTN/Demux2:1 -> Vehicle Model/Thermisches Modell EM - LPTN/Subsystem2:1
LINE Vehicle Model/Thermisches Modell EM - LPTN/Demux2:2 -> Vehicle Model/Thermisches Modell EM - LPTN/Subsystem2:2
LINE Vehicle Model/Thermisches Modell EM - LPTN/Demux:1 -> Vehicle Model/Thermisches Modell EM - LPTN/Subsystem3:1
LINE Vehicle Model/Thermisches Modell EM - LPTN/Demux:2 -> Vehicle Model/Thermisches Modell EM - LPTN/Subsystem3:2
LINE Vehicle Model/Thermisches Modell EM - LPTN/Drehzahl_rpm:1 -> Vehicle Model/Thermisches Modell EM - LPTN/Mux:2
LINE Vehicle Model/Thermisches Modell EM - LPTN/Environment Temp:1 -> Vehicle Model/Thermisches Modell EM - LPTN/Mux1:4
LINE Vehicle Model/Thermisches Modell EM - LPTN/Gain1:1 -> Vehicle Model/Thermisches Modell EM - LPTN/Sum:2
LINE Vehicle Model/Thermisches Modell EM - LPTN/Gain2:1 -> Vehicle Model/Thermisches Modell EM - LPTN/Sum1:1
LINE Vehicle Model/Thermisches Modell EM - LPTN/K->C:1 -> Vehicle Model/Thermisches Modell EM - LPTN/Sum5:2
LINE Vehicle Model/Thermisches Modell EM - LPTN/LPTN Model /1:Pw 2: Pr 3:Tc  4:Te:1 -> Vehicle Model/Thermisches Modell EM - LPTN/LPTN Model /Demux:1
LINE Vehicle Model/Thermisches Modell EM - LPTN/LPTN Model /Constant1:1 -> Vehicle Model/Thermisches Modell EM - LPTN/LPTN Model /Divide1:2
LINE Vehicle Model/Thermisches Modell EM - LPTN/LPTN Model /Constant2:1 -> Vehicle Model/Thermisches Modell EM - LPTN/LPTN Model /Divide2:2
LINE Vehicle Model/Thermisches Modell EM - LPTN/LPTN Model /Constant:1 -> Vehicle Model/Thermisches Modell EM - LPTN/LPTN Model /Divide:2
LINE Vehicle Model/Thermisches Modell EM - LPTN/LPTN Model /Demux:1 -> Vehicle Model/Thermisches Modell EM - LPTN/LPTN Model /Sum:1
LINE Vehicle Model/Thermisches Modell EM - LPTN/LPTN Model /Demux:2 -> Vehicle Model/Thermisches Modell EM - LPTN/LPTN Model /Sum9:1
LINE Vehicle Model/Thermisches Modell EM - LPTN/LPTN Model /Demux:3 -> Vehicle Model/Thermisches Modell EM - LPTN/LPTN Model /Sum1:2
NET Vehicle Model/Thermisches Modell EM - LPTN/LPTN Model /Demux:4 -> Vehicle Model/Thermisches Modell EM - LPTN/LPTN Model /Sum3:2, Vehicle Model/Thermisches Modell EM - LPTN/LPTN Model /Sum7:2
LINE Vehicle Model/Thermisches Modell EM - LPTN/LPTN Model /Divide1:1 -> Vehicle Model/Thermisches Modell EM - LPTN/LPTN Model /Sum6:1
LINE Vehicle Model/Thermisches Modell EM - LPTN/LPTN Model /Divide2:1 -> Vehicle Model/Thermisches Modell EM - LPTN/LPTN Model /Sum6:2
LINE Vehicle Model/Thermisches Modell EM - LPTN/LPTN Model /Divide:1 -> Vehicle Model/Thermisches Modell EM - LPTN/LPTN Model /Sum2:1
NET Vehicle Model/Thermisches Modell EM - LPTN/LPTN Model /Integrator2:1 -> Vehicle Model/Thermisches Modell EM - LPTN/LPTN Model /Mux:2, Vehicle Model/Thermisches Modell EM - LPTN/LPTN Model /Sum4:2, Vehicle Model/Thermisches Modell EM - LPTN/LPTN Model /Sum5:1, Vehicle Model/Thermisches Modell EM - LPTN/LPTN Model /Sum7:1
NET Vehicle Model/Thermisches Modell EM - LPTN/LPTN Model /Integrator:1 -> Vehicle Model/Thermisches Modell EM - LPTN/LPTN Model /Mux:1, Vehicle Model/Thermisches Modell EM - LPTN/LPTN Model /Sum1:1, Vehicle Model/Thermisches Modell EM - LPTN/LPTN Model /Sum3:1, Vehicle Model/Thermisches Modell EM - LPTN/LPTN Model /Sum4:1, Vehicle Model/Thermisches Modell EM - LPTN/LPTN Model /Sum5:2
LINE Vehicle Model/Thermisches Modell EM - LPTN/LPTN Model /Mux:1 -> Vehicle Model/Thermisches Modell EM - LPTN/LPTN Model /1:Tw, 2:Tr:1
LINE Vehicle Model/Thermisches Modell EM - LPTN/LPTN Model /Sum1:1 -> Vehicle Model/Thermisches Modell EM - LPTN/LPTN Model /gain4:1
LINE Vehicle Model/Thermisches Modell EM - LPTN/LPTN Model /Sum2:1 -> Vehicle Model/Thermisches Modell EM - LPTN/LPTN Model /Sum:2
LINE Vehicle Model/Thermisches Modell EM - LPTN/LPTN Model /Sum3:1 -> Vehicle Model/Thermisches Modell EM - LPTN/LPTN Model /gain3:1
LINE Vehicle Model/Thermisches Modell EM - LPTN/LPTN Model /Sum4:1 -> Vehicle Model/Thermisches Modell EM - LPTN/LPTN Model /Divide:1
LINE Vehicle Model/Thermisches Modell EM - LPTN/LPTN Model /Sum5:1 -> Vehicle Model/Thermisches Modell EM - LPTN/LPTN Model /Divide1:1
LINE Vehicle Model/Thermisches Modell EM - LPTN/LPTN Model /Sum6:1 -> Vehicle Model/Thermisches Modell EM - LPTN/LPTN Model /Sum9:2
LINE Vehicle Model/Thermisches Modell EM - LPTN/LPTN Model /Sum7:1 -> Vehicle Model/Thermisches Modell EM - LPTN/LPTN Model /Divide2:1
LINE Vehicle Model/Thermisches Modell EM - LPTN/LPTN Model /Sum9:1 -> Vehicle Model/Thermisches Modell EM - LPTN/LPTN Model /gain1:1
LINE Vehicle Model/Thermisches Modell EM - LPTN/LPTN Model /Sum:1 -> Vehicle Model/Thermisches Modell EM - LPTN/LPTN Model /gain:1
LINE Vehicle Model/Thermisches Modell EM - LPTN/LPTN Model /gain1:1 -> Vehicle Model/Thermisches Modell EM - LPTN/LPTN Model /Integrator2:1
LINE Vehicle Model/Thermisches Modell EM - LPTN/LPTN Model /gain3:1 -> Vehicle Model/Thermisches Modell EM - LPTN/LPTN Model /Sum2:2
LINE Vehicle Model/Thermisches Modell EM - LPTN/LPTN Model /gain4:1 -> Vehicle Model/Thermisches Modell EM - LPTN/LPTN Model /Sum2:3
LINE Vehicle Model/Thermisches Modell EM - LPTN/LPTN Model /gain:1 -> Vehicle Model/Thermisches Modell EM - LPTN/LPTN Model /Integrator:1
LINE Vehicle Model/Thermisches Modell EM - LPTN/LPTN Model :1 -> Vehicle Model/Thermisches Modell EM - LPTN/Sum5:1
LINE Vehicle Model/Thermisches Modell EM - LPTN/Mux1:1 -> Vehicle Model/Thermisches Modell EM - LPTN/LPTN Model :1
NET Vehicle Model/Thermisches Modell EM - LPTN/Mux:1 -> Vehicle Model/Thermisches Modell EM - LPTN/Demux1:1, Vehicle Model/Thermisches Modell EM - LPTN/Demux2:1, Vehicle Model/Thermisches Modell EM - LPTN/Demux:1
LINE Vehicle Model/Thermisches Modell EM - LPTN/Parameter Calculation/1-D Lookup Table1:1 -> Vehicle Model/Thermisches Modell EM - LPTN/Parameter Calculation/R_r_e:1
LINE Vehicle Model/Thermisches Modell EM - LPTN/Parameter Calculation/1-D Lookup Table:1 -> Vehicle Model/Thermisches Modell EM - LPTN/Parameter Calculation/R_w_r:1
NET Vehicle Model/Thermisches Modell EM - LPTN/Parameter Calculation/n //rpm:1 -> Vehicle Model/Thermisches Modell EM - LPTN/Parameter Calculation/1-D Lookup Table1:1, Vehicle Model/Thermisches Modell EM - LPTN/Parameter Calculation/1-D Lookup Table:1
LINE Vehicle Model/Thermisches Modell EM - LPTN/Parameter Calculation:1 -> Vehicle Model/Thermisches Modell EM - LPTN/Goto:1
LINE Vehicle Model/Thermisches Modell EM - LPTN/Parameter Calculation:2 -> Vehicle Model/Thermisches Modell EM - LPTN/Goto1:1
LINE Vehicle Model/Thermisches Modell EM - LPTN/Subsystem1/Abs:1 -> Vehicle Model/Thermisches Modell EM - LPTN/Subsystem1/MATLAB Function:2
LINE Vehicle Model/Thermisches Modell EM - LPTN/Subsystem1/MATLAB Function:1 -> Vehicle Model/Thermisches Modell EM - LPTN/Subsystem1/iron loss:1
LINE Vehicle Model/Thermisches Modell EM - LPTN/Subsystem1/speed:1 -> Vehicle Model/Thermisches Modell EM - LPTN/Subsystem1/MATLAB Function:1
LINE Vehicle Model/Thermisches Modell EM - LPTN/Subsystem1/torque:1 -> Vehicle Model/Thermisches Modell EM - LPTN/Subsystem1/Abs:1
NET Vehicle Model/Thermisches Modell EM - LPTN/Subsystem1:1 -> Vehicle Model/Thermisches Modell EM - LPTN/Gain1:1, Vehicle Model/Thermisches Modell EM - LPTN/Gain2:1
LINE Vehicle Model/Thermisches Modell EM - LPTN/Subsystem2/MATLAB Function:1 -> Vehicle Model/Thermisches Modell EM - LPTN/Subsystem2/friction loss:1
LINE Vehicle Model/Thermisches Modell EM - LPTN/Subsystem2/speed:1 -> Vehicle Model/Thermisches Modell EM - LPTN/Subsystem2/MATLAB Function:1
LINE Vehicle Model/Thermisches Modell EM - LPTN/Subsystem2/torque:1 -> Vehicle Model/Thermisches Modell EM - LPTN/Subsystem2/MATLAB Function:2
LINE Vehicle Model/Thermisches Modell EM - LPTN/Subsystem2:1 -> Vehicle Model/Thermisches Modell EM - LPTN/Sum1:2
LINE Vehicle Model/Thermisches Modell EM - LPTN/Subsystem3/Abs:1 -> Vehicle Model/Thermisches Modell EM - LPTN/Subsystem3/MATLAB Function:2
LINE Vehicle Model/Thermisches Modell EM - LPTN/Subsystem3/MATLAB Function:1 -> Vehicle Model/Thermisches Modell EM - LPTN/Subsystem3/iron loss:1
LINE Vehicle Model/Thermisches Modell EM - LPTN/Subsystem3/speed:1 -> Vehicle Model/Thermisches Modell EM - LPTN/Subsystem3/MATLAB Function:1
LINE Vehicle Model/Thermisches Modell EM - LPTN/Subsystem3/torque:1 -> Vehicle Model/Thermisches Modell EM - LPTN/Subsystem3/Abs:1
LINE Vehicle Model/Thermisches Modell EM - LPTN/Subsystem3:1 -> Vehicle Model/Thermisches Modell EM - LPTN/Sum:1
NET Vehicle Model/Thermisches Modell EM - LPTN/Sum1:1 -> Vehicle Model/Thermisches Modell EM - LPTN/Display1:1, Vehicle Model/Thermisches Modell EM - LPTN/Mux1:2
NET Vehicle Model/Thermisches Modell EM - LPTN/Sum5:1 -> Vehicle Model/Thermisches Modell EM - LPTN/Display2:1, Vehicle Model/Thermisches Modell EM - LPTN/Temperaturen_C:1
NET Vehicle Model/Thermisches Modell EM - LPTN/Sum:1 -> Vehicle Model/Thermisches Modell EM - LPTN/Display:1, Vehicle Model/Thermisches Modell EM - LPTN/Mux1:1
LINE Vehicle Model/Thermisches Modell EM - LPTN/Torque_Nm:1 -> Vehicle Model/Thermisches Modell EM - LPTN/Abs:1
NET Vehicle Model/Thermisches Modell EM - LPTN:1 -> Vehicle Model/Demux1:1, Vehicle Model/Goto5:1
LINE Vehicle Model/Vector Concatenate:1 -> Vehicle Model/T_wr_LSTM:1
NET Vehicle Model/driver_cmd:1 -> Vehicle Model/To Workspace3:1, Vehicle Model/torque interpreter ONLY MPC2:2
NET Vehicle Model/gear ratio:1 -> Vehicle Model/To Workspace6:1, Vehicle Model/torque_wheel:1
LINE Vehicle Model/mpc_cmd [-1...1]:1 -> Vehicle Model/vm_mpc_cmd:1
NET Vehicle Model/mpc_cmd:1 -> Vehicle Model/To Workspace14:1, Vehicle Model/torque interpreter ONLY MPC2:3
LINE Vehicle Model/n_em:1 -> Vehicle Model/Rate Transition4:1
LINE Vehicle Model/torque interpreter ONLY MPC2/Constant1:1 -> Vehicle Model/torque interpreter ONLY MPC2/Product:2
LINE Vehicle Model/torque interpreter ONLY MPC2/Constant2:1 -> Vehicle Model/torque interpreter ONLY MPC2/Saturation Dynamic1:3
LINE Vehicle Model/torque interpreter ONLY MPC2/Constant3:1 -> Vehicle Model/torque interpreter ONLY MPC2/Product2:1
LINE Vehicle Model/torque interpreter ONLY MPC2/Constant5:1 -> Vehicle Model/torque interpreter ONLY MPC2/Saturation Dynamic:1
LINE Vehicle Model/torque interpreter ONLY MPC2/Constant:1 -> Vehicle Model/torque interpreter ONLY MPC2/Product3:2
NET Vehicle Model/torque interpreter ONLY MPC2/Demux:1 -> Vehicle Model/torque interpreter ONLY MPC2/Product3:1, Vehicle Model/torque interpreter ONLY MPC2/To Workspace:1
NET Vehicle Model/torque interpreter ONLY MPC2/Demux:2 -> Vehicle Model/torque interpreter ONLY MPC2/Product:1, Vehicle Model/torque interpreter ONLY MPC2/To Workspace3:1
NET Vehicle Model/torque interpreter ONLY MPC2/Demux:3 -> Vehicle Model/torque interpreter ONLY MPC2/Product2:2, Vehicle Model/torque interpreter ONLY MPC2/To Workspace2:1, Vehicle Model/torque interpreter ONLY MPC2/To Workspace7:1
NET Vehicle Model/torque interpreter ONLY MPC2/Gain1:1 -> Vehicle Model/torque interpreter ONLY MPC2/max gen torque lookup:1, Vehicle Model/torque interpreter ONLY MPC2/max mot torque lookup:1
NET Vehicle Model/torque interpreter ONLY MPC2/Gain3:1 -> Vehicle Model/torque interpreter ONLY MPC2/Display1:1, Vehicle Model/torque interpreter ONLY MPC2/Saturation Dynamic:2
NET Vehicle Model/torque interpreter ONLY MPC2/Product2:1 -> Vehicle Model/torque interpreter ONLY MPC2/Display12:1, Vehicle Model/torque interpreter ONLY MPC2/Goto:1, Vehicle Model/torque interpreter ONLY MPC2/Sum1:1, Vehicle Model/torque interpreter ONLY MPC2/To Workspace6:1
NET Vehicle Model/torque interpreter ONLY MPC2/Product3:1 -> Vehicle Model/torque interpreter ONLY MPC2/Display6:1, Vehicle Model/torque interpreter ONLY MPC2/Saturation Dynamic1:2
LINE Vehicle Model/torque interpreter ONLY MPC2/Product:1 -> Vehicle Model/torque interpreter ONLY MPC2/Gain3:1
NET Vehicle Model/torque interpreter ONLY MPC2/Saturation Dynamic1:1 -> Vehicle Model/torque interpreter ONLY MPC2/Display11:1, Vehicle Model/torque interpreter ONLY MPC2/Goto1:1, Vehicle Model/torque interpreter ONLY MPC2/Sum4:1, Vehicle Model/torque interpreter ONLY MPC2/To Workspace4:1
NET Vehicle Model/torque interpreter ONLY MPC2/Saturation Dynamic:1 -> Vehicle Model/torque interpreter ONLY MPC2/Display10:1, Vehicle Model/torque interpreter ONLY MPC2/Goto2:1, Vehicle Model/torque interpreter ONLY MPC2/Sum4:2, Vehicle Model/torque interpreter ONLY MPC2/To Workspace5:1
NET Vehicle Model/torque interpreter ONLY MPC2/Sum1:1 -> Vehicle Model/torque interpreter ONLY MPC2/Display3:1, Vehicle Model/torque interpreter ONLY MPC2/torque:1
NET Vehicle Model/torque interpreter ONLY MPC2/Sum4:1 -> Vehicle Model/torque interpreter ONLY MPC2/Display4:1, Vehicle Model/torque interpreter ONLY MPC2/Sum1:2, Vehicle Model/torque interpreter ONLY MPC2/torque_em:1
LINE Vehicle Model/torque interpreter ONLY MPC2/driver_cmd (-1,1):1 -> Vehicle Model/torque interpreter ONLY MPC2/Terminator:1
LINE Vehicle Model/torque interpreter ONLY MPC2/m//s to mph1:1 -> Vehicle Model/torque interpreter ONLY MPC2/Gain1:1
NET Vehicle Model/torque interpreter ONLY MPC2/max gen torque lookup:1 -> Vehicle Model/torque interpreter ONLY MPC2/Display8:1, Vehicle Model/torque interpreter ONLY MPC2/Saturation Dynamic:3
NET Vehicle Model/torque interpreter ONLY MPC2/max mot torque lookup:1 -> Vehicle Model/torque interpreter ONLY MPC2/Display9:1, Vehicle Model/torque interpreter ONLY MPC2/Saturation Dynamic1:1
LINE Vehicle Model/torque interpreter ONLY MPC2/mpc_cmd (-1,1):1 -> Vehicle Model/torque interpreter ONLY MPC2/Demux:1
LINE Vehicle Model/torque interpreter ONLY MPC2/v m//s:1 -> Vehicle Model/torque interpreter ONLY MPC2/m//s to mph1:1
LINE Vehicle Model/torque interpreter ONLY MPC2:1 -> Vehicle Model/torque_sum:1
NET Vehicle Model/torque interpreter ONLY MPC2:2 -> Vehicle Model/Goto2:1, Vehicle Model/Rate Transition1:1, Vehicle Model/To Workspace4:1, Vehicle Model/torque_em:1
LINE Vehicle Model/torque_em:1 -> Vehicle Model/Rate Transition2:1
NET Vehicle Model/torque_sum:1 -> Vehicle Model/To Workspace13:1, Vehicle Model/gear ratio:1
LINE Vehicle Model/torque_wheel:1 -> Vehicle Model/vehicle:2
LINE Vehicle Model/vehicle/Gain:1 -> Vehicle Model/vehicle/gear ratio1:1
LINE Vehicle Model/vehicle/Grade resistance:1 -> Vehicle Model/vehicle/Sum2:2
LINE Vehicle Model/vehicle/Impeller:1 -> Vehicle Model/vehicle/aerodynamic:1
NET Vehicle Model/vehicle/Integrator:1 -> Vehicle Model/vehicle/To Workspace12:1, Vehicle Model/vehicle/To Workspace1:1, Vehicle Model/vehicle/To Workspace6:1, Vehicle Model/vehicle/To Workspace7:1, Vehicle Model/vehicle/dist:1
LINE Vehicle Model/vehicle/Rolling resistance:1 -> Vehicle Model/vehicle/Sum2:3
LINE Vehicle Model/vehicle/Sum2:1 -> Vehicle Model/vehicle/Vehicle Mass:1
LINE Vehicle Model/vehicle/Trigonometric Function1:1 -> Vehicle Model/vehicle/Grade resistance:1
LINE Vehicle Model/vehicle/Trigonometric Function:1 -> Vehicle Model/vehicle/Rolling resistance:1
LINE Vehicle Model/vehicle/Tw:1 -> Vehicle Model/vehicle/m//s to mph2:1
NET Vehicle Model/vehicle/V:1 -> Vehicle Model/vehicle/Impeller:1, Vehicle Model/vehicle/Integrator:1, Vehicle Model/vehicle/To Workspace2:1, Vehicle Model/vehicle/m//s to mph1:1, Vehicle Model/vehicle/v (m//s):1
NET Vehicle Model/vehicle/Vehicle Mass:1 -> Vehicle Model/vehicle/To Workspace4:1, Vehicle Model/vehicle/V:1, Vehicle Model/vehicle/a_ist:1
LINE Vehicle Model/vehicle/aerodynamic:1 -> Vehicle Model/vehicle/Sum2:4
NET Vehicle Model/vehicle/gear ratio1:1 -> Vehicle Model/vehicle/To Workspace3:1, Vehicle Model/vehicle/nm:1
NET Vehicle Model/vehicle/grade_ist:1 -> Vehicle Model/vehicle/Trigonometric Function1:1, Vehicle Model/vehicle/Trigonometric Function:1
LINE Vehicle Model/vehicle/m//s to mph1:1 -> Vehicle Model/vehicle/Gain:1
LINE Vehicle Model/vehicle/m//s to mph2:1 -> Vehicle Model/vehicle/Sum2:1
LINE Vehicle Model/vehicle/s:1 -> Vehicle Model/vehicle/track grade:1
NET Vehicle Model/vehicle/track grade:1 -> Vehicle Model/vehicle/To Workspace5:1, Vehicle Model/vehicle/grade_ist:1
NET Vehicle Model/vehicle:1 -> Vehicle Model/Driver Model:1, Vehicle Model/Goto4:1, Vehicle Model/torque interpreter ONLY MPC2:1, Vehicle Model/vm_v_ist:1
NET Vehicle Model/vehicle:2 -> Vehicle Model/Memory:1, Vehicle Model/vm_s_ist:1
NET Vehicle Model/vehicle:3 -> Vehicle Model/Goto1:1, Vehicle Model/Rate Transition10:1, Vehicle Model/To Workspace8:1, Vehicle Model/n_em:1
LINE Vehicle Model/vehicle:4 -> Vehicle Model/vm_a_ist:1
LINE Vehicle Model/vm_a_ist:1 -> Vehicle Model/a_ist:1
LINE Vehicle Model/vm_mpc_cmd:1 -> Vehicle Model/Switch:1
LINE Vehicle Model/vm_s_ist:1 -> Vehicle Model/s_ist:1
LINE Vehicle Model/vm_s_ist_delayed:1 -> Vehicle Model/vehicle:1
LINE Vehicle Model/vm_v_ist:1 -> Vehicle Model/v_out:1
NET Vehicle Model:1 -> Rate Transition6:1, Reference Trajectory:3
LINE Vehicle Model:2 -> Rate Transition8:1
NET Vehicle Model:3 -> Distance Check:1, Finish Line:1, Racing Distance // m:1, Reference Trajectory:1
LINE Vehicle Model:4 -> Reference Trajectory:2
LINE Vehicle Model:5 -> Rate Transition3:1
LINE mpc outout normalizaiton/Abs1:1 -> mpc outout normalizaiton/Terminator2:1
LINE mpc outout normalizaiton/Abs:1 -> mpc outout normalizaiton/Terminator3:1
LINE mpc outout normalizaiton/Constant3:1 -> mpc outout normalizaiton/Divide:2
LINE mpc outout normalizaiton/Constant4:1 -> mpc outout normalizaiton/Divide2:2
LINE mpc outout normalizaiton/Constant:1 -> mpc outout normalizaiton/Divide1:2
LINE mpc outout normalizaiton/Demux1:1 -> mpc outout normalizaiton/Terminator:1
LINE mpc outout normalizaiton/Demux1:2 -> mpc outout normalizaiton/Terminator1:1
LINE mpc outout normalizaiton/Demux1:3 -> mpc outout normalizaiton/m//s to mph1:1
NET mpc outout normalizaiton/Demux:1 -> mpc outout normalizaiton/Display1:1, mpc outout normalizaiton/Divide:1
NET mpc outout normalizaiton/Demux:2 -> mpc outout normalizaiton/Display3:1, mpc outout normalizaiton/Divide2:1
NET mpc outout normalizaiton/Demux:3 -> mpc outout normalizaiton/Display6:1, mpc outout normalizaiton/Divide1:1
LINE mpc outout normalizaiton/Divide1:1 -> mpc outout normalizaiton/Saturation1:1
LINE mpc outout normalizaiton/Divide2:1 -> mpc outout normalizaiton/Gain:1
LINE mpc outout normalizaiton/Divide:1 -> mpc outout normalizaiton/Saturation:1
NET mpc outout normalizaiton/Gain1:1 -> mpc outout normalizaiton/max gen torque lookup:1, mpc outout normalizaiton/max mot torque lookup:1
NET mpc outout normalizaiton/Gain:1 -> mpc outout normalizaiton/Display7:1, mpc outout normalizaiton/Saturation2:1
LINE mpc outout normalizaiton/Mux:1 -> mpc outout normalizaiton/mpc_cmd:1
LINE mpc outout normalizaiton/Rate Transition1:1 -> mpc outout normalizaiton/To Workspace1:1
LINE mpc outout normalizaiton/Rate Transition5:1 -> mpc outout normalizaiton/To Workspace:1
NET mpc outout normalizaiton/Saturation1:1 -> mpc outout normalizaiton/Display5:1, mpc outout normalizaiton/Mux:3
NET mpc outout normalizaiton/Saturation2:1 -> mpc outout normalizaiton/Display4:1, mpc outout normalizaiton/Mux:2
NET mpc outout normalizaiton/Saturation:1 -> mpc outout normalizaiton/Display2:1, mpc outout normalizaiton/Mux:1
LINE mpc outout normalizaiton/m//s to mph1:1 -> mpc outout normalizaiton/Gain1:1
NET mpc outout normalizaiton/max gen torque lookup:1 -> mpc outout normalizaiton/Abs1:1, mpc outout normalizaiton/Rate Transition1:1
NET mpc outout normalizaiton/max mot torque lookup:1 -> mpc outout normalizaiton/Abs:1, mpc outout normalizaiton/Rate Transition5:1
LINE mpc outout normalizaiton/mpc_cmd:1 -> mpc outout normalizaiton/mpc_output (acc, brake):1
LINE mpc outout normalizaiton/mv:1 -> mpc outout normalizaiton/Demux:1
LINE mpc outout normalizaiton/ov:1 -> mpc outout normalizaiton/Demux1:1
LINE mpc outout normalizaiton:1 -> Rate Transition5:1
NET uminmax/Gain1:1 -> uminmax/max gen torque lookup:1, uminmax/max mot torque lookup:1
LINE uminmax/M_em,acc, max:1 -> uminmax/Product:2
LINE uminmax/M_em,acc, min:1 -> uminmax/Product2:2
LINE uminmax/M_frict _brake max:1 -> uminmax/Product1:2
LINE uminmax/M_frict _brake min:1 -> uminmax/Product3:2
LINE uminmax/Matrix Concatenate1:1 -> uminmax/umin:1
LINE uminmax/Matrix Concatenate:1 -> uminmax/umax:1
LINE uminmax/Product1:1 -> uminmax/Matrix Concatenate:3
LINE uminmax/Product2:1 -> uminmax/Matrix Concatenate1:1
LINE uminmax/Product3:1 -> uminmax/Matrix Concatenate1:3
LINE uminmax/Product:1 -> uminmax/Matrix Concatenate:2
NET uminmax/horizon1:1 -> uminmax/Product1:1, uminmax/Product:1
NET uminmax/horizon2:1 -> uminmax/Product2:1, uminmax/Product3:1
LINE uminmax/m//s to mph1:1 -> uminmax/Gain1:1
LINE uminmax/max gen torque lookup:1 -> uminmax/Matrix Concatenate1:2
LINE uminmax/max mot torque lookup:1 -> uminmax/Matrix Concatenate:1
LINE uminmax/v_preview (m//s):1 -> uminmax/m//s to mph1:1
LINE uminmax:1 -> To Workspace:1
LINE uminmax:2 -> To Workspace1:1
note: NET lines group one-source signal fan-out (src -> all destinations, sorted); 1:1 wires keep LINE
CHART MPC/MATLAB Function1 states=1 transitions=1
  STATE_LABEL 'eML_blk_kernel()'
  STATE_LABEL 'SCRIPT:\nfunction par_traj_merged = get_par_traj(phi,v_r,P)\n%#codegen\n%     y_ref_merged = zeros(150,1);\n%     y_ref_merged = zeros(P*(n_controls-2+n_states),1);\n    j = 1;\n    % Depended on: y _ [v, M_EM_acc, M_EM_brk, M-fric_brk];\n    \n    par_traj_merged = zeros(160,1);\n    for i=1:(P+1) % (or until P+1)\n        par_traj_merged(j) = phi(i); % v\n        j = j+1;\n        if i == (P+1)\n            ...<+427ch>'
CHART Vehicle Model/Thermisches Modell EM - LPTN/Subsystem1/MATLAB Function states=1 transitions=1
  STATE_LABEL 'eML_blk_kernel()'
  STATE_LABEL 'SCRIPT:\nfunction P_Iron_Mot = fcn(speed, torque)\n% meanx_iron, meanx_current, meanx_frict, stdx_iron, stdx_current,...\n%     stdx_frict, meany_iron, meany_current, meany_frict, stdy_iron, stdy_current, stdy_frict]\n% Moteral:\n% The idea is that the x variable is replaced by (x-mean(x))/std(x) and the y variable is\n% replace similarly. This is done before any polynomial terms are computed. The trans...<+729ch>'
CHART Distance Check/Distance Change Security Check/MATLAB Function states=1 transitions=1
  STATE_LABEL 'eML_blk_kernel()'
  STATE_LABEL 'SCRIPT:\nfunction bool_stop = distance_check(s,s_old, start_distance_check, break_criteria)\n% start_distance_check in meters\n% break_criteria in meters\n\nif s  >= start_distance_check\n    if (s-s_old) <= break_criteria\n        bool_stop = 1;\n    else\n        bool_stop = 0;\n    end\nelse\n    bool_stop = 0;\nend\n'
CHART Vehicle Model/Thermisches Modell EM - LPTN/Subsystem2/MATLAB Function states=1 transitions=1
  STATE_LABEL 'eML_blk_kernel()'
  STATE_LABEL 'SCRIPT:\nfunction P_Frict_Mot = fcn(speed, torque)\n% meanx_iron, meanx_current, meanx_frict, stdx_iron, stdx_current,...\n%     stdx_frict, meany_iron, meany_current, meany_frict, stdy_iron, stdy_current, stdy_frict]\n% Moteral:\n% The idea is that the x variable is replaced by (x-mean(x))/std(x) and the y variable is\n% replace similarly. This is done before any polynomial terms are computed. The tran...<+544ch>'
CHART Reference Trajectory/distance preview states=1 transitions=1
  STATE_LABEL 'eML_blk_kernel()'
  STATE_LABEL "SCRIPT:\nfunction [s_prev,a_prev] = preview_dist(v_ist,s_ist,a_ist,Ts,p_hor,s_matrix,v_prev_old,delta_v_matrix,t_in)\n%#codegen\n%Initialisierung\ns_out = s_matrix;\na = s_matrix;\ndeltav = delta_v_matrix;\n\n\ndeltav = diff(v_prev_old)';\n% s_ist = s_ist+1;\n\nif t_in >1\n    a(1) = a_ist;\n    a(2:end-1) = deltav(2:end)/Ts;\n    a(end) = deltav(end)/Ts;\n    %         a(1:end-1) = deltav(1:end)/Ts;\n    %       ...<+589ch>"
CHART Vehicle Model/Thermisches Modell EM - LPTN/Subsystem3/MATLAB Function states=1 transitions=1
  STATE_LABEL 'eML_blk_kernel()'
  STATE_LABEL 'SCRIPT:\nfunction P_Current_Mot = fcn(speed, torque)\n% meanx_iron, meanx_current, meanx_frict, stdx_iron, stdx_current,...\n%     stdx_frict, meany_iron, meany_current, meany_frict, stdy_iron, stdy_current, stdy_frict]\n% Moteral:\n% The idea is that the x variable is replaced by (x-mean(x))/std(x) and the y variable is\n% replace similarly. This is done before any polynomial terms are computed. The tr...<+742ch>'
CHART MPC/MATLAB Function states=1 transitions=1
  STATE_LABEL 'eML_blk_kernel()'
  STATE_LABEL 'SCRIPT:\nfunction y_ref_merged = get_ref_traj(x,u1,P)\n%#codegen\n%     y_ref_merged = zeros(150,1);\n%     y_ref_merged = zeros(P*(n_controls-2+n_states),1);\n    j = 1;\n    % Depended on: y _ [v, M_EM_acc, M_EM_brk, M-fric_brk];\n    \n    y_ref_merged = zeros(160,1);\n    for i=1:P\n        y_ref_merged(j) = x(i); % v\n        j = j+1;\n        y_ref_merged(j) = u1(i); % u1\n        j = j+1;\n        y_ref_...<+399ch>'
CHART MPC/SolverStop/MATLAB Function states=1 transitions=1
  STATE_LABEL 'eML_blk_kernel()'
  STATE_LABEL 'SCRIPT:\nfunction bool_stop = solver_status_check(solver_status)\n% start_distance_check in meters\n% break_criteria in meters\n\nif solver_status  == 4\n    bool_stop = 1;\nelse\n    bool_stop = 0;\nend\n'
CHART MPC/Pred_Traj_and_costs_calc/Subsystem/MATLAB Function states=1 transitions=1
  STATE_LABEL 'eML_blk_kernel()'
  STATE_LABEL 'SCRIPT:\nfunction [cost, cost_Q, cost_R, cost_U, cost_traj] = calc_costs(v, v_ref, u, dt_u, Q, R, U, P)\n%#codegen\n% cost = 0;\ncost_Q = 0;\ncost_U = 0;\ncost_R = 0;\n% cost_traj = zeros(30);\nfor i=1:P\n    cost_Q = cost_Q + (v(i)-v_ref(i))^2*Q;\n    cost_U = cost_U + u(i)^2*R ;\n    cost_R = cost_R + dt_u(i)^2*U; \nend\ncost = cost_Q + cost_R + cost_U;\ncost_traj = (v-v_ref).*(v-v_ref)*Q + u.*u*R + dt_u.*dt_...<+5ch>'
CHART  states=0 transitions=0
CHART  states=0 transitions=0
CHART  states=0 transitions=0
CHART  states=0 transitions=0
CHART  states=0 transitions=0
CHART  states=0 transitions=0
CHART  states=0 transitions=0
CHART  states=0 transitions=0
CHART  states=0 transitions=0
